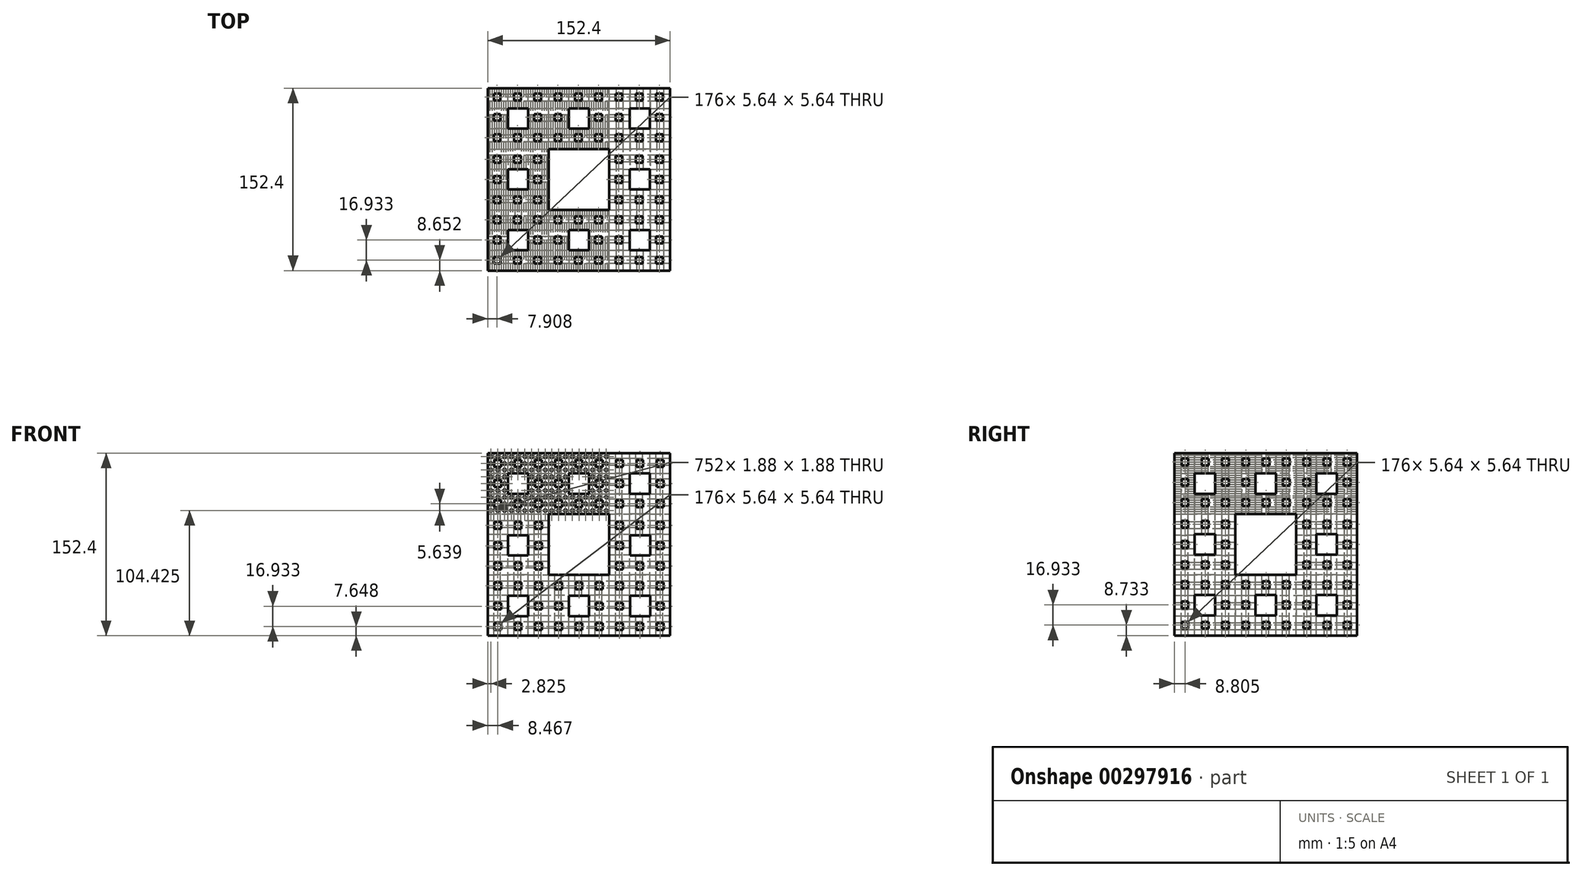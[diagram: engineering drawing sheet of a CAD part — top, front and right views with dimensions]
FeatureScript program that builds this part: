
annotation { "Feature Type Name" : "Feature", "Feature Type Description" : "" }
export const myFeature = defineFeature(function(context is Context, id is Id, definition is map)
    precondition{}
    {
        {
            var Q0;
            Q0=qCreatedBy(makeId("Top.planeOp"),FACE);
            var sketch = newSketch(context, id + "F0", { "sketchPlane" : qUnion([Q0])});
            skLineSegment(sketch, "E0.bottom", {"start": v(76.2, 76.2) * mm, "end": v(-76.2, 76.2) * mm});
            skLineSegment(sketch, "E0.top", {"start": v(76.2, -76.2) * mm, "end": v(-76.2, -76.2) * mm});
            skLineSegment(sketch, "E0.left", {"start": v(76.2, 76.2) * mm, "end": v(76.2, -76.2) * mm});
            skLineSegment(sketch, "E0.right", {"start": v(-76.2, 76.2) * mm, "end": v(-76.2, -76.2) * mm});
            skPoint(sketch, "E0.middle", {"position": v(0, 0) * mm});
            skSolve(sketch);
        }
        {
            var Q0;
            Q0=makeQuery(id+"F0.imprint","IMPRINT",FACE,{"disambiguationData":[TD([[makeQuery(id+"F0.imprint","IMPRINT",EDGE,{"derivedFrom":sQuery(id+"F0.wireOp",EDGE,"E0.bottom")}),1.0]])]});
            extrude(context, id + "F1", {"entities" : qUnion([Q0]), "depth" : 152.4 * mm});
        }
        {
            var Q0;
            Q0=makeQuery(id+"F1.opExtrude","CAP_FACE",FACE,{"disambiguationData":[OSD([sQuery(id+"F0.wireOp",EDGE,"E0.bottom"),sQuery(id+"F0.wireOp",EDGE,"E0.top"),sQuery(id+"F0.wireOp",EDGE,"E0.left"),sQuery(id+"F0.wireOp",EDGE,"E0.right")])],"isStart":false});
            var sketch = newSketch(context, id + "F2", { "sketchPlane" : qUnion([Q0])});
            skLineSegment(sketch, "E1.bottom", {"start": v(-25.4, 25.4) * mm, "end": v(25.4, 25.4) * mm});
            skLineSegment(sketch, "E1.top", {"start": v(-25.4, -25.4) * mm, "end": v(25.4, -25.4) * mm});
            skLineSegment(sketch, "E1.left", {"start": v(-25.4, 25.4) * mm, "end": v(-25.4, -25.4) * mm});
            skLineSegment(sketch, "E1.right", {"start": v(25.4, 25.4) * mm, "end": v(25.4, -25.4) * mm});
            skPoint(sketch, "E1.middle", {"position": v(0, 0) * mm});
            skSolve(sketch);
        }
        {
            var Q0;
            Q0=makeQuery(id+"F2.imprint","IMPRINT",FACE,{"disambiguationData":[TD([[makeQuery(id+"F2.imprint","IMPRINT",EDGE,{"derivedFrom":sQuery(id+"F2.wireOp",EDGE,"E1.bottom")}),-1.0]])]});
            extrude(context, id + "F3", {"entities" : qUnion([Q0]), "operationType" : NewBodyOperationType.REMOVE, "oppositeDirection" : true, "depth" : 216.15 * mm});
        }
        {
            var Q0;
            Q0=makeQuery(id+"F1.opExtrude","SWEPT_FACE",FACE,{"disambiguationData":[OSD([sQuery(id+"F0.wireOp",EDGE,"E0.left")])]});
            var sketch = newSketch(context, id + "F4", { "sketchPlane" : qUnion([Q0])});
            skLineSegment(sketch, "E2.bottom", {"start": v(25.4, 101.6) * mm, "end": v(-25.4, 101.6) * mm});
            skLineSegment(sketch, "E2.top", {"start": v(25.4, 50.8) * mm, "end": v(-25.4, 50.8) * mm});
            skLineSegment(sketch, "E2.left", {"start": v(25.4, 101.6) * mm, "end": v(25.4, 50.8) * mm});
            skLineSegment(sketch, "E2.right", {"start": v(-25.4, 101.6) * mm, "end": v(-25.4, 50.8) * mm});
            skPoint(sketch, "E2.middle", {"position": v(0, 76.2) * mm});
            skPoint(sketch, "E2.middle.positionSnap0", {"position": v(-76.2, 76.2) * mm});
            skPoint(sketch, "E2.centerSnap0", {"position": v(-76.2, 76.2) * mm});
            skSolve(sketch);
        }
        {
            var Q0;
            Q0=makeQuery(id+"F4.imprint","IMPRINT",FACE,{"disambiguationData":[TD([[makeQuery(id+"F4.imprint","IMPRINT",EDGE,{"derivedFrom":sQuery(id+"F4.wireOp",EDGE,"E2.bottom")}),1.0]])]});
            extrude(context, id + "F5", {"entities" : qUnion([Q0]), "operationType" : NewBodyOperationType.REMOVE, "oppositeDirection" : true, "depth" : 233.17 * mm});
        }
        {
            var Q0;
            Q0=makeQuery(id+"F1.opExtrude","SWEPT_FACE",FACE,{"disambiguationData":[OSD([sQuery(id+"F0.wireOp",EDGE,"E0.bottom")])]});
            var sketch = newSketch(context, id + "F6", { "sketchPlane" : qUnion([Q0])});
            skLineSegment(sketch, "E3.bottom", {"start": v(25.4, 101.6) * mm, "end": v(-25.4, 101.6) * mm});
            skLineSegment(sketch, "E3.top", {"start": v(25.4, 50.8) * mm, "end": v(-25.4, 50.8) * mm});
            skLineSegment(sketch, "E3.left", {"start": v(25.4, 101.6) * mm, "end": v(25.4, 50.8) * mm});
            skLineSegment(sketch, "E3.right", {"start": v(-25.4, 101.6) * mm, "end": v(-25.4, 50.8) * mm});
            skPoint(sketch, "E3.middle", {"position": v(0, 76.2) * mm});
            skPoint(sketch, "E3.middle.positionSnap0", {"position": v(-76.2, 76.2) * mm});
            skPoint(sketch, "E3.centerSnap0", {"position": v(-76.2, 76.2) * mm});
            skSolve(sketch);
        }
        {
            var Q0;
            Q0=makeQuery(id+"F6.imprint","IMPRINT",FACE,{"disambiguationData":[TD([[makeQuery(id+"F6.imprint","IMPRINT",EDGE,{"derivedFrom":sQuery(id+"F6.wireOp",EDGE,"E3.bottom")}),1.0]])]});
            extrude(context, id + "F7", {"entities" : qUnion([Q0]), "operationType" : NewBodyOperationType.REMOVE, "oppositeDirection" : true, "depth" : 261.62 * mm});
        }
        {
            var Q0;
            Q0=makeQuery(id+"F1.opExtrude","SWEPT_FACE",FACE,{"disambiguationData":[OSD([sQuery(id+"F0.wireOp",EDGE,"E0.top")])]});
            var sketch = newSketch(context, id + "F8", { "sketchPlane" : qUnion([Q0])});
            skLineSegment(sketch, "E4.bottom", {"start": v(-42.33, 135.47) * mm, "end": v(-59.27, 135.47) * mm});
            skLineSegment(sketch, "E4.top", {"start": v(-42.33, 118.53) * mm, "end": v(-59.27, 118.53) * mm});
            skLineSegment(sketch, "E4.left", {"start": v(-42.33, 135.47) * mm, "end": v(-42.33, 118.53) * mm});
            skLineSegment(sketch, "E4.right", {"start": v(-59.27, 135.47) * mm, "end": v(-59.27, 118.53) * mm});
            skPoint(sketch, "E4.middle", {"position": v(-50.8, 127) * mm});
            skLineSegment(sketch, "E5.1.0.0", {"start": v(8.47, 135.47) * mm, "end": v(-8.47, 135.47) * mm});
            skLineSegment(sketch, "E5.1.0.1", {"start": v(8.47, 135.47) * mm, "end": v(8.47, 118.53) * mm});
            skLineSegment(sketch, "E5.1.0.2", {"start": v(8.47, 118.53) * mm, "end": v(-8.47, 118.53) * mm});
            skLineSegment(sketch, "E5.1.0.3", {"start": v(-8.47, 135.47) * mm, "end": v(-8.47, 118.53) * mm});
            skLineSegment(sketch, "E5.2.0.0", {"start": v(59.27, 135.47) * mm, "end": v(42.33, 135.47) * mm});
            skLineSegment(sketch, "E5.2.0.1", {"start": v(59.27, 135.47) * mm, "end": v(59.27, 118.53) * mm});
            skLineSegment(sketch, "E5.2.0.2", {"start": v(59.27, 118.53) * mm, "end": v(42.33, 118.53) * mm});
            skLineSegment(sketch, "E5.2.0.3", {"start": v(42.33, 135.47) * mm, "end": v(42.33, 118.53) * mm});
            skLineSegment(sketch, "E5.direction1", {"start": v(-59.27, 135.47) * mm, "end": v(-8.47, 135.47) * mm, "construction": true});
            skLineSegment(sketch, "E6.bottom", {"start": v(-59.27, 83.76) * mm, "end": v(-42.33, 83.76) * mm});
            skLineSegment(sketch, "E6.top", {"start": v(-59.27, 66.83) * mm, "end": v(-42.33, 66.83) * mm});
            skLineSegment(sketch, "E6.left", {"start": v(-59.27, 83.76) * mm, "end": v(-59.27, 66.83) * mm});
            skLineSegment(sketch, "E6.right", {"start": v(-42.33, 83.76) * mm, "end": v(-42.33, 66.83) * mm});
            skPoint(sketch, "E6.middle", {"position": v(-50.8, 75.3) * mm});
            skLineSegment(sketch, "E7.bottom", {"start": v(-59.27, 33.21) * mm, "end": v(-42.33, 33.21) * mm});
            skLineSegment(sketch, "E7.top", {"start": v(-59.27, 16.28) * mm, "end": v(-42.33, 16.28) * mm});
            skLineSegment(sketch, "E7.left", {"start": v(-59.27, 33.21) * mm, "end": v(-59.27, 16.28) * mm});
            skLineSegment(sketch, "E7.right", {"start": v(-42.33, 33.21) * mm, "end": v(-42.33, 16.28) * mm});
            skPoint(sketch, "E7.middle", {"position": v(-50.8, 24.74) * mm});
            skLineSegment(sketch, "E8.bottom", {"start": v(-8.47, 33.21) * mm, "end": v(8.47, 33.21) * mm});
            skLineSegment(sketch, "E8.top", {"start": v(-8.47, 16.28) * mm, "end": v(8.47, 16.28) * mm});
            skLineSegment(sketch, "E8.left", {"start": v(-8.47, 33.21) * mm, "end": v(-8.47, 16.28) * mm});
            skLineSegment(sketch, "E8.right", {"start": v(8.47, 33.21) * mm, "end": v(8.47, 16.28) * mm});
            skPoint(sketch, "E8.middle", {"position": v(0, 24.74) * mm});
            skPoint(sketch, "E8.middle.positionSnap0", {"position": v(-42.33, 24.74) * mm});
            skPoint(sketch, "E8.centerSnap0", {"position": v(-42.33, 24.74) * mm});
            skLineSegment(sketch, "E9.bottom", {"start": v(42.62, 33.21) * mm, "end": v(59.55, 33.21) * mm});
            skLineSegment(sketch, "E9.top", {"start": v(42.62, 16.28) * mm, "end": v(59.55, 16.28) * mm});
            skLineSegment(sketch, "E9.left", {"start": v(42.62, 33.21) * mm, "end": v(42.62, 16.28) * mm});
            skLineSegment(sketch, "E9.right", {"start": v(59.55, 33.21) * mm, "end": v(59.55, 16.28) * mm});
            skPoint(sketch, "E9.middle", {"position": v(51.09, 24.74) * mm});
            skPoint(sketch, "E9.middle.positionSnap0", {"position": v(8.47, 24.74) * mm});
            skPoint(sketch, "E9.centerSnap0", {"position": v(8.47, 24.74) * mm});
            skLineSegment(sketch, "E10.bottom", {"start": v(59.55, 83.76) * mm, "end": v(42.62, 83.76) * mm});
            skLineSegment(sketch, "E10.top", {"start": v(59.55, 66.83) * mm, "end": v(42.62, 66.83) * mm});
            skLineSegment(sketch, "E10.left", {"start": v(59.55, 83.76) * mm, "end": v(59.55, 66.83) * mm});
            skLineSegment(sketch, "E10.right", {"start": v(42.62, 83.76) * mm, "end": v(42.62, 66.83) * mm});
            skPoint(sketch, "E10.middle", {"position": v(51.09, 75.3) * mm});
            skPoint(sketch, "E10.middle.positionSnap0", {"position": v(-42.33, 75.3) * mm});
            skPoint(sketch, "E10.middle.positionSnap1", {"position": v(51.09, 33.21) * mm});
            skPoint(sketch, "E10.centerSnap0", {"position": v(-42.33, 75.3) * mm});
            skPoint(sketch, "E10.centerSnap1", {"position": v(51.09, 33.21) * mm});
            skSolve(sketch);
        }
        {
            var Q0;
            Q0=makeQuery(id+"F8.imprint","IMPRINT",FACE,{"disambiguationData":[TD([[makeQuery(id+"F8.imprint","IMPRINT",EDGE,{"derivedFrom":sQuery(id+"F8.wireOp",EDGE,"E5.1.0.0")}),1.0]])]});
            var Q1;
            Q1=makeQuery(id+"F8.imprint","IMPRINT",FACE,{"disambiguationData":[TD([[makeQuery(id+"F8.imprint","IMPRINT",EDGE,{"derivedFrom":sQuery(id+"F8.wireOp",EDGE,"E5.2.0.0")}),1.0]])]});
            var Q2;
            Q2=makeQuery(id+"F8.imprint","IMPRINT",FACE,{"disambiguationData":[TD([[makeQuery(id+"F8.imprint","IMPRINT",EDGE,{"derivedFrom":sQuery(id+"F8.wireOp",EDGE,"E10.bottom")}),1.0]])]});
            var Q3;
            Q3=makeQuery(id+"F8.imprint","IMPRINT",FACE,{"disambiguationData":[TD([[makeQuery(id+"F8.imprint","IMPRINT",EDGE,{"derivedFrom":sQuery(id+"F8.wireOp",EDGE,"E9.bottom")}),-1.0]])]});
            var Q4;
            Q4=makeQuery(id+"F8.imprint","IMPRINT",FACE,{"disambiguationData":[TD([[makeQuery(id+"F8.imprint","IMPRINT",EDGE,{"derivedFrom":sQuery(id+"F8.wireOp",EDGE,"E8.bottom")}),-1.0]])]});
            var Q5;
            Q5=makeQuery(id+"F8.imprint","IMPRINT",FACE,{"disambiguationData":[TD([[makeQuery(id+"F8.imprint","IMPRINT",EDGE,{"derivedFrom":sQuery(id+"F8.wireOp",EDGE,"E7.bottom")}),-1.0]])]});
            var Q6;
            Q6=makeQuery(id+"F8.imprint","IMPRINT",FACE,{"disambiguationData":[TD([[makeQuery(id+"F8.imprint","IMPRINT",EDGE,{"derivedFrom":sQuery(id+"F8.wireOp",EDGE,"E6.bottom")}),-1.0]])]});
            var Q7;
            Q7=makeQuery(id+"F8.imprint","IMPRINT",FACE,{"disambiguationData":[TD([[makeQuery(id+"F8.imprint","IMPRINT",EDGE,{"derivedFrom":sQuery(id+"F8.wireOp",EDGE,"E4.bottom")}),1.0]])]});
            extrude(context, id + "F9", {"entities" : qUnion([Q0, Q1, Q2, Q3, Q4, Q5, Q6, Q7]), "operationType" : NewBodyOperationType.REMOVE, "endBound" : BoundingType.THROUGH_ALL, "oppositeDirection" : true, "depth" : 25.4 * mm});
        }
        {
            var Q0;
            Q0=makeQuery(id+"F1.opExtrude","SWEPT_FACE",FACE,{"disambiguationData":[OSD([sQuery(id+"F0.wireOp",EDGE,"E0.left")])]});
            var sketch = newSketch(context, id + "F10", { "sketchPlane" : qUnion([Q0])});
            skLineSegment(sketch, "E11.bottom", {"start": v(-42.33, 135.47) * mm, "end": v(-59.27, 135.47) * mm});
            skLineSegment(sketch, "E11.top", {"start": v(-42.33, 118.53) * mm, "end": v(-59.27, 118.53) * mm});
            skLineSegment(sketch, "E11.left", {"start": v(-42.33, 135.47) * mm, "end": v(-42.33, 118.53) * mm});
            skLineSegment(sketch, "E11.right", {"start": v(-59.27, 135.47) * mm, "end": v(-59.27, 118.53) * mm});
            skPoint(sketch, "E11.middle", {"position": v(-50.8, 127) * mm});
            skLineSegment(sketch, "E12.bottom", {"start": v(8.47, 135.47) * mm, "end": v(-8.47, 135.47) * mm});
            skLineSegment(sketch, "E12.top", {"start": v(8.47, 118.53) * mm, "end": v(-8.47, 118.53) * mm});
            skLineSegment(sketch, "E12.left", {"start": v(8.47, 135.47) * mm, "end": v(8.47, 118.53) * mm});
            skLineSegment(sketch, "E12.right", {"start": v(-8.47, 135.47) * mm, "end": v(-8.47, 118.53) * mm});
            skPoint(sketch, "E12.middle", {"position": v(0, 127) * mm});
            skLineSegment(sketch, "E13.bottom", {"start": v(59.27, 135.47) * mm, "end": v(42.33, 135.47) * mm});
            skLineSegment(sketch, "E13.top", {"start": v(59.27, 118.53) * mm, "end": v(42.33, 118.53) * mm});
            skLineSegment(sketch, "E13.left", {"start": v(59.27, 135.47) * mm, "end": v(59.27, 118.53) * mm});
            skLineSegment(sketch, "E13.right", {"start": v(42.33, 135.47) * mm, "end": v(42.33, 118.53) * mm});
            skPoint(sketch, "E13.middle", {"position": v(50.8, 127) * mm});
            skLineSegment(sketch, "E14.bottom", {"start": v(42.33, 84.67) * mm, "end": v(59.27, 84.67) * mm});
            skLineSegment(sketch, "E14.top", {"start": v(42.33, 67.73) * mm, "end": v(59.27, 67.73) * mm});
            skLineSegment(sketch, "E14.left", {"start": v(42.33, 84.67) * mm, "end": v(42.33, 67.73) * mm});
            skLineSegment(sketch, "E14.right", {"start": v(59.27, 84.67) * mm, "end": v(59.27, 67.73) * mm});
            skPoint(sketch, "E14.middle", {"position": v(50.8, 76.2) * mm});
            skLineSegment(sketch, "E15.bottom", {"start": v(42.33, 33.87) * mm, "end": v(59.27, 33.87) * mm});
            skLineSegment(sketch, "E15.top", {"start": v(42.33, 16.93) * mm, "end": v(59.27, 16.93) * mm});
            skLineSegment(sketch, "E15.left", {"start": v(42.33, 33.87) * mm, "end": v(42.33, 16.93) * mm});
            skLineSegment(sketch, "E15.right", {"start": v(59.27, 33.87) * mm, "end": v(59.27, 16.93) * mm});
            skPoint(sketch, "E15.middle", {"position": v(50.8, 25.4) * mm});
            skLineSegment(sketch, "E16.bottom", {"start": v(-59.27, 84.67) * mm, "end": v(-42.33, 84.67) * mm});
            skLineSegment(sketch, "E16.top", {"start": v(-59.27, 67.73) * mm, "end": v(-42.33, 67.73) * mm});
            skLineSegment(sketch, "E16.left", {"start": v(-59.27, 84.67) * mm, "end": v(-59.27, 67.73) * mm});
            skLineSegment(sketch, "E16.right", {"start": v(-42.33, 84.67) * mm, "end": v(-42.33, 67.73) * mm});
            skPoint(sketch, "E16.middle", {"position": v(-50.8, 76.2) * mm});
            skLineSegment(sketch, "E17.bottom", {"start": v(-59.27, 33.87) * mm, "end": v(-42.33, 33.87) * mm});
            skLineSegment(sketch, "E17.top", {"start": v(-59.27, 16.93) * mm, "end": v(-42.33, 16.93) * mm});
            skLineSegment(sketch, "E17.left", {"start": v(-59.27, 33.87) * mm, "end": v(-59.27, 16.93) * mm});
            skLineSegment(sketch, "E17.right", {"start": v(-42.33, 33.87) * mm, "end": v(-42.33, 16.93) * mm});
            skPoint(sketch, "E17.middle", {"position": v(-50.8, 25.4) * mm});
            skLineSegment(sketch, "E18.bottom", {"start": v(-8.47, 33.87) * mm, "end": v(8.47, 33.87) * mm});
            skLineSegment(sketch, "E18.top", {"start": v(-8.47, 16.93) * mm, "end": v(8.47, 16.93) * mm});
            skLineSegment(sketch, "E18.left", {"start": v(-8.47, 33.87) * mm, "end": v(-8.47, 16.93) * mm});
            skLineSegment(sketch, "E18.right", {"start": v(8.47, 33.87) * mm, "end": v(8.47, 16.93) * mm});
            skPoint(sketch, "E18.middle", {"position": v(0, 25.4) * mm});
            skSolve(sketch);
        }
        {
            var Q0;
            Q0=makeQuery(id+"F10.imprint","IMPRINT",FACE,{"disambiguationData":[TD([[makeQuery(id+"F10.imprint","IMPRINT",EDGE,{"derivedFrom":sQuery(id+"F10.wireOp",EDGE,"E11.bottom")}),1.0]])]});
            var Q1;
            Q1=makeQuery(id+"F10.imprint","IMPRINT",FACE,{"disambiguationData":[TD([[makeQuery(id+"F10.imprint","IMPRINT",EDGE,{"derivedFrom":sQuery(id+"F10.wireOp",EDGE,"E12.bottom")}),1.0]])]});
            var Q2;
            Q2=makeQuery(id+"F10.imprint","IMPRINT",FACE,{"disambiguationData":[TD([[makeQuery(id+"F10.imprint","IMPRINT",EDGE,{"derivedFrom":sQuery(id+"F10.wireOp",EDGE,"E13.bottom")}),1.0]])]});
            var Q3;
            Q3=makeQuery(id+"F10.imprint","IMPRINT",FACE,{"disambiguationData":[TD([[makeQuery(id+"F10.imprint","IMPRINT",EDGE,{"derivedFrom":sQuery(id+"F10.wireOp",EDGE,"E14.bottom")}),-1.0]])]});
            var Q4;
            Q4=makeQuery(id+"F10.imprint","IMPRINT",FACE,{"disambiguationData":[TD([[makeQuery(id+"F10.imprint","IMPRINT",EDGE,{"derivedFrom":sQuery(id+"F10.wireOp",EDGE,"E15.bottom")}),-1.0]])]});
            var Q5;
            Q5=makeQuery(id+"F10.imprint","IMPRINT",FACE,{"disambiguationData":[TD([[makeQuery(id+"F10.imprint","IMPRINT",EDGE,{"derivedFrom":sQuery(id+"F10.wireOp",EDGE,"E18.bottom")}),-1.0]])]});
            var Q6;
            Q6=makeQuery(id+"F10.imprint","IMPRINT",FACE,{"disambiguationData":[TD([[makeQuery(id+"F10.imprint","IMPRINT",EDGE,{"derivedFrom":sQuery(id+"F10.wireOp",EDGE,"E17.bottom")}),-1.0]])]});
            var Q7;
            Q7=makeQuery(id+"F10.imprint","IMPRINT",FACE,{"disambiguationData":[TD([[makeQuery(id+"F10.imprint","IMPRINT",EDGE,{"derivedFrom":sQuery(id+"F10.wireOp",EDGE,"E16.bottom")}),-1.0]])]});
            extrude(context, id + "F11", {"entities" : qUnion([Q0, Q1, Q2, Q3, Q4, Q5, Q6, Q7]), "operationType" : NewBodyOperationType.REMOVE, "endBound" : BoundingType.THROUGH_ALL, "oppositeDirection" : true, "depth" : 25.4 * mm});
        }
        {
            var Q0;
            Q0=makeQuery(id+"F1.opExtrude","CAP_FACE",FACE,{"disambiguationData":[OSD([sQuery(id+"F0.wireOp",EDGE,"E0.bottom"),sQuery(id+"F0.wireOp",EDGE,"E0.top"),sQuery(id+"F0.wireOp",EDGE,"E0.left"),sQuery(id+"F0.wireOp",EDGE,"E0.right")])],"isStart":false});
            var sketch = newSketch(context, id + "F12", { "sketchPlane" : qUnion([Q0])});
            skLineSegment(sketch, "E19.bottom", {"start": v(-8.47, 59.27) * mm, "end": v(8.47, 59.27) * mm});
            skLineSegment(sketch, "E19.top", {"start": v(-8.47, 42.33) * mm, "end": v(8.47, 42.33) * mm});
            skLineSegment(sketch, "E19.left", {"start": v(-8.47, 59.27) * mm, "end": v(-8.47, 42.33) * mm});
            skLineSegment(sketch, "E19.right", {"start": v(8.47, 59.27) * mm, "end": v(8.47, 42.33) * mm});
            skPoint(sketch, "E19.middle", {"position": v(0, 50.8) * mm});
            skLineSegment(sketch, "E20.bottom", {"start": v(-59.27, 59.27) * mm, "end": v(-42.33, 59.27) * mm});
            skLineSegment(sketch, "E20.top", {"start": v(-59.27, 42.33) * mm, "end": v(-42.33, 42.33) * mm});
            skLineSegment(sketch, "E20.left", {"start": v(-59.27, 59.27) * mm, "end": v(-59.27, 42.33) * mm});
            skLineSegment(sketch, "E20.right", {"start": v(-42.33, 59.27) * mm, "end": v(-42.33, 42.33) * mm});
            skPoint(sketch, "E20.middle", {"position": v(-50.8, 50.8) * mm});
            skLineSegment(sketch, "E21.bottom", {"start": v(42.33, 59.27) * mm, "end": v(59.27, 59.27) * mm});
            skLineSegment(sketch, "E21.top", {"start": v(42.33, 42.33) * mm, "end": v(59.27, 42.33) * mm});
            skLineSegment(sketch, "E21.left", {"start": v(42.33, 59.27) * mm, "end": v(42.33, 42.33) * mm});
            skLineSegment(sketch, "E21.right", {"start": v(59.27, 59.27) * mm, "end": v(59.27, 42.33) * mm});
            skPoint(sketch, "E21.middle", {"position": v(50.8, 50.8) * mm});
            skLineSegment(sketch, "E22.bottom", {"start": v(59.27, -8.47) * mm, "end": v(42.33, -8.47) * mm});
            skLineSegment(sketch, "E22.top", {"start": v(59.27, 8.47) * mm, "end": v(42.33, 8.47) * mm});
            skLineSegment(sketch, "E22.left", {"start": v(59.27, -8.47) * mm, "end": v(59.27, 8.47) * mm});
            skLineSegment(sketch, "E22.right", {"start": v(42.33, -8.47) * mm, "end": v(42.33, 8.47) * mm});
            skPoint(sketch, "E22.middle", {"position": v(50.8, 0) * mm});
            skLineSegment(sketch, "E23.bottom", {"start": v(59.27, -59.27) * mm, "end": v(42.33, -59.27) * mm});
            skLineSegment(sketch, "E23.top", {"start": v(59.27, -42.33) * mm, "end": v(42.33, -42.33) * mm});
            skLineSegment(sketch, "E23.left", {"start": v(59.27, -59.27) * mm, "end": v(59.27, -42.33) * mm});
            skLineSegment(sketch, "E23.right", {"start": v(42.33, -59.27) * mm, "end": v(42.33, -42.33) * mm});
            skPoint(sketch, "E23.middle", {"position": v(50.8, -50.8) * mm});
            skPoint(sketch, "E24.middle", {"position": v(-8.47, -30.86) * mm});
            skLineSegment(sketch, "E25.bottom", {"start": v(-42.33, -59.27) * mm, "end": v(-59.27, -59.27) * mm});
            skLineSegment(sketch, "E25.top", {"start": v(-42.33, -42.33) * mm, "end": v(-59.27, -42.33) * mm});
            skLineSegment(sketch, "E25.left", {"start": v(-42.33, -59.27) * mm, "end": v(-42.33, -42.33) * mm});
            skLineSegment(sketch, "E25.right", {"start": v(-59.27, -59.27) * mm, "end": v(-59.27, -42.33) * mm});
            skPoint(sketch, "E25.middle", {"position": v(-50.8, -50.8) * mm});
            skLineSegment(sketch, "E26.bottom", {"start": v(-42.33, -8.47) * mm, "end": v(-59.27, -8.47) * mm});
            skLineSegment(sketch, "E26.top", {"start": v(-42.33, 8.47) * mm, "end": v(-59.27, 8.47) * mm});
            skLineSegment(sketch, "E26.left", {"start": v(-42.33, -8.47) * mm, "end": v(-42.33, 8.47) * mm});
            skLineSegment(sketch, "E26.right", {"start": v(-59.27, -8.47) * mm, "end": v(-59.27, 8.47) * mm});
            skPoint(sketch, "E26.middle", {"position": v(-50.8, 0) * mm});
            skLineSegment(sketch, "E27.bottom", {"start": v(-8.47, -42.33) * mm, "end": v(8.47, -42.33) * mm});
            skLineSegment(sketch, "E27.top", {"start": v(-8.47, -59.27) * mm, "end": v(8.47, -59.27) * mm});
            skLineSegment(sketch, "E27.left", {"start": v(-8.47, -42.33) * mm, "end": v(-8.47, -59.27) * mm});
            skLineSegment(sketch, "E27.right", {"start": v(8.47, -42.33) * mm, "end": v(8.47, -59.27) * mm});
            skPoint(sketch, "E27.middle", {"position": v(0, -50.8) * mm});
            skSolve(sketch);
        }
        {
            var Q0;
            Q0=makeQuery(id+"F12.imprint","IMPRINT",FACE,{"disambiguationData":[TD([[makeQuery(id+"F12.imprint","IMPRINT",EDGE,{"derivedFrom":sQuery(id+"F12.wireOp",EDGE,"E20.bottom")}),-1.0]])]});
            var Q1;
            Q1=makeQuery(id+"F12.imprint","IMPRINT",FACE,{"disambiguationData":[TD([[makeQuery(id+"F12.imprint","IMPRINT",EDGE,{"derivedFrom":sQuery(id+"F12.wireOp",EDGE,"E19.bottom")}),-1.0]])]});
            var Q2;
            Q2=makeQuery(id+"F12.imprint","IMPRINT",FACE,{"disambiguationData":[TD([[makeQuery(id+"F12.imprint","IMPRINT",EDGE,{"derivedFrom":sQuery(id+"F12.wireOp",EDGE,"E21.bottom")}),-1.0]])]});
            var Q3;
            Q3=makeQuery(id+"F12.imprint","IMPRINT",FACE,{"disambiguationData":[TD([[makeQuery(id+"F12.imprint","IMPRINT",EDGE,{"derivedFrom":sQuery(id+"F12.wireOp",EDGE,"E22.bottom")}),-1.0]])]});
            var Q4;
            Q4=makeQuery(id+"F12.imprint","IMPRINT",FACE,{"disambiguationData":[TD([[makeQuery(id+"F12.imprint","IMPRINT",EDGE,{"derivedFrom":sQuery(id+"F12.wireOp",EDGE,"E23.bottom")}),-1.0]])]});
            var Q5;
            Q5=makeQuery(id+"F12.imprint","IMPRINT",FACE,{"disambiguationData":[TD([[makeQuery(id+"F12.imprint","IMPRINT",EDGE,{"derivedFrom":sQuery(id+"F12.wireOp",EDGE,"E27.bottom")}),-1.0]])]});
            var Q6;
            Q6=makeQuery(id+"F12.imprint","IMPRINT",FACE,{"disambiguationData":[TD([[makeQuery(id+"F12.imprint","IMPRINT",EDGE,{"derivedFrom":sQuery(id+"F12.wireOp",EDGE,"E25.bottom")}),-1.0]])]});
            var Q7;
            Q7=makeQuery(id+"F12.imprint","IMPRINT",FACE,{"disambiguationData":[TD([[makeQuery(id+"F12.imprint","IMPRINT",EDGE,{"derivedFrom":sQuery(id+"F12.wireOp",EDGE,"E26.bottom")}),-1.0]])]});
            extrude(context, id + "F13", {"entities" : qUnion([Q0, Q1, Q2, Q3, Q4, Q5, Q6, Q7]), "operationType" : NewBodyOperationType.REMOVE, "endBound" : BoundingType.THROUGH_ALL, "oppositeDirection" : true, "depth" : 25.4 * mm});
        }
        {
            var Q0;
            Q0=makeQuery(id+"F1.opExtrude","SWEPT_FACE",FACE,{"disambiguationData":[OSD([sQuery(id+"F0.wireOp",EDGE,"E0.top")])]});
            var sketch = newSketch(context, id + "F14", { "sketchPlane" : qUnion([Q0])});
            skLineSegment(sketch, "E28.bottom", {"start": v(-47.98, 146.76) * mm, "end": v(-53.62, 146.76) * mm});
            skLineSegment(sketch, "E28.top", {"start": v(-47.98, 141.11) * mm, "end": v(-53.62, 141.11) * mm});
            skLineSegment(sketch, "E28.left", {"start": v(-47.98, 146.76) * mm, "end": v(-47.98, 141.11) * mm});
            skLineSegment(sketch, "E28.right", {"start": v(-53.62, 146.76) * mm, "end": v(-53.62, 141.11) * mm});
            skPoint(sketch, "E28.middle", {"position": v(-50.8, 143.93) * mm});
            skPoint(sketch, "E28.middle.positionSnap0", {"position": v(-50.8, 135.47) * mm});
            skPoint(sketch, "E28.centerSnap0", {"position": v(-50.8, 135.47) * mm});
            skLineSegment(sketch, "E29.bottom", {"start": v(-36.69, 146.76) * mm, "end": v(-31.04, 146.76) * mm});
            skLineSegment(sketch, "E29.top", {"start": v(-36.69, 141.11) * mm, "end": v(-31.04, 141.11) * mm});
            skLineSegment(sketch, "E29.left", {"start": v(-36.69, 146.76) * mm, "end": v(-36.69, 141.11) * mm});
            skLineSegment(sketch, "E29.right", {"start": v(-31.04, 146.76) * mm, "end": v(-31.04, 141.11) * mm});
            skPoint(sketch, "E29.middle", {"position": v(-33.87, 143.93) * mm});
            skPoint(sketch, "E29.middle.positionSnap0", {"position": v(-47.98, 143.93) * mm});
            skPoint(sketch, "E29.centerSnap0", {"position": v(-47.98, 143.93) * mm});
            skLineSegment(sketch, "E30.bottom", {"start": v(-70.56, 146.76) * mm, "end": v(-64.91, 146.76) * mm});
            skLineSegment(sketch, "E30.top", {"start": v(-70.56, 141.11) * mm, "end": v(-64.91, 141.11) * mm});
            skLineSegment(sketch, "E30.left", {"start": v(-70.56, 146.76) * mm, "end": v(-70.56, 141.11) * mm});
            skLineSegment(sketch, "E30.right", {"start": v(-64.91, 146.76) * mm, "end": v(-64.91, 141.11) * mm});
            skPoint(sketch, "E30.middle", {"position": v(-67.73, 143.93) * mm});
            skPoint(sketch, "E30.middle.positionSnap0", {"position": v(-53.62, 143.93) * mm});
            skPoint(sketch, "E30.centerSnap0", {"position": v(-53.62, 143.93) * mm});
            skLineSegment(sketch, "E31.bottom", {"start": v(-64.91, 129.82) * mm, "end": v(-70.56, 129.82) * mm});
            skLineSegment(sketch, "E31.top", {"start": v(-64.91, 124.18) * mm, "end": v(-70.56, 124.18) * mm});
            skLineSegment(sketch, "E31.left", {"start": v(-64.91, 129.82) * mm, "end": v(-64.91, 124.18) * mm});
            skLineSegment(sketch, "E31.right", {"start": v(-70.56, 129.82) * mm, "end": v(-70.56, 124.18) * mm});
            skPoint(sketch, "E31.middle", {"position": v(-67.73, 127) * mm});
            skPoint(sketch, "E31.middle.positionSnap0", {"position": v(-59.27, 127) * mm});
            skPoint(sketch, "E31.middle.positionSnap1", {"position": v(-67.73, 141.11) * mm});
            skPoint(sketch, "E31.centerSnap0", {"position": v(-59.27, 127) * mm});
            skPoint(sketch, "E31.centerSnap1", {"position": v(-67.73, 141.11) * mm});
            skLineSegment(sketch, "E32.bottom", {"start": v(-64.91, 112.89) * mm, "end": v(-70.56, 112.89) * mm});
            skLineSegment(sketch, "E32.top", {"start": v(-64.91, 107.24) * mm, "end": v(-70.56, 107.24) * mm});
            skLineSegment(sketch, "E32.left", {"start": v(-64.91, 112.89) * mm, "end": v(-64.91, 107.24) * mm});
            skLineSegment(sketch, "E32.right", {"start": v(-70.56, 112.89) * mm, "end": v(-70.56, 107.24) * mm});
            skPoint(sketch, "E32.middle", {"position": v(-67.73, 110.07) * mm});
            skPoint(sketch, "E32.middle.positionSnap0", {"position": v(-67.73, 124.18) * mm});
            skPoint(sketch, "E32.centerSnap0", {"position": v(-67.73, 124.18) * mm});
            skLineSegment(sketch, "E33.bottom", {"start": v(-36.69, 129.82) * mm, "end": v(-31.04, 129.82) * mm});
            skLineSegment(sketch, "E33.top", {"start": v(-36.69, 124.18) * mm, "end": v(-31.04, 124.18) * mm});
            skLineSegment(sketch, "E33.left", {"start": v(-36.69, 129.82) * mm, "end": v(-36.69, 124.18) * mm});
            skLineSegment(sketch, "E33.right", {"start": v(-31.04, 129.82) * mm, "end": v(-31.04, 124.18) * mm});
            skPoint(sketch, "E33.middle", {"position": v(-33.87, 127) * mm});
            skPoint(sketch, "E33.middle.positionSnap0", {"position": v(-42.33, 127) * mm});
            skPoint(sketch, "E33.middle.positionSnap1", {"position": v(-33.87, 141.11) * mm});
            skPoint(sketch, "E33.centerSnap0", {"position": v(-42.33, 127) * mm});
            skPoint(sketch, "E33.centerSnap1", {"position": v(-33.87, 141.11) * mm});
            skLineSegment(sketch, "E34.bottom", {"start": v(-36.69, 112.89) * mm, "end": v(-31.04, 112.89) * mm});
            skLineSegment(sketch, "E34.top", {"start": v(-36.69, 107.24) * mm, "end": v(-31.04, 107.24) * mm});
            skLineSegment(sketch, "E34.left", {"start": v(-36.69, 112.89) * mm, "end": v(-36.69, 107.24) * mm});
            skLineSegment(sketch, "E34.right", {"start": v(-31.04, 112.89) * mm, "end": v(-31.04, 107.24) * mm});
            skPoint(sketch, "E34.middle", {"position": v(-33.87, 110.07) * mm});
            skLineSegment(sketch, "E35.bottom", {"start": v(-53.62, 112.89) * mm, "end": v(-47.98, 112.89) * mm});
            skLineSegment(sketch, "E35.top", {"start": v(-53.62, 107.24) * mm, "end": v(-47.98, 107.24) * mm});
            skLineSegment(sketch, "E35.left", {"start": v(-53.62, 112.89) * mm, "end": v(-53.62, 107.24) * mm});
            skLineSegment(sketch, "E35.right", {"start": v(-47.98, 112.89) * mm, "end": v(-47.98, 107.24) * mm});
            skPoint(sketch, "E35.middle", {"position": v(-50.8, 110.07) * mm});
            skPoint(sketch, "E35.middle.positionSnap0", {"position": v(-50.8, 118.53) * mm});
            skPoint(sketch, "E35.centerSnap0", {"position": v(-50.8, 118.53) * mm});
            skLineSegment(sketch, "E36.1.0.0", {"start": v(-2.82, 107.24) * mm, "end": v(2.82, 107.24) * mm});
            skPoint(sketch, "E36.1.0.1", {"position": v(-16.93, 141.11) * mm});
            skLineSegment(sketch, "E36.1.0.2", {"start": v(-2.82, 112.89) * mm, "end": v(-2.82, 107.24) * mm});
            skPoint(sketch, "E36.1.0.3", {"position": v(-16.93, 110.07) * mm});
            skLineSegment(sketch, "E36.1.0.4", {"start": v(2.82, 112.89) * mm, "end": v(2.82, 107.24) * mm});
            skPoint(sketch, "E36.1.0.5", {"position": v(-16.93, 124.18) * mm});
            skLineSegment(sketch, "E36.1.0.6", {"start": v(-14.11, 129.82) * mm, "end": v(-14.11, 124.18) * mm});
            skLineSegment(sketch, "E36.1.0.7", {"start": v(-19.76, 129.82) * mm, "end": v(-19.76, 124.18) * mm});
            skPoint(sketch, "E36.1.0.8", {"position": v(0, 143.93) * mm});
            skLineSegment(sketch, "E36.1.0.9", {"start": v(2.82, 146.76) * mm, "end": v(-2.82, 146.76) * mm});
            skLineSegment(sketch, "E36.1.0.10", {"start": v(2.82, 141.11) * mm, "end": v(-2.82, 141.11) * mm});
            skLineSegment(sketch, "E36.1.0.11", {"start": v(14.11, 146.76) * mm, "end": v(19.76, 146.76) * mm});
            skLineSegment(sketch, "E36.1.0.12", {"start": v(14.11, 146.76) * mm, "end": v(14.11, 141.11) * mm});
            skLineSegment(sketch, "E36.1.0.13", {"start": v(-14.11, 112.89) * mm, "end": v(-19.76, 112.89) * mm});
            skLineSegment(sketch, "E36.1.0.14", {"start": v(19.76, 146.76) * mm, "end": v(19.76, 141.11) * mm});
            skLineSegment(sketch, "E36.1.0.15", {"start": v(-19.76, 146.76) * mm, "end": v(-14.11, 146.76) * mm});
            skLineSegment(sketch, "E36.1.0.16", {"start": v(-19.76, 146.76) * mm, "end": v(-19.76, 141.11) * mm});
            skLineSegment(sketch, "E36.1.0.17", {"start": v(-14.11, 146.76) * mm, "end": v(-14.11, 141.11) * mm});
            skLineSegment(sketch, "E36.1.0.18", {"start": v(-14.11, 129.82) * mm, "end": v(-19.76, 129.82) * mm});
            skLineSegment(sketch, "E36.1.0.19", {"start": v(-14.11, 107.24) * mm, "end": v(-19.76, 107.24) * mm});
            skPoint(sketch, "E36.1.0.20", {"position": v(16.93, 127) * mm});
            skLineSegment(sketch, "E36.1.0.21", {"start": v(-14.11, 112.89) * mm, "end": v(-14.11, 107.24) * mm});
            skPoint(sketch, "E36.1.0.22", {"position": v(8.47, 127) * mm});
            skPoint(sketch, "E36.1.0.23", {"position": v(0, 135.47) * mm});
            skLineSegment(sketch, "E36.1.0.24", {"start": v(-19.76, 112.89) * mm, "end": v(-19.76, 107.24) * mm});
            skPoint(sketch, "E36.1.0.25", {"position": v(16.93, 143.93) * mm});
            skLineSegment(sketch, "E36.1.0.26", {"start": v(14.11, 129.82) * mm, "end": v(19.76, 129.82) * mm});
            skLineSegment(sketch, "E36.1.0.27", {"start": v(14.11, 124.18) * mm, "end": v(19.76, 124.18) * mm});
            skPoint(sketch, "E36.1.0.28", {"position": v(16.93, 141.11) * mm});
            skPoint(sketch, "E36.1.0.29", {"position": v(2.82, 143.93) * mm});
            skLineSegment(sketch, "E36.1.0.30", {"start": v(14.11, 129.82) * mm, "end": v(14.11, 124.18) * mm});
            skPoint(sketch, "E36.1.0.31", {"position": v(16.93, 110.07) * mm});
            skPoint(sketch, "E36.1.0.32", {"position": v(-16.93, 143.93) * mm});
            skPoint(sketch, "E36.1.0.33", {"position": v(0, 110.07) * mm});
            skLineSegment(sketch, "E36.1.0.34", {"start": v(19.76, 129.82) * mm, "end": v(19.76, 124.18) * mm});
            skPoint(sketch, "E36.1.0.35", {"position": v(-2.82, 143.93) * mm});
            skLineSegment(sketch, "E36.1.0.36", {"start": v(14.11, 112.89) * mm, "end": v(19.76, 112.89) * mm});
            skPoint(sketch, "E36.1.0.37", {"position": v(0, 118.53) * mm});
            skPoint(sketch, "E36.1.0.38", {"position": v(-16.93, 127) * mm});
            skLineSegment(sketch, "E36.1.0.39", {"start": v(14.11, 107.24) * mm, "end": v(19.76, 107.24) * mm});
            skLineSegment(sketch, "E36.1.0.40", {"start": v(14.11, 112.89) * mm, "end": v(14.11, 107.24) * mm});
            skLineSegment(sketch, "E36.1.0.41", {"start": v(19.76, 112.89) * mm, "end": v(19.76, 107.24) * mm});
            skPoint(sketch, "E36.1.0.42", {"position": v(-8.47, 127) * mm});
            skLineSegment(sketch, "E36.1.0.43", {"start": v(-2.82, 112.89) * mm, "end": v(2.82, 112.89) * mm});
            skPoint(sketch, "E36.1.0.44", {"position": v(-16.93, 124.18) * mm});
            skPoint(sketch, "E36.1.0.45", {"position": v(0, 135.47) * mm});
            skPoint(sketch, "E36.1.0.46", {"position": v(16.93, 141.11) * mm});
            skPoint(sketch, "E36.1.0.47", {"position": v(8.47, 127) * mm});
            skPoint(sketch, "E36.1.0.48", {"position": v(2.82, 143.93) * mm});
            skPoint(sketch, "E36.1.0.49", {"position": v(-2.82, 143.93) * mm});
            skPoint(sketch, "E36.1.0.50", {"position": v(0, 118.53) * mm});
            skPoint(sketch, "E36.1.0.51", {"position": v(-8.47, 127) * mm});
            skPoint(sketch, "E36.1.0.52", {"position": v(-16.93, 141.11) * mm});
            skLineSegment(sketch, "E36.1.0.53", {"start": v(-14.11, 124.18) * mm, "end": v(-19.76, 124.18) * mm});
            skLineSegment(sketch, "E36.1.0.54", {"start": v(2.82, 146.76) * mm, "end": v(2.82, 141.11) * mm});
            skLineSegment(sketch, "E36.1.0.55", {"start": v(-2.82, 146.76) * mm, "end": v(-2.82, 141.11) * mm});
            skLineSegment(sketch, "E36.1.0.56", {"start": v(14.11, 141.11) * mm, "end": v(19.76, 141.11) * mm});
            skLineSegment(sketch, "E36.1.0.57", {"start": v(-19.76, 141.11) * mm, "end": v(-14.11, 141.11) * mm});
            skLineSegment(sketch, "E36.2.0.0", {"start": v(47.98, 107.24) * mm, "end": v(53.62, 107.24) * mm});
            skPoint(sketch, "E36.2.0.1", {"position": v(33.87, 141.11) * mm});
            skLineSegment(sketch, "E36.2.0.2", {"start": v(47.98, 112.89) * mm, "end": v(47.98, 107.24) * mm});
            skPoint(sketch, "E36.2.0.3", {"position": v(33.87, 110.07) * mm});
            skLineSegment(sketch, "E36.2.0.4", {"start": v(53.62, 112.89) * mm, "end": v(53.62, 107.24) * mm});
            skPoint(sketch, "E36.2.0.5", {"position": v(33.87, 124.18) * mm});
            skLineSegment(sketch, "E36.2.0.6", {"start": v(36.69, 129.82) * mm, "end": v(36.69, 124.18) * mm});
            skLineSegment(sketch, "E36.2.0.7", {"start": v(31.04, 129.82) * mm, "end": v(31.04, 124.18) * mm});
            skPoint(sketch, "E36.2.0.8", {"position": v(50.8, 143.93) * mm});
            skLineSegment(sketch, "E36.2.0.9", {"start": v(53.62, 146.76) * mm, "end": v(47.98, 146.76) * mm});
            skLineSegment(sketch, "E36.2.0.10", {"start": v(53.62, 141.11) * mm, "end": v(47.98, 141.11) * mm});
            skLineSegment(sketch, "E36.2.0.11", {"start": v(64.91, 146.76) * mm, "end": v(70.56, 146.76) * mm});
            skLineSegment(sketch, "E36.2.0.12", {"start": v(64.91, 146.76) * mm, "end": v(64.91, 141.11) * mm});
            skLineSegment(sketch, "E36.2.0.13", {"start": v(36.69, 112.89) * mm, "end": v(31.04, 112.89) * mm});
            skLineSegment(sketch, "E36.2.0.14", {"start": v(70.56, 146.76) * mm, "end": v(70.56, 141.11) * mm});
            skLineSegment(sketch, "E36.2.0.15", {"start": v(31.04, 146.76) * mm, "end": v(36.69, 146.76) * mm});
            skLineSegment(sketch, "E36.2.0.16", {"start": v(31.04, 146.76) * mm, "end": v(31.04, 141.11) * mm});
            skLineSegment(sketch, "E36.2.0.17", {"start": v(36.69, 146.76) * mm, "end": v(36.69, 141.11) * mm});
            skLineSegment(sketch, "E36.2.0.18", {"start": v(36.69, 129.82) * mm, "end": v(31.04, 129.82) * mm});
            skLineSegment(sketch, "E36.2.0.19", {"start": v(36.69, 107.24) * mm, "end": v(31.04, 107.24) * mm});
            skPoint(sketch, "E36.2.0.20", {"position": v(67.73, 127) * mm});
            skLineSegment(sketch, "E36.2.0.21", {"start": v(36.69, 112.89) * mm, "end": v(36.69, 107.24) * mm});
            skPoint(sketch, "E36.2.0.22", {"position": v(59.27, 127) * mm});
            skPoint(sketch, "E36.2.0.23", {"position": v(50.8, 135.47) * mm});
            skLineSegment(sketch, "E36.2.0.24", {"start": v(31.04, 112.89) * mm, "end": v(31.04, 107.24) * mm});
            skPoint(sketch, "E36.2.0.25", {"position": v(67.73, 143.93) * mm});
            skLineSegment(sketch, "E36.2.0.26", {"start": v(64.91, 129.82) * mm, "end": v(70.56, 129.82) * mm});
            skLineSegment(sketch, "E36.2.0.27", {"start": v(64.91, 124.18) * mm, "end": v(70.56, 124.18) * mm});
            skPoint(sketch, "E36.2.0.28", {"position": v(67.73, 141.11) * mm});
            skPoint(sketch, "E36.2.0.29", {"position": v(53.62, 143.93) * mm});
            skLineSegment(sketch, "E36.2.0.30", {"start": v(64.91, 129.82) * mm, "end": v(64.91, 124.18) * mm});
            skPoint(sketch, "E36.2.0.31", {"position": v(67.73, 110.07) * mm});
            skPoint(sketch, "E36.2.0.32", {"position": v(33.87, 143.93) * mm});
            skPoint(sketch, "E36.2.0.33", {"position": v(50.8, 110.07) * mm});
            skLineSegment(sketch, "E36.2.0.34", {"start": v(70.56, 129.82) * mm, "end": v(70.56, 124.18) * mm});
            skPoint(sketch, "E36.2.0.35", {"position": v(47.98, 143.93) * mm});
            skLineSegment(sketch, "E36.2.0.36", {"start": v(64.91, 112.89) * mm, "end": v(70.56, 112.89) * mm});
            skPoint(sketch, "E36.2.0.37", {"position": v(50.8, 118.53) * mm});
            skPoint(sketch, "E36.2.0.38", {"position": v(33.87, 127) * mm});
            skLineSegment(sketch, "E36.2.0.39", {"start": v(64.91, 107.24) * mm, "end": v(70.56, 107.24) * mm});
            skLineSegment(sketch, "E36.2.0.40", {"start": v(64.91, 112.89) * mm, "end": v(64.91, 107.24) * mm});
            skLineSegment(sketch, "E36.2.0.41", {"start": v(70.56, 112.89) * mm, "end": v(70.56, 107.24) * mm});
            skPoint(sketch, "E36.2.0.42", {"position": v(42.33, 127) * mm});
            skLineSegment(sketch, "E36.2.0.43", {"start": v(47.98, 112.89) * mm, "end": v(53.62, 112.89) * mm});
            skPoint(sketch, "E36.2.0.44", {"position": v(33.87, 124.18) * mm});
            skPoint(sketch, "E36.2.0.45", {"position": v(50.8, 135.47) * mm});
            skPoint(sketch, "E36.2.0.46", {"position": v(67.73, 141.11) * mm});
            skPoint(sketch, "E36.2.0.47", {"position": v(59.27, 127) * mm});
            skPoint(sketch, "E36.2.0.48", {"position": v(53.62, 143.93) * mm});
            skPoint(sketch, "E36.2.0.49", {"position": v(47.98, 143.93) * mm});
            skPoint(sketch, "E36.2.0.50", {"position": v(50.8, 118.53) * mm});
            skPoint(sketch, "E36.2.0.51", {"position": v(42.33, 127) * mm});
            skPoint(sketch, "E36.2.0.52", {"position": v(33.87, 141.11) * mm});
            skLineSegment(sketch, "E36.2.0.53", {"start": v(36.69, 124.18) * mm, "end": v(31.04, 124.18) * mm});
            skLineSegment(sketch, "E36.2.0.54", {"start": v(53.62, 146.76) * mm, "end": v(53.62, 141.11) * mm});
            skLineSegment(sketch, "E36.2.0.55", {"start": v(47.98, 146.76) * mm, "end": v(47.98, 141.11) * mm});
            skLineSegment(sketch, "E36.2.0.56", {"start": v(64.91, 141.11) * mm, "end": v(70.56, 141.11) * mm});
            skLineSegment(sketch, "E36.2.0.57", {"start": v(31.04, 141.11) * mm, "end": v(36.69, 141.11) * mm});
            skLineSegment(sketch, "E36.direction1", {"start": v(-70.56, 107.24) * mm, "end": v(-19.76, 107.24) * mm, "construction": true});
            skLineSegment(sketch, "E37", {"start": v(25.4, 100.44) * mm, "end": v(76.2, 100.44) * mm});
            skLineSegment(sketch, "E38.MirrorCS", {"start": v(36.69, 89.15) * mm, "end": v(31.04, 89.15) * mm});
            skLineSegment(sketch, "E39.MirrorCS", {"start": v(70.56, 89.15) * mm, "end": v(70.56, 94.8) * mm});
            skLineSegment(sketch, "E40.MirrorCS", {"start": v(47.98, 89.15) * mm, "end": v(53.62, 89.15) * mm});
            skLineSegment(sketch, "E41.MirrorCS", {"start": v(70.56, 55.29) * mm, "end": v(70.56, 60.93) * mm});
            skLineSegment(sketch, "E42.MirrorCS", {"start": v(47.98, 55.29) * mm, "end": v(47.98, 60.93) * mm});
            skLineSegment(sketch, "E43.MirrorCS", {"start": v(36.69, 55.29) * mm, "end": v(36.69, 60.93) * mm});
            skLineSegment(sketch, "E44.MirrorCS", {"start": v(36.69, 77.87) * mm, "end": v(31.04, 77.87) * mm});
            skLineSegment(sketch, "E45.MirrorCS", {"start": v(31.04, 55.29) * mm, "end": v(36.69, 55.29) * mm});
            skLineSegment(sketch, "E46.MirrorCS", {"start": v(64.91, 60.93) * mm, "end": v(70.56, 60.93) * mm});
            skLineSegment(sketch, "E47.MirrorCS", {"start": v(36.69, 72.22) * mm, "end": v(31.04, 72.22) * mm});
            skLineSegment(sketch, "E48.MirrorCS", {"start": v(53.62, 55.29) * mm, "end": v(53.62, 60.93) * mm});
            skLineSegment(sketch, "E49.MirrorCS", {"start": v(31.04, 55.29) * mm, "end": v(31.04, 60.93) * mm});
            skLineSegment(sketch, "E50.MirrorCS", {"start": v(31.04, 60.93) * mm, "end": v(36.69, 60.93) * mm});
            skLineSegment(sketch, "E51.MirrorCS", {"start": v(36.69, 94.8) * mm, "end": v(31.04, 94.8) * mm});
            skLineSegment(sketch, "E52.MirrorCS", {"start": v(47.98, 94.8) * mm, "end": v(53.62, 94.8) * mm});
            skLineSegment(sketch, "E53.MirrorCS", {"start": v(36.69, 89.15) * mm, "end": v(36.69, 94.8) * mm});
            skLineSegment(sketch, "E54.MirrorCS", {"start": v(47.98, 89.15) * mm, "end": v(47.98, 94.8) * mm});
            skLineSegment(sketch, "E55.MirrorCS", {"start": v(31.04, 89.15) * mm, "end": v(31.04, 94.8) * mm});
            skLineSegment(sketch, "E56.MirrorCS", {"start": v(53.62, 89.15) * mm, "end": v(53.62, 94.8) * mm});
            skLineSegment(sketch, "E57.MirrorCS", {"start": v(64.91, 72.22) * mm, "end": v(70.56, 72.22) * mm});
            skLineSegment(sketch, "E58.MirrorCS", {"start": v(36.69, 72.22) * mm, "end": v(36.69, 77.87) * mm});
            skLineSegment(sketch, "E59.MirrorCS", {"start": v(64.91, 77.87) * mm, "end": v(70.56, 77.87) * mm});
            skLineSegment(sketch, "E60.MirrorCS", {"start": v(31.04, 72.22) * mm, "end": v(31.04, 77.87) * mm});
            skLineSegment(sketch, "E61.MirrorCS", {"start": v(64.91, 55.29) * mm, "end": v(64.91, 60.93) * mm});
            skLineSegment(sketch, "E62.MirrorCS", {"start": v(64.91, 89.15) * mm, "end": v(64.91, 94.8) * mm});
            skLineSegment(sketch, "E63.MirrorCS", {"start": v(64.91, 55.29) * mm, "end": v(70.56, 55.29) * mm});
            skLineSegment(sketch, "E64.MirrorCS", {"start": v(64.91, 94.8) * mm, "end": v(70.56, 94.8) * mm});
            skLineSegment(sketch, "E65.MirrorCS", {"start": v(64.91, 89.15) * mm, "end": v(70.56, 89.15) * mm});
            skLineSegment(sketch, "E66.MirrorCS", {"start": v(53.62, 60.93) * mm, "end": v(47.98, 60.93) * mm});
            skLineSegment(sketch, "E67.MirrorCS", {"start": v(70.56, 72.22) * mm, "end": v(70.56, 77.87) * mm});
            skLineSegment(sketch, "E68.MirrorCS", {"start": v(53.62, 55.29) * mm, "end": v(47.98, 55.29) * mm});
            skLineSegment(sketch, "E69.MirrorCS", {"start": v(64.91, 72.22) * mm, "end": v(64.91, 77.87) * mm});
            skPoint(sketch, "E70.MirrorP", {"position": v(50.8, 58.1) * mm});
            skPoint(sketch, "E71.MirrorP", {"position": v(67.73, 75.04) * mm});
            skPoint(sketch, "E72.MirrorP", {"position": v(67.73, 58.1) * mm});
            skPoint(sketch, "E73.MirrorP", {"position": v(67.73, 91.98) * mm});
            skPoint(sketch, "E74.MirrorP", {"position": v(33.87, 58.1) * mm});
            skPoint(sketch, "E75.MirrorP", {"position": v(33.87, 91.98) * mm});
            skPoint(sketch, "E76.MirrorP", {"position": v(33.87, 75.04) * mm});
            skPoint(sketch, "E77.MirrorP", {"position": v(50.8, 91.98) * mm});
            skPoint(sketch, "E78.MirrorP", {"position": v(50.8, 66.58) * mm});
            skPoint(sketch, "E79.MirrorP", {"position": v(33.87, 77.87) * mm});
            skPoint(sketch, "E80.MirrorP", {"position": v(67.73, 60.93) * mm});
            skPoint(sketch, "E81.MirrorP", {"position": v(53.62, 58.1) * mm});
            skPoint(sketch, "E82.MirrorP", {"position": v(59.27, 75.04) * mm});
            skPoint(sketch, "E83.MirrorP", {"position": v(47.98, 58.1) * mm});
            skPoint(sketch, "E84.MirrorP", {"position": v(50.8, 83.5) * mm});
            skPoint(sketch, "E85.MirrorP", {"position": v(42.33, 75.04) * mm});
            skPoint(sketch, "E86.MirrorP", {"position": v(33.87, 60.93) * mm});
            skLineSegment(sketch, "E87.MirrorCS", {"start": v(-36.69, 94.8) * mm, "end": v(-31.04, 94.8) * mm});
            skLineSegment(sketch, "E88.MirrorCS", {"start": v(-36.69, 89.15) * mm, "end": v(-31.04, 89.15) * mm});
            skLineSegment(sketch, "E89.MirrorCS", {"start": v(-31.04, 72.22) * mm, "end": v(-31.04, 77.87) * mm});
            skLineSegment(sketch, "E90.MirrorCS", {"start": v(-36.69, 72.22) * mm, "end": v(-36.69, 77.87) * mm});
            skLineSegment(sketch, "E91.MirrorCS", {"start": v(-36.69, 77.87) * mm, "end": v(-31.04, 77.87) * mm});
            skLineSegment(sketch, "E92.MirrorCS", {"start": v(-36.69, 72.22) * mm, "end": v(-31.04, 72.22) * mm});
            skLineSegment(sketch, "E93.MirrorCS", {"start": v(-70.56, 89.15) * mm, "end": v(-70.56, 94.8) * mm});
            skLineSegment(sketch, "E94.MirrorCS", {"start": v(-64.91, 89.15) * mm, "end": v(-64.91, 94.8) * mm});
            skLineSegment(sketch, "E95.MirrorCS", {"start": v(-64.91, 94.8) * mm, "end": v(-70.56, 94.8) * mm});
            skLineSegment(sketch, "E96.MirrorCS", {"start": v(-64.91, 72.22) * mm, "end": v(-70.56, 72.22) * mm});
            skLineSegment(sketch, "E97.MirrorCS", {"start": v(-64.91, 55.29) * mm, "end": v(-64.91, 60.93) * mm});
            skLineSegment(sketch, "E98.MirrorCS", {"start": v(-70.56, 55.29) * mm, "end": v(-70.56, 60.93) * mm});
            skLineSegment(sketch, "E99.MirrorCS", {"start": v(-70.56, 60.93) * mm, "end": v(-64.91, 60.93) * mm});
            skLineSegment(sketch, "E100.MirrorCS", {"start": v(-70.56, 55.29) * mm, "end": v(-64.91, 55.29) * mm});
            skLineSegment(sketch, "E101.MirrorCS", {"start": v(-31.04, 55.29) * mm, "end": v(-31.04, 60.93) * mm});
            skLineSegment(sketch, "E102.MirrorCS", {"start": v(-64.91, 89.15) * mm, "end": v(-70.56, 89.15) * mm});
            skLineSegment(sketch, "E103.MirrorCS", {"start": v(-36.69, 55.29) * mm, "end": v(-36.69, 60.93) * mm});
            skLineSegment(sketch, "E104.MirrorCS", {"start": v(-36.69, 60.93) * mm, "end": v(-31.04, 60.93) * mm});
            skLineSegment(sketch, "E105.MirrorCS", {"start": v(-36.69, 55.29) * mm, "end": v(-31.04, 55.29) * mm});
            skLineSegment(sketch, "E106.MirrorCS", {"start": v(-53.62, 55.29) * mm, "end": v(-53.62, 60.93) * mm});
            skLineSegment(sketch, "E107.MirrorCS", {"start": v(-47.98, 55.29) * mm, "end": v(-47.98, 60.93) * mm});
            skLineSegment(sketch, "E108.MirrorCS", {"start": v(-47.98, 60.93) * mm, "end": v(-53.62, 60.93) * mm});
            skLineSegment(sketch, "E109.MirrorCS", {"start": v(-47.98, 55.29) * mm, "end": v(-53.62, 55.29) * mm});
            skLineSegment(sketch, "E110.MirrorCS", {"start": v(-70.56, 72.22) * mm, "end": v(-70.56, 77.87) * mm});
            skLineSegment(sketch, "E111.MirrorCS", {"start": v(-64.91, 72.22) * mm, "end": v(-64.91, 77.87) * mm});
            skLineSegment(sketch, "E112.MirrorCS", {"start": v(-64.91, 77.87) * mm, "end": v(-70.56, 77.87) * mm});
            skLineSegment(sketch, "E113.MirrorCS", {"start": v(-47.98, 89.15) * mm, "end": v(-47.98, 94.8) * mm});
            skLineSegment(sketch, "E114.MirrorCS", {"start": v(-53.62, 89.15) * mm, "end": v(-47.98, 89.15) * mm});
            skLineSegment(sketch, "E115.MirrorCS", {"start": v(-36.69, 89.15) * mm, "end": v(-36.69, 94.8) * mm});
            skLineSegment(sketch, "E116.MirrorCS", {"start": v(-53.62, 94.8) * mm, "end": v(-47.98, 94.8) * mm});
            skLineSegment(sketch, "E117.MirrorCS", {"start": v(-31.04, 89.15) * mm, "end": v(-31.04, 94.8) * mm});
            skLineSegment(sketch, "E118.MirrorCS", {"start": v(-53.62, 89.15) * mm, "end": v(-53.62, 94.8) * mm});
            skPoint(sketch, "E119.MirrorP", {"position": v(-33.87, 58.1) * mm});
            skPoint(sketch, "E120.MirrorP", {"position": v(-33.87, 75.04) * mm});
            skPoint(sketch, "E121.MirrorP", {"position": v(-50.8, 58.1) * mm});
            skPoint(sketch, "E122.MirrorP", {"position": v(-67.73, 91.98) * mm});
            skPoint(sketch, "E123.MirrorP", {"position": v(-67.73, 60.93) * mm});
            skPoint(sketch, "E124.MirrorP", {"position": v(-33.87, 91.98) * mm});
            skPoint(sketch, "E125.MirrorP", {"position": v(-67.73, 58.1) * mm});
            skPoint(sketch, "E126.MirrorP", {"position": v(-50.8, 91.98) * mm});
            skPoint(sketch, "E127.MirrorP", {"position": v(-67.73, 75.04) * mm});
            skPoint(sketch, "E128.MirrorP", {"position": v(-47.98, 58.1) * mm});
            skPoint(sketch, "E129.MirrorP", {"position": v(-33.87, 60.93) * mm});
            skPoint(sketch, "E130.MirrorP", {"position": v(-42.33, 75.04) * mm});
            skPoint(sketch, "E131.MirrorP", {"position": v(-50.8, 66.58) * mm});
            skPoint(sketch, "E132.MirrorP", {"position": v(-67.73, 77.87) * mm});
            skPoint(sketch, "E133.MirrorP", {"position": v(-59.27, 75.04) * mm});
            skPoint(sketch, "E134.MirrorP", {"position": v(-53.62, 58.1) * mm});
            skPoint(sketch, "E135.MirrorP", {"position": v(-50.8, 83.5) * mm});
            skLineSegment(sketch, "E136.MirrorCS", {"start": v(-70.56, 94.8) * mm, "end": v(-19.76, 94.8) * mm, "construction": true});
            skLineSegment(sketch, "E137", {"start": v(-25.4, 76.2) * mm, "end": v(27.56, 76.2) * mm});
            skPoint(sketch, "E137.endSnap0", {"position": v(25.4, 76.2) * mm});
            skLineSegment(sketch, "E138.MirrorCS", {"start": v(19.76, 38.7) * mm, "end": v(19.76, 44.34) * mm});
            skLineSegment(sketch, "E139.MirrorCS", {"start": v(70.56, 38.7) * mm, "end": v(70.56, 44.34) * mm});
            skLineSegment(sketch, "E140.MirrorCS", {"start": v(19.76, 4.83) * mm, "end": v(19.76, 10.47) * mm});
            skLineSegment(sketch, "E141.MirrorCS", {"start": v(-36.69, 38.7) * mm, "end": v(-36.69, 44.34) * mm});
            skLineSegment(sketch, "E142.MirrorCS", {"start": v(47.98, 38.7) * mm, "end": v(53.62, 38.7) * mm});
            skLineSegment(sketch, "E143.MirrorCS", {"start": v(70.56, 4.83) * mm, "end": v(70.56, 10.47) * mm});
            skLineSegment(sketch, "E144.MirrorCS", {"start": v(-2.82, 38.7) * mm, "end": v(2.82, 38.7) * mm});
            skLineSegment(sketch, "E145.MirrorCS", {"start": v(-2.82, 4.83) * mm, "end": v(-2.82, 10.47) * mm});
            skLineSegment(sketch, "E146.MirrorCS", {"start": v(-14.11, 4.83) * mm, "end": v(-14.11, 10.47) * mm});
            skLineSegment(sketch, "E147.MirrorCS", {"start": v(-53.62, 44.34) * mm, "end": v(-47.98, 44.34) * mm});
            skLineSegment(sketch, "E148.MirrorCS", {"start": v(47.98, 4.83) * mm, "end": v(47.98, 10.47) * mm});
            skLineSegment(sketch, "E149.MirrorCS", {"start": v(36.69, 4.83) * mm, "end": v(36.69, 10.47) * mm});
            skLineSegment(sketch, "E150.MirrorCS", {"start": v(-19.76, 4.83) * mm, "end": v(-14.11, 4.83) * mm});
            skLineSegment(sketch, "E151.MirrorCS", {"start": v(-31.04, 38.7) * mm, "end": v(-31.04, 44.34) * mm});
            skLineSegment(sketch, "E152.MirrorCS", {"start": v(36.69, 27.4) * mm, "end": v(31.04, 27.4) * mm});
            skLineSegment(sketch, "E153.MirrorCS", {"start": v(31.04, 4.83) * mm, "end": v(36.69, 4.83) * mm});
            skLineSegment(sketch, "E154.MirrorCS", {"start": v(-14.11, 27.4) * mm, "end": v(-19.76, 27.4) * mm});
            skLineSegment(sketch, "E155.MirrorCS", {"start": v(14.11, 10.47) * mm, "end": v(19.76, 10.47) * mm});
            skLineSegment(sketch, "E156.MirrorCS", {"start": v(-14.11, 21.76) * mm, "end": v(-19.76, 21.76) * mm});
            skLineSegment(sketch, "E157.MirrorCS", {"start": v(-53.62, 38.7) * mm, "end": v(-53.62, 44.34) * mm});
            skLineSegment(sketch, "E158.MirrorCS", {"start": v(64.91, 10.47) * mm, "end": v(70.56, 10.47) * mm});
            skLineSegment(sketch, "E159.MirrorCS", {"start": v(-36.69, 44.34) * mm, "end": v(-31.04, 44.34) * mm});
            skLineSegment(sketch, "E160.MirrorCS", {"start": v(-14.11, 38.7) * mm, "end": v(-19.76, 38.7) * mm});
            skLineSegment(sketch, "E161.MirrorCS", {"start": v(36.69, 38.7) * mm, "end": v(31.04, 38.7) * mm});
            skLineSegment(sketch, "E162.MirrorCS", {"start": v(14.11, 38.7) * mm, "end": v(14.11, 44.34) * mm});
            skLineSegment(sketch, "E163.MirrorCS", {"start": v(64.91, 4.83) * mm, "end": v(64.91, 10.47) * mm});
            skLineSegment(sketch, "E164.MirrorCS", {"start": v(64.91, 38.7) * mm, "end": v(64.91, 44.34) * mm});
            skLineSegment(sketch, "E165.MirrorCS", {"start": v(-36.69, 38.7) * mm, "end": v(-31.04, 38.7) * mm});
            skLineSegment(sketch, "E166.MirrorCS", {"start": v(14.11, 4.83) * mm, "end": v(14.11, 10.47) * mm});
            skLineSegment(sketch, "E167.MirrorCS", {"start": v(14.11, 44.34) * mm, "end": v(19.76, 44.34) * mm});
            skLineSegment(sketch, "E168.MirrorCS", {"start": v(64.91, 4.83) * mm, "end": v(70.56, 4.83) * mm});
            skLineSegment(sketch, "E169.MirrorCS", {"start": v(64.91, 44.34) * mm, "end": v(70.56, 44.34) * mm});
            skLineSegment(sketch, "E170.MirrorCS", {"start": v(-31.04, 21.76) * mm, "end": v(-31.04, 27.4) * mm});
            skLineSegment(sketch, "E171.MirrorCS", {"start": v(14.11, 4.83) * mm, "end": v(19.76, 4.83) * mm});
            skLineSegment(sketch, "E172.MirrorCS", {"start": v(36.69, 21.76) * mm, "end": v(31.04, 21.76) * mm});
            skLineSegment(sketch, "E173.MirrorCS", {"start": v(64.91, 38.7) * mm, "end": v(70.56, 38.7) * mm});
            skLineSegment(sketch, "E174.MirrorCS", {"start": v(-36.69, 21.76) * mm, "end": v(-36.69, 27.4) * mm});
            skLineSegment(sketch, "E175.MirrorCS", {"start": v(2.82, 10.47) * mm, "end": v(-2.82, 10.47) * mm});
            skLineSegment(sketch, "E176.MirrorCS", {"start": v(14.11, 38.7) * mm, "end": v(19.76, 38.7) * mm});
            skLineSegment(sketch, "E177.MirrorCS", {"start": v(53.62, 10.47) * mm, "end": v(47.98, 10.47) * mm});
            skLineSegment(sketch, "E178.MirrorCS", {"start": v(70.56, 21.76) * mm, "end": v(70.56, 27.4) * mm});
            skLineSegment(sketch, "E179.MirrorCS", {"start": v(-36.69, 27.4) * mm, "end": v(-31.04, 27.4) * mm});
            skLineSegment(sketch, "E180.MirrorCS", {"start": v(2.82, 4.83) * mm, "end": v(-2.82, 4.83) * mm});
            skLineSegment(sketch, "E181.MirrorCS", {"start": v(19.76, 21.76) * mm, "end": v(19.76, 27.4) * mm});
            skLineSegment(sketch, "E182.MirrorCS", {"start": v(53.62, 4.83) * mm, "end": v(47.98, 4.83) * mm});
            skLineSegment(sketch, "E183.MirrorCS", {"start": v(64.91, 21.76) * mm, "end": v(64.91, 27.4) * mm});
            skLineSegment(sketch, "E184.MirrorCS", {"start": v(-36.69, 21.76) * mm, "end": v(-31.04, 21.76) * mm});
            skLineSegment(sketch, "E185.MirrorCS", {"start": v(-19.76, 21.76) * mm, "end": v(-19.76, 27.4) * mm});
            skLineSegment(sketch, "E186.MirrorCS", {"start": v(14.11, 21.76) * mm, "end": v(14.11, 27.4) * mm});
            skLineSegment(sketch, "E187.MirrorCS", {"start": v(31.04, 21.76) * mm, "end": v(31.04, 27.4) * mm});
            skLineSegment(sketch, "E188.MirrorCS", {"start": v(64.91, 27.4) * mm, "end": v(70.56, 27.4) * mm});
            skLineSegment(sketch, "E189.MirrorCS", {"start": v(-70.56, 38.7) * mm, "end": v(-70.56, 44.34) * mm});
            skLineSegment(sketch, "E190.MirrorCS", {"start": v(-14.11, 21.76) * mm, "end": v(-14.11, 27.4) * mm});
            skLineSegment(sketch, "E191.MirrorCS", {"start": v(14.11, 27.4) * mm, "end": v(19.76, 27.4) * mm});
            skLineSegment(sketch, "E192.MirrorCS", {"start": v(36.69, 21.76) * mm, "end": v(36.69, 27.4) * mm});
            skLineSegment(sketch, "E193.MirrorCS", {"start": v(64.91, 21.76) * mm, "end": v(70.56, 21.76) * mm});
            skLineSegment(sketch, "E194.MirrorCS", {"start": v(-64.91, 38.7) * mm, "end": v(-64.91, 44.34) * mm});
            skLineSegment(sketch, "E195.MirrorCS", {"start": v(2.82, 38.7) * mm, "end": v(2.82, 44.34) * mm});
            skLineSegment(sketch, "E196.MirrorCS", {"start": v(14.11, 21.76) * mm, "end": v(19.76, 21.76) * mm});
            skLineSegment(sketch, "E197.MirrorCS", {"start": v(53.62, 38.7) * mm, "end": v(53.62, 44.34) * mm});
            skLineSegment(sketch, "E198.MirrorCS", {"start": v(31.04, 38.7) * mm, "end": v(31.04, 44.34) * mm});
            skLineSegment(sketch, "E199.MirrorCS", {"start": v(-64.91, 44.34) * mm, "end": v(-70.56, 44.34) * mm});
            skLineSegment(sketch, "E200.MirrorCS", {"start": v(-2.82, 38.7) * mm, "end": v(-2.82, 44.34) * mm});
            skLineSegment(sketch, "E201.MirrorCS", {"start": v(-19.76, 38.7) * mm, "end": v(-19.76, 44.34) * mm});
            skLineSegment(sketch, "E202.MirrorCS", {"start": v(47.98, 38.7) * mm, "end": v(47.98, 44.34) * mm});
            skLineSegment(sketch, "E203.MirrorCS", {"start": v(36.69, 38.7) * mm, "end": v(36.69, 44.34) * mm});
            skLineSegment(sketch, "E204.MirrorCS", {"start": v(-64.91, 21.76) * mm, "end": v(-70.56, 21.76) * mm});
            skLineSegment(sketch, "E205.MirrorCS", {"start": v(-64.91, 4.83) * mm, "end": v(-64.91, 10.47) * mm});
            skLineSegment(sketch, "E206.MirrorCS", {"start": v(-70.56, 4.83) * mm, "end": v(-70.56, 10.47) * mm});
            skLineSegment(sketch, "E207.MirrorCS", {"start": v(-70.56, 10.47) * mm, "end": v(-64.91, 10.47) * mm});
            skLineSegment(sketch, "E208.MirrorCS", {"start": v(-70.56, 4.83) * mm, "end": v(-64.91, 4.83) * mm});
            skLineSegment(sketch, "E209.MirrorCS", {"start": v(-31.04, 4.83) * mm, "end": v(-31.04, 10.47) * mm});
            skLineSegment(sketch, "E210.MirrorCS", {"start": v(-64.91, 38.7) * mm, "end": v(-70.56, 38.7) * mm});
            skLineSegment(sketch, "E211.MirrorCS", {"start": v(-2.82, 44.34) * mm, "end": v(2.82, 44.34) * mm});
            skLineSegment(sketch, "E212.MirrorCS", {"start": v(-53.62, 4.83) * mm, "end": v(-53.62, 10.47) * mm});
            skLineSegment(sketch, "E213.MirrorCS", {"start": v(-36.69, 4.83) * mm, "end": v(-31.04, 4.83) * mm});
            skLineSegment(sketch, "E214.MirrorCS", {"start": v(47.98, 44.34) * mm, "end": v(53.62, 44.34) * mm});
            skLineSegment(sketch, "E215.MirrorCS", {"start": v(-36.69, 4.83) * mm, "end": v(-36.69, 10.47) * mm});
            skLineSegment(sketch, "E216.MirrorCS", {"start": v(-14.11, 38.7) * mm, "end": v(-14.11, 44.34) * mm});
            skLineSegment(sketch, "E217.MirrorCS", {"start": v(-19.76, 4.83) * mm, "end": v(-19.76, 10.47) * mm});
            skLineSegment(sketch, "E218.MirrorCS", {"start": v(-53.62, 38.7) * mm, "end": v(-47.98, 38.7) * mm});
            skLineSegment(sketch, "E219.MirrorCS", {"start": v(53.62, 4.83) * mm, "end": v(53.62, 10.47) * mm});
            skLineSegment(sketch, "E220.MirrorCS", {"start": v(31.04, 4.83) * mm, "end": v(31.04, 10.47) * mm});
            skLineSegment(sketch, "E221.MirrorCS", {"start": v(2.82, 4.83) * mm, "end": v(2.82, 10.47) * mm});
            skLineSegment(sketch, "E222.MirrorCS", {"start": v(-19.76, 10.47) * mm, "end": v(-14.11, 10.47) * mm});
            skLineSegment(sketch, "E223.MirrorCS", {"start": v(-14.11, 44.34) * mm, "end": v(-19.76, 44.34) * mm});
            skLineSegment(sketch, "E224.MirrorCS", {"start": v(-47.98, 38.7) * mm, "end": v(-47.98, 44.34) * mm});
            skLineSegment(sketch, "E225.MirrorCS", {"start": v(31.04, 10.47) * mm, "end": v(36.69, 10.47) * mm});
            skLineSegment(sketch, "E226.MirrorCS", {"start": v(36.69, 44.34) * mm, "end": v(31.04, 44.34) * mm});
            skLineSegment(sketch, "E227.MirrorCS", {"start": v(-64.91, 27.4) * mm, "end": v(-70.56, 27.4) * mm});
            skLineSegment(sketch, "E228.MirrorCS", {"start": v(-64.91, 21.76) * mm, "end": v(-64.91, 27.4) * mm});
            skLineSegment(sketch, "E229.MirrorCS", {"start": v(-70.56, 21.76) * mm, "end": v(-70.56, 27.4) * mm});
            skLineSegment(sketch, "E230.MirrorCS", {"start": v(-47.98, 4.83) * mm, "end": v(-53.62, 4.83) * mm});
            skLineSegment(sketch, "E231.MirrorCS", {"start": v(-47.98, 10.47) * mm, "end": v(-53.62, 10.47) * mm});
            skLineSegment(sketch, "E232.MirrorCS", {"start": v(-47.98, 4.83) * mm, "end": v(-47.98, 10.47) * mm});
            skLineSegment(sketch, "E233.MirrorCS", {"start": v(-36.69, 10.47) * mm, "end": v(-31.04, 10.47) * mm});
            skPoint(sketch, "E234.MirrorP", {"position": v(-16.93, 7.65) * mm});
            skPoint(sketch, "E235.MirrorP", {"position": v(33.87, 41.51) * mm});
            skPoint(sketch, "E236.MirrorP", {"position": v(-33.87, 7.65) * mm});
            skPoint(sketch, "E237.MirrorP", {"position": v(33.87, 24.58) * mm});
            skPoint(sketch, "E238.MirrorP", {"position": v(16.93, 7.65) * mm});
            skPoint(sketch, "E239.MirrorP", {"position": v(-33.87, 24.58) * mm});
            skPoint(sketch, "E240.MirrorP", {"position": v(50.8, 41.51) * mm});
            skPoint(sketch, "E241.MirrorP", {"position": v(-50.8, 7.65) * mm});
            skPoint(sketch, "E242.MirrorP", {"position": v(33.87, 7.65) * mm});
            skPoint(sketch, "E243.MirrorP", {"position": v(67.73, 41.51) * mm});
            skPoint(sketch, "E244.MirrorP", {"position": v(-67.73, 41.51) * mm});
            skPoint(sketch, "E245.MirrorP", {"position": v(16.93, 24.58) * mm});
            skPoint(sketch, "E246.MirrorP", {"position": v(0, 7.65) * mm});
            skPoint(sketch, "E247.MirrorP", {"position": v(67.73, 7.65) * mm});
            skPoint(sketch, "E248.MirrorP", {"position": v(-16.93, 41.51) * mm});
            skPoint(sketch, "E249.MirrorP", {"position": v(-67.73, 24.58) * mm});
            skPoint(sketch, "E250.MirrorP", {"position": v(-16.93, 24.58) * mm});
            skPoint(sketch, "E251.MirrorP", {"position": v(16.93, 41.51) * mm});
            skPoint(sketch, "E252.MirrorP", {"position": v(0, 41.51) * mm});
            skPoint(sketch, "E253.MirrorP", {"position": v(-33.87, 41.51) * mm});
            skPoint(sketch, "E254.MirrorP", {"position": v(-67.73, 7.65) * mm});
            skPoint(sketch, "E255.MirrorP", {"position": v(-50.8, 41.51) * mm});
            skPoint(sketch, "E256.MirrorP", {"position": v(50.8, 7.65) * mm});
            skPoint(sketch, "E257.MirrorP", {"position": v(67.73, 24.58) * mm});
            skPoint(sketch, "E258.MirrorP", {"position": v(-42.33, 24.58) * mm});
            skPoint(sketch, "E259.MirrorP", {"position": v(-50.8, 16.11) * mm});
            skPoint(sketch, "E260.MirrorP", {"position": v(50.8, 33.05) * mm});
            skPoint(sketch, "E261.MirrorP", {"position": v(-8.47, 24.58) * mm});
            skPoint(sketch, "E262.MirrorP", {"position": v(16.93, 10.47) * mm});
            skPoint(sketch, "E263.MirrorP", {"position": v(-33.87, 10.47) * mm});
            skPoint(sketch, "E264.MirrorP", {"position": v(-47.98, 7.65) * mm});
            skPoint(sketch, "E265.MirrorP", {"position": v(33.87, 27.4) * mm});
            skPoint(sketch, "E266.MirrorP", {"position": v(-16.93, 10.47) * mm});
            skPoint(sketch, "E267.MirrorP", {"position": v(2.82, 7.65) * mm});
            skPoint(sketch, "E268.MirrorP", {"position": v(50.8, 16.11) * mm});
            skPoint(sketch, "E269.MirrorP", {"position": v(-67.73, 27.4) * mm});
            skPoint(sketch, "E270.MirrorP", {"position": v(8.47, 24.58) * mm});
            skPoint(sketch, "E271.MirrorP", {"position": v(0, 16.11) * mm});
            skPoint(sketch, "E272.MirrorP", {"position": v(-67.73, 10.47) * mm});
            skPoint(sketch, "E273.MirrorP", {"position": v(-16.93, 27.4) * mm});
            skPoint(sketch, "E274.MirrorP", {"position": v(47.98, 7.65) * mm});
            skPoint(sketch, "E275.MirrorP", {"position": v(-59.27, 24.58) * mm});
            skPoint(sketch, "E276.MirrorP", {"position": v(53.62, 7.65) * mm});
            skPoint(sketch, "E277.MirrorP", {"position": v(-50.8, 33.05) * mm});
            skPoint(sketch, "E278.MirrorP", {"position": v(42.33, 24.58) * mm});
            skPoint(sketch, "E279.MirrorP", {"position": v(33.87, 10.47) * mm});
            skPoint(sketch, "E280.MirrorP", {"position": v(-2.82, 7.65) * mm});
            skPoint(sketch, "E281.MirrorP", {"position": v(-53.62, 7.65) * mm});
            skPoint(sketch, "E282.MirrorP", {"position": v(67.73, 10.47) * mm});
            skPoint(sketch, "E283.MirrorP", {"position": v(0, 33.05) * mm});
            skPoint(sketch, "E284.MirrorP", {"position": v(59.27, 24.58) * mm});
            skLineSegment(sketch, "E285.MirrorCS", {"start": v(-70.56, 44.34) * mm, "end": v(-19.76, 44.34) * mm, "construction": true});
            skSolve(sketch);
        }
        {
            var Q0;
            Q0 = qSketchRegion(id + "F14", true);
            extrude(context, id + "F15", {"entities" : qUnion([Q0]), "operationType" : NewBodyOperationType.REMOVE, "endBound" : BoundingType.THROUGH_ALL, "oppositeDirection" : true, "depth" : 25.4 * mm});
        }
        {
            var Q0;
            Q0=makeQuery(id+"F1.opExtrude","SWEPT_FACE",FACE,{"disambiguationData":[OSD([sQuery(id+"F0.wireOp",EDGE,"E0.right")])]});
            var sketch = newSketch(context, id + "F16", { "sketchPlane" : qUnion([Q0])});
            skLineSegment(sketch, "E286.bottom", {"start": v(-48.32, 147.84) * mm, "end": v(-53.96, 147.84) * mm});
            skLineSegment(sketch, "E286.top", {"start": v(-48.32, 142.2) * mm, "end": v(-53.96, 142.2) * mm});
            skLineSegment(sketch, "E286.left", {"start": v(-48.32, 147.84) * mm, "end": v(-48.32, 142.2) * mm});
            skLineSegment(sketch, "E286.right", {"start": v(-53.96, 147.84) * mm, "end": v(-53.96, 142.2) * mm});
            skPoint(sketch, "E286.middle", {"position": v(-51.14, 145.02) * mm});
            skPoint(sketch, "E286.middle.positionSnap0", {"position": v(-51.14, 136.55) * mm});
            skPoint(sketch, "E286.centerSnap0", {"position": v(-51.14, 136.55) * mm});
            skLineSegment(sketch, "E287.bottom", {"start": v(-37.03, 147.84) * mm, "end": v(-31.38, 147.84) * mm});
            skLineSegment(sketch, "E287.top", {"start": v(-37.03, 142.2) * mm, "end": v(-31.38, 142.2) * mm});
            skLineSegment(sketch, "E287.left", {"start": v(-37.03, 147.84) * mm, "end": v(-37.03, 142.2) * mm});
            skLineSegment(sketch, "E287.right", {"start": v(-31.38, 147.84) * mm, "end": v(-31.38, 142.2) * mm});
            skPoint(sketch, "E287.middle", {"position": v(-34.2, 145.02) * mm});
            skPoint(sketch, "E287.middle.positionSnap0", {"position": v(-48.32, 145.02) * mm});
            skPoint(sketch, "E287.centerSnap0", {"position": v(-48.32, 145.02) * mm});
            skLineSegment(sketch, "E288.bottom", {"start": v(-70.9, 147.84) * mm, "end": v(-65.25, 147.84) * mm});
            skLineSegment(sketch, "E288.top", {"start": v(-70.9, 142.2) * mm, "end": v(-65.25, 142.2) * mm});
            skLineSegment(sketch, "E288.left", {"start": v(-70.9, 147.84) * mm, "end": v(-70.9, 142.2) * mm});
            skLineSegment(sketch, "E288.right", {"start": v(-65.25, 147.84) * mm, "end": v(-65.25, 142.2) * mm});
            skPoint(sketch, "E288.middle", {"position": v(-68.07, 145.02) * mm});
            skPoint(sketch, "E288.middle.positionSnap0", {"position": v(-53.96, 145.02) * mm});
            skPoint(sketch, "E288.centerSnap0", {"position": v(-53.96, 145.02) * mm});
            skLineSegment(sketch, "E289.bottom", {"start": v(-65.25, 130.9) * mm, "end": v(-70.9, 130.9) * mm});
            skLineSegment(sketch, "E289.top", {"start": v(-65.25, 125.26) * mm, "end": v(-70.9, 125.26) * mm});
            skLineSegment(sketch, "E289.left", {"start": v(-65.25, 130.9) * mm, "end": v(-65.25, 125.26) * mm});
            skLineSegment(sketch, "E289.right", {"start": v(-70.9, 130.9) * mm, "end": v(-70.9, 125.26) * mm});
            skPoint(sketch, "E289.middle", {"position": v(-68.07, 128.08) * mm});
            skPoint(sketch, "E289.middle.positionSnap0", {"position": v(-59.6, 128.08) * mm});
            skPoint(sketch, "E289.middle.positionSnap1", {"position": v(-68.07, 142.2) * mm});
            skPoint(sketch, "E289.centerSnap0", {"position": v(-59.6, 128.08) * mm});
            skPoint(sketch, "E289.centerSnap1", {"position": v(-68.07, 142.2) * mm});
            skLineSegment(sketch, "E290.bottom", {"start": v(-65.25, 113.97) * mm, "end": v(-70.9, 113.97) * mm});
            skLineSegment(sketch, "E290.top", {"start": v(-65.25, 108.33) * mm, "end": v(-70.9, 108.33) * mm});
            skLineSegment(sketch, "E290.left", {"start": v(-65.25, 113.97) * mm, "end": v(-65.25, 108.33) * mm});
            skLineSegment(sketch, "E290.right", {"start": v(-70.9, 113.97) * mm, "end": v(-70.9, 108.33) * mm});
            skPoint(sketch, "E290.middle", {"position": v(-68.07, 111.15) * mm});
            skPoint(sketch, "E290.middle.positionSnap0", {"position": v(-68.07, 125.26) * mm});
            skPoint(sketch, "E290.centerSnap0", {"position": v(-68.07, 125.26) * mm});
            skLineSegment(sketch, "E291.bottom", {"start": v(-37.03, 130.9) * mm, "end": v(-31.38, 130.9) * mm});
            skLineSegment(sketch, "E291.top", {"start": v(-37.03, 125.26) * mm, "end": v(-31.38, 125.26) * mm});
            skLineSegment(sketch, "E291.left", {"start": v(-37.03, 130.9) * mm, "end": v(-37.03, 125.26) * mm});
            skLineSegment(sketch, "E291.right", {"start": v(-31.38, 130.9) * mm, "end": v(-31.38, 125.26) * mm});
            skPoint(sketch, "E291.middle", {"position": v(-34.2, 128.08) * mm});
            skPoint(sketch, "E291.middle.positionSnap0", {"position": v(-42.67, 128.08) * mm});
            skPoint(sketch, "E291.middle.positionSnap1", {"position": v(-34.2, 142.2) * mm});
            skPoint(sketch, "E291.centerSnap0", {"position": v(-42.67, 128.08) * mm});
            skPoint(sketch, "E291.centerSnap1", {"position": v(-34.2, 142.2) * mm});
            skLineSegment(sketch, "E292.bottom", {"start": v(-37.03, 113.97) * mm, "end": v(-31.38, 113.97) * mm});
            skLineSegment(sketch, "E292.top", {"start": v(-37.03, 108.33) * mm, "end": v(-31.38, 108.33) * mm});
            skLineSegment(sketch, "E292.left", {"start": v(-37.03, 113.97) * mm, "end": v(-37.03, 108.33) * mm});
            skLineSegment(sketch, "E292.right", {"start": v(-31.38, 113.97) * mm, "end": v(-31.38, 108.33) * mm});
            skPoint(sketch, "E292.middle", {"position": v(-34.2, 111.15) * mm});
            skLineSegment(sketch, "E293.bottom", {"start": v(-53.96, 113.97) * mm, "end": v(-48.32, 113.97) * mm});
            skLineSegment(sketch, "E293.top", {"start": v(-53.96, 108.33) * mm, "end": v(-48.32, 108.33) * mm});
            skLineSegment(sketch, "E293.left", {"start": v(-53.96, 113.97) * mm, "end": v(-53.96, 108.33) * mm});
            skLineSegment(sketch, "E293.right", {"start": v(-48.32, 113.97) * mm, "end": v(-48.32, 108.33) * mm});
            skPoint(sketch, "E293.middle", {"position": v(-51.14, 111.15) * mm});
            skPoint(sketch, "E293.middle.positionSnap0", {"position": v(-51.14, 119.62) * mm});
            skPoint(sketch, "E293.centerSnap0", {"position": v(-51.14, 119.62) * mm});
            skLineSegment(sketch, "E294.1.0.0", {"start": v(-3.16, 108.33) * mm, "end": v(2.48, 108.33) * mm});
            skPoint(sketch, "E294.1.0.1", {"position": v(-17.27, 142.2) * mm});
            skLineSegment(sketch, "E294.1.0.2", {"start": v(-3.16, 113.97) * mm, "end": v(-3.16, 108.33) * mm});
            skPoint(sketch, "E294.1.0.3", {"position": v(-17.27, 111.15) * mm});
            skLineSegment(sketch, "E294.1.0.4", {"start": v(2.48, 113.97) * mm, "end": v(2.48, 108.33) * mm});
            skPoint(sketch, "E294.1.0.5", {"position": v(-17.27, 125.26) * mm});
            skLineSegment(sketch, "E294.1.0.6", {"start": v(-14.45, 130.9) * mm, "end": v(-14.45, 125.26) * mm});
            skLineSegment(sketch, "E294.1.0.7", {"start": v(-20.1, 130.9) * mm, "end": v(-20.1, 125.26) * mm});
            skPoint(sketch, "E294.1.0.8", {"position": v(-0.34, 145.02) * mm});
            skLineSegment(sketch, "E294.1.0.9", {"start": v(2.48, 147.84) * mm, "end": v(-3.16, 147.84) * mm});
            skLineSegment(sketch, "E294.1.0.10", {"start": v(2.48, 142.2) * mm, "end": v(-3.16, 142.2) * mm});
            skLineSegment(sketch, "E294.1.0.11", {"start": v(13.77, 147.84) * mm, "end": v(19.42, 147.84) * mm});
            skLineSegment(sketch, "E294.1.0.12", {"start": v(13.77, 147.84) * mm, "end": v(13.77, 142.2) * mm});
            skLineSegment(sketch, "E294.1.0.13", {"start": v(-14.45, 113.97) * mm, "end": v(-20.1, 113.97) * mm});
            skLineSegment(sketch, "E294.1.0.14", {"start": v(19.42, 147.84) * mm, "end": v(19.42, 142.2) * mm});
            skLineSegment(sketch, "E294.1.0.15", {"start": v(-20.1, 147.84) * mm, "end": v(-14.45, 147.84) * mm});
            skLineSegment(sketch, "E294.1.0.16", {"start": v(-20.1, 147.84) * mm, "end": v(-20.1, 142.2) * mm});
            skLineSegment(sketch, "E294.1.0.17", {"start": v(-14.45, 147.84) * mm, "end": v(-14.45, 142.2) * mm});
            skLineSegment(sketch, "E294.1.0.18", {"start": v(-14.45, 130.9) * mm, "end": v(-20.1, 130.9) * mm});
            skLineSegment(sketch, "E294.1.0.19", {"start": v(-14.45, 108.33) * mm, "end": v(-20.1, 108.33) * mm});
            skPoint(sketch, "E294.1.0.20", {"position": v(16.6, 128.08) * mm});
            skLineSegment(sketch, "E294.1.0.21", {"start": v(-14.45, 113.97) * mm, "end": v(-14.45, 108.33) * mm});
            skPoint(sketch, "E294.1.0.22", {"position": v(8.13, 128.08) * mm});
            skPoint(sketch, "E294.1.0.23", {"position": v(-0.34, 136.55) * mm});
            skLineSegment(sketch, "E294.1.0.24", {"start": v(-20.1, 113.97) * mm, "end": v(-20.1, 108.33) * mm});
            skPoint(sketch, "E294.1.0.25", {"position": v(16.6, 145.02) * mm});
            skLineSegment(sketch, "E294.1.0.26", {"start": v(13.77, 130.9) * mm, "end": v(19.42, 130.9) * mm});
            skLineSegment(sketch, "E294.1.0.27", {"start": v(13.77, 125.26) * mm, "end": v(19.42, 125.26) * mm});
            skPoint(sketch, "E294.1.0.28", {"position": v(16.6, 142.2) * mm});
            skPoint(sketch, "E294.1.0.29", {"position": v(2.48, 145.02) * mm});
            skLineSegment(sketch, "E294.1.0.30", {"start": v(13.77, 130.9) * mm, "end": v(13.77, 125.26) * mm});
            skPoint(sketch, "E294.1.0.31", {"position": v(16.6, 111.15) * mm});
            skPoint(sketch, "E294.1.0.32", {"position": v(-17.27, 145.02) * mm});
            skPoint(sketch, "E294.1.0.33", {"position": v(-0.34, 111.15) * mm});
            skLineSegment(sketch, "E294.1.0.34", {"start": v(19.42, 130.9) * mm, "end": v(19.42, 125.26) * mm});
            skPoint(sketch, "E294.1.0.35", {"position": v(-3.16, 145.02) * mm});
            skLineSegment(sketch, "E294.1.0.36", {"start": v(13.77, 113.97) * mm, "end": v(19.42, 113.97) * mm});
            skPoint(sketch, "E294.1.0.37", {"position": v(-0.34, 119.62) * mm});
            skPoint(sketch, "E294.1.0.38", {"position": v(-17.27, 128.08) * mm});
            skLineSegment(sketch, "E294.1.0.39", {"start": v(13.77, 108.33) * mm, "end": v(19.42, 108.33) * mm});
            skLineSegment(sketch, "E294.1.0.40", {"start": v(13.77, 113.97) * mm, "end": v(13.77, 108.33) * mm});
            skLineSegment(sketch, "E294.1.0.41", {"start": v(19.42, 113.97) * mm, "end": v(19.42, 108.33) * mm});
            skPoint(sketch, "E294.1.0.42", {"position": v(-8.8, 128.08) * mm});
            skLineSegment(sketch, "E294.1.0.43", {"start": v(-3.16, 113.97) * mm, "end": v(2.48, 113.97) * mm});
            skPoint(sketch, "E294.1.0.44", {"position": v(-17.27, 125.26) * mm});
            skPoint(sketch, "E294.1.0.45", {"position": v(-0.34, 136.55) * mm});
            skPoint(sketch, "E294.1.0.46", {"position": v(16.6, 142.2) * mm});
            skPoint(sketch, "E294.1.0.47", {"position": v(8.13, 128.08) * mm});
            skPoint(sketch, "E294.1.0.48", {"position": v(2.48, 145.02) * mm});
            skPoint(sketch, "E294.1.0.49", {"position": v(-3.16, 145.02) * mm});
            skPoint(sketch, "E294.1.0.50", {"position": v(-0.34, 119.62) * mm});
            skPoint(sketch, "E294.1.0.51", {"position": v(-8.8, 128.08) * mm});
            skPoint(sketch, "E294.1.0.52", {"position": v(-17.27, 142.2) * mm});
            skLineSegment(sketch, "E294.1.0.53", {"start": v(-14.45, 125.26) * mm, "end": v(-20.1, 125.26) * mm});
            skLineSegment(sketch, "E294.1.0.54", {"start": v(2.48, 147.84) * mm, "end": v(2.48, 142.2) * mm});
            skLineSegment(sketch, "E294.1.0.55", {"start": v(-3.16, 147.84) * mm, "end": v(-3.16, 142.2) * mm});
            skLineSegment(sketch, "E294.1.0.56", {"start": v(13.77, 142.2) * mm, "end": v(19.42, 142.2) * mm});
            skLineSegment(sketch, "E294.1.0.57", {"start": v(-20.1, 142.2) * mm, "end": v(-14.45, 142.2) * mm});
            skLineSegment(sketch, "E294.2.0.0", {"start": v(47.64, 108.33) * mm, "end": v(53.28, 108.33) * mm});
            skPoint(sketch, "E294.2.0.1", {"position": v(33.53, 142.2) * mm});
            skLineSegment(sketch, "E294.2.0.2", {"start": v(47.64, 113.97) * mm, "end": v(47.64, 108.33) * mm});
            skPoint(sketch, "E294.2.0.3", {"position": v(33.53, 111.15) * mm});
            skLineSegment(sketch, "E294.2.0.4", {"start": v(53.28, 113.97) * mm, "end": v(53.28, 108.33) * mm});
            skPoint(sketch, "E294.2.0.5", {"position": v(33.53, 125.26) * mm});
            skLineSegment(sketch, "E294.2.0.6", {"start": v(36.35, 130.9) * mm, "end": v(36.35, 125.26) * mm});
            skLineSegment(sketch, "E294.2.0.7", {"start": v(30.7, 130.9) * mm, "end": v(30.7, 125.26) * mm});
            skPoint(sketch, "E294.2.0.8", {"position": v(50.46, 145.02) * mm});
            skLineSegment(sketch, "E294.2.0.9", {"start": v(53.28, 147.84) * mm, "end": v(47.64, 147.84) * mm});
            skLineSegment(sketch, "E294.2.0.10", {"start": v(53.28, 142.2) * mm, "end": v(47.64, 142.2) * mm});
            skLineSegment(sketch, "E294.2.0.11", {"start": v(64.57, 147.84) * mm, "end": v(70.22, 147.84) * mm});
            skLineSegment(sketch, "E294.2.0.12", {"start": v(64.57, 147.84) * mm, "end": v(64.57, 142.2) * mm});
            skLineSegment(sketch, "E294.2.0.13", {"start": v(36.35, 113.97) * mm, "end": v(30.7, 113.97) * mm});
            skLineSegment(sketch, "E294.2.0.14", {"start": v(70.22, 147.84) * mm, "end": v(70.22, 142.2) * mm});
            skLineSegment(sketch, "E294.2.0.15", {"start": v(30.7, 147.84) * mm, "end": v(36.35, 147.84) * mm});
            skLineSegment(sketch, "E294.2.0.16", {"start": v(30.7, 147.84) * mm, "end": v(30.7, 142.2) * mm});
            skLineSegment(sketch, "E294.2.0.17", {"start": v(36.35, 147.84) * mm, "end": v(36.35, 142.2) * mm});
            skLineSegment(sketch, "E294.2.0.18", {"start": v(36.35, 130.9) * mm, "end": v(30.7, 130.9) * mm});
            skLineSegment(sketch, "E294.2.0.19", {"start": v(36.35, 108.33) * mm, "end": v(30.7, 108.33) * mm});
            skPoint(sketch, "E294.2.0.20", {"position": v(67.4, 128.08) * mm});
            skLineSegment(sketch, "E294.2.0.21", {"start": v(36.35, 113.97) * mm, "end": v(36.35, 108.33) * mm});
            skPoint(sketch, "E294.2.0.22", {"position": v(58.93, 128.08) * mm});
            skPoint(sketch, "E294.2.0.23", {"position": v(50.46, 136.55) * mm});
            skLineSegment(sketch, "E294.2.0.24", {"start": v(30.7, 113.97) * mm, "end": v(30.7, 108.33) * mm});
            skPoint(sketch, "E294.2.0.25", {"position": v(67.4, 145.02) * mm});
            skLineSegment(sketch, "E294.2.0.26", {"start": v(64.57, 130.9) * mm, "end": v(70.22, 130.9) * mm});
            skLineSegment(sketch, "E294.2.0.27", {"start": v(64.57, 125.26) * mm, "end": v(70.22, 125.26) * mm});
            skPoint(sketch, "E294.2.0.28", {"position": v(67.4, 142.2) * mm});
            skPoint(sketch, "E294.2.0.29", {"position": v(53.28, 145.02) * mm});
            skLineSegment(sketch, "E294.2.0.30", {"start": v(64.57, 130.9) * mm, "end": v(64.57, 125.26) * mm});
            skPoint(sketch, "E294.2.0.31", {"position": v(67.4, 111.15) * mm});
            skPoint(sketch, "E294.2.0.32", {"position": v(33.53, 145.02) * mm});
            skPoint(sketch, "E294.2.0.33", {"position": v(50.46, 111.15) * mm});
            skLineSegment(sketch, "E294.2.0.34", {"start": v(70.22, 130.9) * mm, "end": v(70.22, 125.26) * mm});
            skPoint(sketch, "E294.2.0.35", {"position": v(47.64, 145.02) * mm});
            skLineSegment(sketch, "E294.2.0.36", {"start": v(64.57, 113.97) * mm, "end": v(70.22, 113.97) * mm});
            skPoint(sketch, "E294.2.0.37", {"position": v(50.46, 119.62) * mm});
            skPoint(sketch, "E294.2.0.38", {"position": v(33.53, 128.08) * mm});
            skLineSegment(sketch, "E294.2.0.39", {"start": v(64.57, 108.33) * mm, "end": v(70.22, 108.33) * mm});
            skLineSegment(sketch, "E294.2.0.40", {"start": v(64.57, 113.97) * mm, "end": v(64.57, 108.33) * mm});
            skLineSegment(sketch, "E294.2.0.41", {"start": v(70.22, 113.97) * mm, "end": v(70.22, 108.33) * mm});
            skPoint(sketch, "E294.2.0.42", {"position": v(42, 128.08) * mm});
            skLineSegment(sketch, "E294.2.0.43", {"start": v(47.64, 113.97) * mm, "end": v(53.28, 113.97) * mm});
            skPoint(sketch, "E294.2.0.44", {"position": v(33.53, 125.26) * mm});
            skPoint(sketch, "E294.2.0.45", {"position": v(50.46, 136.55) * mm});
            skPoint(sketch, "E294.2.0.46", {"position": v(67.4, 142.2) * mm});
            skPoint(sketch, "E294.2.0.47", {"position": v(58.93, 128.08) * mm});
            skPoint(sketch, "E294.2.0.48", {"position": v(53.28, 145.02) * mm});
            skPoint(sketch, "E294.2.0.49", {"position": v(47.64, 145.02) * mm});
            skPoint(sketch, "E294.2.0.50", {"position": v(50.46, 119.62) * mm});
            skPoint(sketch, "E294.2.0.51", {"position": v(42, 128.08) * mm});
            skPoint(sketch, "E294.2.0.52", {"position": v(33.53, 142.2) * mm});
            skLineSegment(sketch, "E294.2.0.53", {"start": v(36.35, 125.26) * mm, "end": v(30.7, 125.26) * mm});
            skLineSegment(sketch, "E294.2.0.54", {"start": v(53.28, 147.84) * mm, "end": v(53.28, 142.2) * mm});
            skLineSegment(sketch, "E294.2.0.55", {"start": v(47.64, 147.84) * mm, "end": v(47.64, 142.2) * mm});
            skLineSegment(sketch, "E294.2.0.56", {"start": v(64.57, 142.2) * mm, "end": v(70.22, 142.2) * mm});
            skLineSegment(sketch, "E294.2.0.57", {"start": v(30.7, 142.2) * mm, "end": v(36.35, 142.2) * mm});
            skLineSegment(sketch, "E294.direction1", {"start": v(-70.9, 108.33) * mm, "end": v(-20.1, 108.33) * mm, "construction": true});
            skLineSegment(sketch, "E295", {"start": v(25.06, 101.53) * mm, "end": v(75.86, 101.53) * mm});
            skLineSegment(sketch, "E296.MirrorCS", {"start": v(36.35, 90.24) * mm, "end": v(30.7, 90.24) * mm});
            skLineSegment(sketch, "E297.MirrorCS", {"start": v(70.22, 90.24) * mm, "end": v(70.22, 95.88) * mm});
            skLineSegment(sketch, "E298.MirrorCS", {"start": v(47.64, 90.24) * mm, "end": v(53.28, 90.24) * mm});
            skLineSegment(sketch, "E299.MirrorCS", {"start": v(70.22, 56.37) * mm, "end": v(70.22, 62.02) * mm});
            skLineSegment(sketch, "E300.MirrorCS", {"start": v(47.64, 56.37) * mm, "end": v(47.64, 62.02) * mm});
            skLineSegment(sketch, "E301.MirrorCS", {"start": v(36.35, 56.37) * mm, "end": v(36.35, 62.02) * mm});
            skLineSegment(sketch, "E302.MirrorCS", {"start": v(36.35, 78.95) * mm, "end": v(30.7, 78.95) * mm});
            skLineSegment(sketch, "E303.MirrorCS", {"start": v(30.7, 56.37) * mm, "end": v(36.35, 56.37) * mm});
            skLineSegment(sketch, "E304.MirrorCS", {"start": v(64.57, 62.02) * mm, "end": v(70.22, 62.02) * mm});
            skLineSegment(sketch, "E305.MirrorCS", {"start": v(36.35, 73.3) * mm, "end": v(30.7, 73.3) * mm});
            skLineSegment(sketch, "E306.MirrorCS", {"start": v(53.28, 56.37) * mm, "end": v(53.28, 62.02) * mm});
            skLineSegment(sketch, "E307.MirrorCS", {"start": v(30.7, 56.37) * mm, "end": v(30.7, 62.02) * mm});
            skLineSegment(sketch, "E308.MirrorCS", {"start": v(30.7, 62.02) * mm, "end": v(36.35, 62.02) * mm});
            skLineSegment(sketch, "E309.MirrorCS", {"start": v(36.35, 95.88) * mm, "end": v(30.7, 95.88) * mm});
            skLineSegment(sketch, "E310.MirrorCS", {"start": v(47.64, 95.88) * mm, "end": v(53.28, 95.88) * mm});
            skLineSegment(sketch, "E311.MirrorCS", {"start": v(36.35, 90.24) * mm, "end": v(36.35, 95.88) * mm});
            skLineSegment(sketch, "E312.MirrorCS", {"start": v(47.64, 90.24) * mm, "end": v(47.64, 95.88) * mm});
            skLineSegment(sketch, "E313.MirrorCS", {"start": v(30.7, 90.24) * mm, "end": v(30.7, 95.88) * mm});
            skLineSegment(sketch, "E314.MirrorCS", {"start": v(53.28, 90.24) * mm, "end": v(53.28, 95.88) * mm});
            skLineSegment(sketch, "E315.MirrorCS", {"start": v(64.57, 73.3) * mm, "end": v(70.22, 73.3) * mm});
            skLineSegment(sketch, "E316.MirrorCS", {"start": v(36.35, 73.3) * mm, "end": v(36.35, 78.95) * mm});
            skLineSegment(sketch, "E317.MirrorCS", {"start": v(64.57, 78.95) * mm, "end": v(70.22, 78.95) * mm});
            skLineSegment(sketch, "E318.MirrorCS", {"start": v(30.7, 73.3) * mm, "end": v(30.7, 78.95) * mm});
            skLineSegment(sketch, "E319.MirrorCS", {"start": v(64.57, 56.37) * mm, "end": v(64.57, 62.02) * mm});
            skLineSegment(sketch, "E320.MirrorCS", {"start": v(64.57, 90.24) * mm, "end": v(64.57, 95.88) * mm});
            skLineSegment(sketch, "E321.MirrorCS", {"start": v(64.57, 56.37) * mm, "end": v(70.22, 56.37) * mm});
            skLineSegment(sketch, "E322.MirrorCS", {"start": v(64.57, 95.88) * mm, "end": v(70.22, 95.88) * mm});
            skLineSegment(sketch, "E323.MirrorCS", {"start": v(64.57, 90.24) * mm, "end": v(70.22, 90.24) * mm});
            skLineSegment(sketch, "E324.MirrorCS", {"start": v(53.28, 62.02) * mm, "end": v(47.64, 62.02) * mm});
            skLineSegment(sketch, "E325.MirrorCS", {"start": v(70.22, 73.3) * mm, "end": v(70.22, 78.95) * mm});
            skLineSegment(sketch, "E326.MirrorCS", {"start": v(53.28, 56.37) * mm, "end": v(47.64, 56.37) * mm});
            skLineSegment(sketch, "E327.MirrorCS", {"start": v(64.57, 73.3) * mm, "end": v(64.57, 78.95) * mm});
            skPoint(sketch, "E328.MirrorP", {"position": v(50.46, 59.2) * mm});
            skPoint(sketch, "E329.MirrorP", {"position": v(67.4, 76.13) * mm});
            skPoint(sketch, "E330.MirrorP", {"position": v(67.4, 59.2) * mm});
            skPoint(sketch, "E331.MirrorP", {"position": v(67.4, 93.06) * mm});
            skPoint(sketch, "E332.MirrorP", {"position": v(33.53, 59.2) * mm});
            skPoint(sketch, "E333.MirrorP", {"position": v(33.53, 93.06) * mm});
            skPoint(sketch, "E334.MirrorP", {"position": v(33.53, 76.13) * mm});
            skPoint(sketch, "E335.MirrorP", {"position": v(50.46, 93.06) * mm});
            skPoint(sketch, "E336.MirrorP", {"position": v(50.46, 67.66) * mm});
            skPoint(sketch, "E337.MirrorP", {"position": v(33.53, 78.95) * mm});
            skPoint(sketch, "E338.MirrorP", {"position": v(67.4, 62.02) * mm});
            skPoint(sketch, "E339.MirrorP", {"position": v(53.28, 59.2) * mm});
            skPoint(sketch, "E340.MirrorP", {"position": v(58.93, 76.13) * mm});
            skPoint(sketch, "E341.MirrorP", {"position": v(47.64, 59.2) * mm});
            skPoint(sketch, "E342.MirrorP", {"position": v(50.46, 84.6) * mm});
            skPoint(sketch, "E343.MirrorP", {"position": v(42, 76.13) * mm});
            skPoint(sketch, "E344.MirrorP", {"position": v(33.53, 62.02) * mm});
            skLineSegment(sketch, "E345.MirrorCS", {"start": v(-37.03, 95.88) * mm, "end": v(-31.38, 95.88) * mm});
            skLineSegment(sketch, "E346.MirrorCS", {"start": v(-37.03, 90.24) * mm, "end": v(-31.38, 90.24) * mm});
            skLineSegment(sketch, "E347.MirrorCS", {"start": v(-31.38, 73.3) * mm, "end": v(-31.38, 78.95) * mm});
            skLineSegment(sketch, "E348.MirrorCS", {"start": v(-37.03, 73.3) * mm, "end": v(-37.03, 78.95) * mm});
            skLineSegment(sketch, "E349.MirrorCS", {"start": v(-37.03, 78.95) * mm, "end": v(-31.38, 78.95) * mm});
            skLineSegment(sketch, "E350.MirrorCS", {"start": v(-37.03, 73.3) * mm, "end": v(-31.38, 73.3) * mm});
            skLineSegment(sketch, "E351.MirrorCS", {"start": v(-70.9, 90.24) * mm, "end": v(-70.9, 95.88) * mm});
            skLineSegment(sketch, "E352.MirrorCS", {"start": v(-65.25, 90.24) * mm, "end": v(-65.25, 95.88) * mm});
            skLineSegment(sketch, "E353.MirrorCS", {"start": v(-65.25, 95.88) * mm, "end": v(-70.9, 95.88) * mm});
            skLineSegment(sketch, "E354.MirrorCS", {"start": v(-65.25, 73.3) * mm, "end": v(-70.9, 73.3) * mm});
            skLineSegment(sketch, "E355.MirrorCS", {"start": v(-65.25, 56.37) * mm, "end": v(-65.25, 62.02) * mm});
            skLineSegment(sketch, "E356.MirrorCS", {"start": v(-70.9, 56.37) * mm, "end": v(-70.9, 62.02) * mm});
            skLineSegment(sketch, "E357.MirrorCS", {"start": v(-70.9, 62.02) * mm, "end": v(-65.25, 62.02) * mm});
            skLineSegment(sketch, "E358.MirrorCS", {"start": v(-70.9, 56.37) * mm, "end": v(-65.25, 56.37) * mm});
            skLineSegment(sketch, "E359.MirrorCS", {"start": v(-31.38, 56.37) * mm, "end": v(-31.38, 62.02) * mm});
            skLineSegment(sketch, "E360.MirrorCS", {"start": v(-65.25, 90.24) * mm, "end": v(-70.9, 90.24) * mm});
            skLineSegment(sketch, "E361.MirrorCS", {"start": v(-37.03, 56.37) * mm, "end": v(-37.03, 62.02) * mm});
            skLineSegment(sketch, "E362.MirrorCS", {"start": v(-37.03, 62.02) * mm, "end": v(-31.38, 62.02) * mm});
            skLineSegment(sketch, "E363.MirrorCS", {"start": v(-37.03, 56.37) * mm, "end": v(-31.38, 56.37) * mm});
            skLineSegment(sketch, "E364.MirrorCS", {"start": v(-53.96, 56.37) * mm, "end": v(-53.96, 62.02) * mm});
            skLineSegment(sketch, "E365.MirrorCS", {"start": v(-48.32, 56.37) * mm, "end": v(-48.32, 62.02) * mm});
            skLineSegment(sketch, "E366.MirrorCS", {"start": v(-48.32, 62.02) * mm, "end": v(-53.96, 62.02) * mm});
            skLineSegment(sketch, "E367.MirrorCS", {"start": v(-48.32, 56.37) * mm, "end": v(-53.96, 56.37) * mm});
            skLineSegment(sketch, "E368.MirrorCS", {"start": v(-70.9, 73.3) * mm, "end": v(-70.9, 78.95) * mm});
            skLineSegment(sketch, "E369.MirrorCS", {"start": v(-65.25, 73.3) * mm, "end": v(-65.25, 78.95) * mm});
            skLineSegment(sketch, "E370.MirrorCS", {"start": v(-65.25, 78.95) * mm, "end": v(-70.9, 78.95) * mm});
            skLineSegment(sketch, "E371.MirrorCS", {"start": v(-48.32, 90.24) * mm, "end": v(-48.32, 95.88) * mm});
            skLineSegment(sketch, "E372.MirrorCS", {"start": v(-53.96, 90.24) * mm, "end": v(-48.32, 90.24) * mm});
            skLineSegment(sketch, "E373.MirrorCS", {"start": v(-37.03, 90.24) * mm, "end": v(-37.03, 95.88) * mm});
            skLineSegment(sketch, "E374.MirrorCS", {"start": v(-53.96, 95.88) * mm, "end": v(-48.32, 95.88) * mm});
            skLineSegment(sketch, "E375.MirrorCS", {"start": v(-31.38, 90.24) * mm, "end": v(-31.38, 95.88) * mm});
            skLineSegment(sketch, "E376.MirrorCS", {"start": v(-53.96, 90.24) * mm, "end": v(-53.96, 95.88) * mm});
            skPoint(sketch, "E377.MirrorP", {"position": v(-34.2, 59.2) * mm});
            skPoint(sketch, "E378.MirrorP", {"position": v(-34.2, 76.13) * mm});
            skPoint(sketch, "E379.MirrorP", {"position": v(-51.14, 59.2) * mm});
            skPoint(sketch, "E380.MirrorP", {"position": v(-68.07, 93.06) * mm});
            skPoint(sketch, "E381.MirrorP", {"position": v(-68.07, 62.02) * mm});
            skPoint(sketch, "E382.MirrorP", {"position": v(-34.2, 93.06) * mm});
            skPoint(sketch, "E383.MirrorP", {"position": v(-68.07, 59.2) * mm});
            skPoint(sketch, "E384.MirrorP", {"position": v(-51.14, 93.06) * mm});
            skPoint(sketch, "E385.MirrorP", {"position": v(-68.07, 76.13) * mm});
            skPoint(sketch, "E386.MirrorP", {"position": v(-48.32, 59.2) * mm});
            skPoint(sketch, "E387.MirrorP", {"position": v(-34.2, 62.02) * mm});
            skPoint(sketch, "E388.MirrorP", {"position": v(-42.67, 76.13) * mm});
            skPoint(sketch, "E389.MirrorP", {"position": v(-51.14, 67.66) * mm});
            skPoint(sketch, "E390.MirrorP", {"position": v(-68.07, 78.95) * mm});
            skPoint(sketch, "E391.MirrorP", {"position": v(-59.6, 76.13) * mm});
            skPoint(sketch, "E392.MirrorP", {"position": v(-53.96, 59.2) * mm});
            skPoint(sketch, "E393.MirrorP", {"position": v(-51.14, 84.6) * mm});
            skLineSegment(sketch, "E394.MirrorCS", {"start": v(-70.9, 95.88) * mm, "end": v(-20.1, 95.88) * mm, "construction": true});
            skLineSegment(sketch, "E395", {"start": v(-25.74, 77.28) * mm, "end": v(27.22, 77.28) * mm});
            skPoint(sketch, "E395.endSnap0", {"position": v(25.06, 77.28) * mm});
            skLineSegment(sketch, "E396.MirrorCS", {"start": v(19.42, 39.78) * mm, "end": v(19.42, 45.42) * mm});
            skLineSegment(sketch, "E397.MirrorCS", {"start": v(70.22, 39.78) * mm, "end": v(70.22, 45.42) * mm});
            skLineSegment(sketch, "E398.MirrorCS", {"start": v(19.42, 5.91) * mm, "end": v(19.42, 11.55) * mm});
            skLineSegment(sketch, "E399.MirrorCS", {"start": v(-37.03, 39.78) * mm, "end": v(-37.03, 45.42) * mm});
            skLineSegment(sketch, "E400.MirrorCS", {"start": v(47.64, 39.78) * mm, "end": v(53.28, 39.78) * mm});
            skLineSegment(sketch, "E401.MirrorCS", {"start": v(70.22, 5.91) * mm, "end": v(70.22, 11.55) * mm});
            skLineSegment(sketch, "E402.MirrorCS", {"start": v(-3.16, 39.78) * mm, "end": v(2.48, 39.78) * mm});
            skLineSegment(sketch, "E403.MirrorCS", {"start": v(-3.16, 5.91) * mm, "end": v(-3.16, 11.55) * mm});
            skLineSegment(sketch, "E404.MirrorCS", {"start": v(-14.45, 5.91) * mm, "end": v(-14.45, 11.55) * mm});
            skLineSegment(sketch, "E405.MirrorCS", {"start": v(-53.96, 45.42) * mm, "end": v(-48.32, 45.42) * mm});
            skLineSegment(sketch, "E406.MirrorCS", {"start": v(47.64, 5.91) * mm, "end": v(47.64, 11.55) * mm});
            skLineSegment(sketch, "E407.MirrorCS", {"start": v(36.35, 5.91) * mm, "end": v(36.35, 11.55) * mm});
            skLineSegment(sketch, "E408.MirrorCS", {"start": v(-20.1, 5.91) * mm, "end": v(-14.45, 5.91) * mm});
            skLineSegment(sketch, "E409.MirrorCS", {"start": v(-31.38, 39.78) * mm, "end": v(-31.38, 45.42) * mm});
            skLineSegment(sketch, "E410.MirrorCS", {"start": v(36.35, 28.49) * mm, "end": v(30.7, 28.49) * mm});
            skLineSegment(sketch, "E411.MirrorCS", {"start": v(30.7, 5.91) * mm, "end": v(36.35, 5.91) * mm});
            skLineSegment(sketch, "E412.MirrorCS", {"start": v(-14.45, 28.49) * mm, "end": v(-20.1, 28.49) * mm});
            skLineSegment(sketch, "E413.MirrorCS", {"start": v(13.77, 11.55) * mm, "end": v(19.42, 11.55) * mm});
            skLineSegment(sketch, "E414.MirrorCS", {"start": v(-14.45, 22.84) * mm, "end": v(-20.1, 22.84) * mm});
            skLineSegment(sketch, "E415.MirrorCS", {"start": v(-53.96, 39.78) * mm, "end": v(-53.96, 45.42) * mm});
            skLineSegment(sketch, "E416.MirrorCS", {"start": v(64.57, 11.55) * mm, "end": v(70.22, 11.55) * mm});
            skLineSegment(sketch, "E417.MirrorCS", {"start": v(-37.03, 45.42) * mm, "end": v(-31.38, 45.42) * mm});
            skLineSegment(sketch, "E418.MirrorCS", {"start": v(-14.45, 39.78) * mm, "end": v(-20.1, 39.78) * mm});
            skLineSegment(sketch, "E419.MirrorCS", {"start": v(36.35, 39.78) * mm, "end": v(30.7, 39.78) * mm});
            skLineSegment(sketch, "E420.MirrorCS", {"start": v(13.77, 39.78) * mm, "end": v(13.77, 45.42) * mm});
            skLineSegment(sketch, "E421.MirrorCS", {"start": v(64.57, 5.91) * mm, "end": v(64.57, 11.55) * mm});
            skLineSegment(sketch, "E422.MirrorCS", {"start": v(64.57, 39.78) * mm, "end": v(64.57, 45.42) * mm});
            skLineSegment(sketch, "E423.MirrorCS", {"start": v(-37.03, 39.78) * mm, "end": v(-31.38, 39.78) * mm});
            skLineSegment(sketch, "E424.MirrorCS", {"start": v(13.77, 5.91) * mm, "end": v(13.77, 11.55) * mm});
            skLineSegment(sketch, "E425.MirrorCS", {"start": v(13.77, 45.42) * mm, "end": v(19.42, 45.42) * mm});
            skLineSegment(sketch, "E426.MirrorCS", {"start": v(64.57, 5.91) * mm, "end": v(70.22, 5.91) * mm});
            skLineSegment(sketch, "E427.MirrorCS", {"start": v(64.57, 45.42) * mm, "end": v(70.22, 45.42) * mm});
            skLineSegment(sketch, "E428.MirrorCS", {"start": v(-31.38, 22.84) * mm, "end": v(-31.38, 28.49) * mm});
            skLineSegment(sketch, "E429.MirrorCS", {"start": v(13.77, 5.91) * mm, "end": v(19.42, 5.91) * mm});
            skLineSegment(sketch, "E430.MirrorCS", {"start": v(36.35, 22.84) * mm, "end": v(30.7, 22.84) * mm});
            skLineSegment(sketch, "E431.MirrorCS", {"start": v(64.57, 39.78) * mm, "end": v(70.22, 39.78) * mm});
            skLineSegment(sketch, "E432.MirrorCS", {"start": v(-37.03, 22.84) * mm, "end": v(-37.03, 28.49) * mm});
            skLineSegment(sketch, "E433.MirrorCS", {"start": v(2.48, 11.55) * mm, "end": v(-3.16, 11.55) * mm});
            skLineSegment(sketch, "E434.MirrorCS", {"start": v(13.77, 39.78) * mm, "end": v(19.42, 39.78) * mm});
            skLineSegment(sketch, "E435.MirrorCS", {"start": v(53.28, 11.55) * mm, "end": v(47.64, 11.55) * mm});
            skLineSegment(sketch, "E436.MirrorCS", {"start": v(70.22, 22.84) * mm, "end": v(70.22, 28.49) * mm});
            skLineSegment(sketch, "E437.MirrorCS", {"start": v(-37.03, 28.49) * mm, "end": v(-31.38, 28.49) * mm});
            skLineSegment(sketch, "E438.MirrorCS", {"start": v(2.48, 5.91) * mm, "end": v(-3.16, 5.91) * mm});
            skLineSegment(sketch, "E439.MirrorCS", {"start": v(19.42, 22.84) * mm, "end": v(19.42, 28.49) * mm});
            skLineSegment(sketch, "E440.MirrorCS", {"start": v(53.28, 5.91) * mm, "end": v(47.64, 5.91) * mm});
            skLineSegment(sketch, "E441.MirrorCS", {"start": v(64.57, 22.84) * mm, "end": v(64.57, 28.49) * mm});
            skLineSegment(sketch, "E442.MirrorCS", {"start": v(-37.03, 22.84) * mm, "end": v(-31.38, 22.84) * mm});
            skLineSegment(sketch, "E443.MirrorCS", {"start": v(-20.1, 22.84) * mm, "end": v(-20.1, 28.49) * mm});
            skLineSegment(sketch, "E444.MirrorCS", {"start": v(13.77, 22.84) * mm, "end": v(13.77, 28.49) * mm});
            skLineSegment(sketch, "E445.MirrorCS", {"start": v(30.7, 22.84) * mm, "end": v(30.7, 28.49) * mm});
            skLineSegment(sketch, "E446.MirrorCS", {"start": v(64.57, 28.49) * mm, "end": v(70.22, 28.49) * mm});
            skLineSegment(sketch, "E447.MirrorCS", {"start": v(-70.9, 39.78) * mm, "end": v(-70.9, 45.42) * mm});
            skLineSegment(sketch, "E448.MirrorCS", {"start": v(-14.45, 22.84) * mm, "end": v(-14.45, 28.49) * mm});
            skLineSegment(sketch, "E449.MirrorCS", {"start": v(13.77, 28.49) * mm, "end": v(19.42, 28.49) * mm});
            skLineSegment(sketch, "E450.MirrorCS", {"start": v(36.35, 22.84) * mm, "end": v(36.35, 28.49) * mm});
            skLineSegment(sketch, "E451.MirrorCS", {"start": v(64.57, 22.84) * mm, "end": v(70.22, 22.84) * mm});
            skLineSegment(sketch, "E452.MirrorCS", {"start": v(-65.25, 39.78) * mm, "end": v(-65.25, 45.42) * mm});
            skLineSegment(sketch, "E453.MirrorCS", {"start": v(2.48, 39.78) * mm, "end": v(2.48, 45.42) * mm});
            skLineSegment(sketch, "E454.MirrorCS", {"start": v(13.77, 22.84) * mm, "end": v(19.42, 22.84) * mm});
            skLineSegment(sketch, "E455.MirrorCS", {"start": v(53.28, 39.78) * mm, "end": v(53.28, 45.42) * mm});
            skLineSegment(sketch, "E456.MirrorCS", {"start": v(30.7, 39.78) * mm, "end": v(30.7, 45.42) * mm});
            skLineSegment(sketch, "E457.MirrorCS", {"start": v(-65.25, 45.42) * mm, "end": v(-70.9, 45.42) * mm});
            skLineSegment(sketch, "E458.MirrorCS", {"start": v(-3.16, 39.78) * mm, "end": v(-3.16, 45.42) * mm});
            skLineSegment(sketch, "E459.MirrorCS", {"start": v(-20.1, 39.78) * mm, "end": v(-20.1, 45.42) * mm});
            skLineSegment(sketch, "E460.MirrorCS", {"start": v(47.64, 39.78) * mm, "end": v(47.64, 45.42) * mm});
            skLineSegment(sketch, "E461.MirrorCS", {"start": v(36.35, 39.78) * mm, "end": v(36.35, 45.42) * mm});
            skLineSegment(sketch, "E462.MirrorCS", {"start": v(-65.25, 22.84) * mm, "end": v(-70.9, 22.84) * mm});
            skLineSegment(sketch, "E463.MirrorCS", {"start": v(-65.25, 5.91) * mm, "end": v(-65.25, 11.55) * mm});
            skLineSegment(sketch, "E464.MirrorCS", {"start": v(-70.9, 5.91) * mm, "end": v(-70.9, 11.55) * mm});
            skLineSegment(sketch, "E465.MirrorCS", {"start": v(-70.9, 11.55) * mm, "end": v(-65.25, 11.55) * mm});
            skLineSegment(sketch, "E466.MirrorCS", {"start": v(-70.9, 5.91) * mm, "end": v(-65.25, 5.91) * mm});
            skLineSegment(sketch, "E467.MirrorCS", {"start": v(-31.38, 5.91) * mm, "end": v(-31.38, 11.55) * mm});
            skLineSegment(sketch, "E468.MirrorCS", {"start": v(-65.25, 39.78) * mm, "end": v(-70.9, 39.78) * mm});
            skLineSegment(sketch, "E469.MirrorCS", {"start": v(-3.16, 45.42) * mm, "end": v(2.48, 45.42) * mm});
            skLineSegment(sketch, "E470.MirrorCS", {"start": v(-53.96, 5.91) * mm, "end": v(-53.96, 11.55) * mm});
            skLineSegment(sketch, "E471.MirrorCS", {"start": v(-37.03, 5.91) * mm, "end": v(-31.38, 5.91) * mm});
            skLineSegment(sketch, "E472.MirrorCS", {"start": v(47.64, 45.42) * mm, "end": v(53.28, 45.42) * mm});
            skLineSegment(sketch, "E473.MirrorCS", {"start": v(-37.03, 5.91) * mm, "end": v(-37.03, 11.55) * mm});
            skLineSegment(sketch, "E474.MirrorCS", {"start": v(-14.45, 39.78) * mm, "end": v(-14.45, 45.42) * mm});
            skLineSegment(sketch, "E475.MirrorCS", {"start": v(-20.1, 5.91) * mm, "end": v(-20.1, 11.55) * mm});
            skLineSegment(sketch, "E476.MirrorCS", {"start": v(-53.96, 39.78) * mm, "end": v(-48.32, 39.78) * mm});
            skLineSegment(sketch, "E477.MirrorCS", {"start": v(53.28, 5.91) * mm, "end": v(53.28, 11.55) * mm});
            skLineSegment(sketch, "E478.MirrorCS", {"start": v(30.7, 5.91) * mm, "end": v(30.7, 11.55) * mm});
            skLineSegment(sketch, "E479.MirrorCS", {"start": v(2.48, 5.91) * mm, "end": v(2.48, 11.55) * mm});
            skLineSegment(sketch, "E480.MirrorCS", {"start": v(-20.1, 11.55) * mm, "end": v(-14.45, 11.55) * mm});
            skLineSegment(sketch, "E481.MirrorCS", {"start": v(-14.45, 45.42) * mm, "end": v(-20.1, 45.42) * mm});
            skLineSegment(sketch, "E482.MirrorCS", {"start": v(-48.32, 39.78) * mm, "end": v(-48.32, 45.42) * mm});
            skLineSegment(sketch, "E483.MirrorCS", {"start": v(30.7, 11.55) * mm, "end": v(36.35, 11.55) * mm});
            skLineSegment(sketch, "E484.MirrorCS", {"start": v(36.35, 45.42) * mm, "end": v(30.7, 45.42) * mm});
            skLineSegment(sketch, "E485.MirrorCS", {"start": v(-65.25, 28.49) * mm, "end": v(-70.9, 28.49) * mm});
            skLineSegment(sketch, "E486.MirrorCS", {"start": v(-65.25, 22.84) * mm, "end": v(-65.25, 28.49) * mm});
            skLineSegment(sketch, "E487.MirrorCS", {"start": v(-70.9, 22.84) * mm, "end": v(-70.9, 28.49) * mm});
            skLineSegment(sketch, "E488.MirrorCS", {"start": v(-48.32, 5.91) * mm, "end": v(-53.96, 5.91) * mm});
            skLineSegment(sketch, "E489.MirrorCS", {"start": v(-48.32, 11.55) * mm, "end": v(-53.96, 11.55) * mm});
            skLineSegment(sketch, "E490.MirrorCS", {"start": v(-48.32, 5.91) * mm, "end": v(-48.32, 11.55) * mm});
            skLineSegment(sketch, "E491.MirrorCS", {"start": v(-37.03, 11.55) * mm, "end": v(-31.38, 11.55) * mm});
            skPoint(sketch, "E492.MirrorP", {"position": v(-17.27, 8.73) * mm});
            skPoint(sketch, "E493.MirrorP", {"position": v(33.53, 42.6) * mm});
            skPoint(sketch, "E494.MirrorP", {"position": v(-34.2, 8.73) * mm});
            skPoint(sketch, "E495.MirrorP", {"position": v(33.53, 25.67) * mm});
            skPoint(sketch, "E496.MirrorP", {"position": v(16.6, 8.73) * mm});
            skPoint(sketch, "E497.MirrorP", {"position": v(-34.2, 25.67) * mm});
            skPoint(sketch, "E498.MirrorP", {"position": v(50.46, 42.6) * mm});
            skPoint(sketch, "E499.MirrorP", {"position": v(-51.14, 8.73) * mm});
            skPoint(sketch, "E500.MirrorP", {"position": v(33.53, 8.73) * mm});
            skPoint(sketch, "E501.MirrorP", {"position": v(67.4, 42.6) * mm});
            skPoint(sketch, "E502.MirrorP", {"position": v(-68.07, 42.6) * mm});
            skPoint(sketch, "E503.MirrorP", {"position": v(16.6, 25.67) * mm});
            skPoint(sketch, "E504.MirrorP", {"position": v(-0.34, 8.73) * mm});
            skPoint(sketch, "E505.MirrorP", {"position": v(67.4, 8.73) * mm});
            skPoint(sketch, "E506.MirrorP", {"position": v(-17.27, 42.6) * mm});
            skPoint(sketch, "E507.MirrorP", {"position": v(-68.07, 25.67) * mm});
            skPoint(sketch, "E508.MirrorP", {"position": v(-17.27, 25.67) * mm});
            skPoint(sketch, "E509.MirrorP", {"position": v(16.6, 42.6) * mm});
            skPoint(sketch, "E510.MirrorP", {"position": v(-0.34, 42.6) * mm});
            skPoint(sketch, "E511.MirrorP", {"position": v(-34.2, 42.6) * mm});
            skPoint(sketch, "E512.MirrorP", {"position": v(-68.07, 8.73) * mm});
            skPoint(sketch, "E513.MirrorP", {"position": v(-51.14, 42.6) * mm});
            skPoint(sketch, "E514.MirrorP", {"position": v(50.46, 8.73) * mm});
            skPoint(sketch, "E515.MirrorP", {"position": v(67.4, 25.67) * mm});
            skPoint(sketch, "E516.MirrorP", {"position": v(-42.67, 25.67) * mm});
            skPoint(sketch, "E517.MirrorP", {"position": v(-51.14, 17.2) * mm});
            skPoint(sketch, "E518.MirrorP", {"position": v(50.46, 34.13) * mm});
            skPoint(sketch, "E519.MirrorP", {"position": v(-8.8, 25.67) * mm});
            skPoint(sketch, "E520.MirrorP", {"position": v(16.6, 11.55) * mm});
            skPoint(sketch, "E521.MirrorP", {"position": v(-34.2, 11.55) * mm});
            skPoint(sketch, "E522.MirrorP", {"position": v(-48.32, 8.73) * mm});
            skPoint(sketch, "E523.MirrorP", {"position": v(33.53, 28.49) * mm});
            skPoint(sketch, "E524.MirrorP", {"position": v(-17.27, 11.55) * mm});
            skPoint(sketch, "E525.MirrorP", {"position": v(2.48, 8.73) * mm});
            skPoint(sketch, "E526.MirrorP", {"position": v(50.46, 17.2) * mm});
            skPoint(sketch, "E527.MirrorP", {"position": v(-68.07, 28.49) * mm});
            skPoint(sketch, "E528.MirrorP", {"position": v(8.13, 25.67) * mm});
            skPoint(sketch, "E529.MirrorP", {"position": v(-0.34, 17.2) * mm});
            skPoint(sketch, "E530.MirrorP", {"position": v(-68.07, 11.55) * mm});
            skPoint(sketch, "E531.MirrorP", {"position": v(-17.27, 28.49) * mm});
            skPoint(sketch, "E532.MirrorP", {"position": v(47.64, 8.73) * mm});
            skPoint(sketch, "E533.MirrorP", {"position": v(-59.6, 25.67) * mm});
            skPoint(sketch, "E534.MirrorP", {"position": v(53.28, 8.73) * mm});
            skPoint(sketch, "E535.MirrorP", {"position": v(-51.14, 34.13) * mm});
            skPoint(sketch, "E536.MirrorP", {"position": v(42, 25.67) * mm});
            skPoint(sketch, "E537.MirrorP", {"position": v(33.53, 11.55) * mm});
            skPoint(sketch, "E538.MirrorP", {"position": v(-3.16, 8.73) * mm});
            skPoint(sketch, "E539.MirrorP", {"position": v(-53.96, 8.73) * mm});
            skPoint(sketch, "E540.MirrorP", {"position": v(67.4, 11.55) * mm});
            skPoint(sketch, "E541.MirrorP", {"position": v(-0.34, 34.13) * mm});
            skPoint(sketch, "E542.MirrorP", {"position": v(58.93, 25.67) * mm});
            skLineSegment(sketch, "E543.MirrorCS", {"start": v(-70.9, 45.42) * mm, "end": v(-20.1, 45.42) * mm, "construction": true});
            skSolve(sketch);
        }
        {
            var Q0;
            Q0 = qSketchRegion(id + "F16", true);
            extrude(context, id + "F17", {"entities" : qUnion([Q0]), "operationType" : NewBodyOperationType.REMOVE, "endBound" : BoundingType.THROUGH_ALL, "oppositeDirection" : true, "depth" : 25.4 * mm});
        }
        {
            var Q0;
            Q0=makeQuery(id+"F1.opExtrude","CAP_FACE",FACE,{"disambiguationData":[OSD([sQuery(id+"F0.wireOp",EDGE,"E0.bottom"),sQuery(id+"F0.wireOp",EDGE,"E0.top"),sQuery(id+"F0.wireOp",EDGE,"E0.left"),sQuery(id+"F0.wireOp",EDGE,"E0.right")])],"isStart":false});
            var sketch = newSketch(context, id + "F18", { "sketchPlane" : qUnion([Q0])});
            skLineSegment(sketch, "E544.bottom", {"start": v(-48.54, 71.56) * mm, "end": v(-54.18, 71.56) * mm});
            skLineSegment(sketch, "E544.top", {"start": v(-48.54, 65.91) * mm, "end": v(-54.18, 65.91) * mm});
            skLineSegment(sketch, "E544.left", {"start": v(-48.54, 71.56) * mm, "end": v(-48.54, 65.91) * mm});
            skLineSegment(sketch, "E544.right", {"start": v(-54.18, 71.56) * mm, "end": v(-54.18, 65.91) * mm});
            skPoint(sketch, "E544.middle", {"position": v(-51.36, 68.74) * mm});
            skPoint(sketch, "E544.middle.positionSnap0", {"position": v(-51.36, 60.27) * mm});
            skPoint(sketch, "E544.centerSnap0", {"position": v(-51.36, 60.27) * mm});
            skLineSegment(sketch, "E545.bottom", {"start": v(-37.25, 71.56) * mm, "end": v(-31.6, 71.56) * mm});
            skLineSegment(sketch, "E545.top", {"start": v(-37.25, 65.91) * mm, "end": v(-31.6, 65.91) * mm});
            skLineSegment(sketch, "E545.left", {"start": v(-37.25, 71.56) * mm, "end": v(-37.25, 65.91) * mm});
            skLineSegment(sketch, "E545.right", {"start": v(-31.6, 71.56) * mm, "end": v(-31.6, 65.91) * mm});
            skPoint(sketch, "E545.middle", {"position": v(-34.43, 68.74) * mm});
            skPoint(sketch, "E545.middle.positionSnap0", {"position": v(-48.54, 68.74) * mm});
            skPoint(sketch, "E545.centerSnap0", {"position": v(-48.54, 68.74) * mm});
            skLineSegment(sketch, "E546.bottom", {"start": v(-71.11, 71.56) * mm, "end": v(-65.47, 71.56) * mm});
            skLineSegment(sketch, "E546.top", {"start": v(-71.11, 65.91) * mm, "end": v(-65.47, 65.91) * mm});
            skLineSegment(sketch, "E546.left", {"start": v(-71.11, 71.56) * mm, "end": v(-71.11, 65.91) * mm});
            skLineSegment(sketch, "E546.right", {"start": v(-65.47, 71.56) * mm, "end": v(-65.47, 65.91) * mm});
            skPoint(sketch, "E546.middle", {"position": v(-68.3, 68.74) * mm});
            skPoint(sketch, "E546.middle.positionSnap0", {"position": v(-54.18, 68.74) * mm});
            skPoint(sketch, "E546.centerSnap0", {"position": v(-54.18, 68.74) * mm});
            skLineSegment(sketch, "E547.bottom", {"start": v(-65.47, 54.63) * mm, "end": v(-71.11, 54.63) * mm});
            skLineSegment(sketch, "E547.top", {"start": v(-65.47, 48.98) * mm, "end": v(-71.11, 48.98) * mm});
            skLineSegment(sketch, "E547.left", {"start": v(-65.47, 54.63) * mm, "end": v(-65.47, 48.98) * mm});
            skLineSegment(sketch, "E547.right", {"start": v(-71.11, 54.63) * mm, "end": v(-71.11, 48.98) * mm});
            skPoint(sketch, "E547.middle", {"position": v(-68.3, 51.8) * mm});
            skPoint(sketch, "E547.middle.positionSnap0", {"position": v(-59.83, 51.8) * mm});
            skPoint(sketch, "E547.middle.positionSnap1", {"position": v(-68.3, 65.91) * mm});
            skPoint(sketch, "E547.centerSnap0", {"position": v(-59.83, 51.8) * mm});
            skPoint(sketch, "E547.centerSnap1", {"position": v(-68.3, 65.91) * mm});
            skLineSegment(sketch, "E548.bottom", {"start": v(-65.47, 37.7) * mm, "end": v(-71.11, 37.7) * mm});
            skLineSegment(sketch, "E548.top", {"start": v(-65.47, 32.05) * mm, "end": v(-71.11, 32.05) * mm});
            skLineSegment(sketch, "E548.left", {"start": v(-65.47, 37.7) * mm, "end": v(-65.47, 32.05) * mm});
            skLineSegment(sketch, "E548.right", {"start": v(-71.11, 37.7) * mm, "end": v(-71.11, 32.05) * mm});
            skPoint(sketch, "E548.middle", {"position": v(-68.3, 34.87) * mm});
            skPoint(sketch, "E548.middle.positionSnap0", {"position": v(-68.3, 48.98) * mm});
            skPoint(sketch, "E548.centerSnap0", {"position": v(-68.3, 48.98) * mm});
            skLineSegment(sketch, "E549.bottom", {"start": v(-37.25, 54.63) * mm, "end": v(-31.6, 54.63) * mm});
            skLineSegment(sketch, "E549.top", {"start": v(-37.25, 48.98) * mm, "end": v(-31.6, 48.98) * mm});
            skLineSegment(sketch, "E549.left", {"start": v(-37.25, 54.63) * mm, "end": v(-37.25, 48.98) * mm});
            skLineSegment(sketch, "E549.right", {"start": v(-31.6, 54.63) * mm, "end": v(-31.6, 48.98) * mm});
            skPoint(sketch, "E549.middle", {"position": v(-34.43, 51.8) * mm});
            skPoint(sketch, "E549.middle.positionSnap0", {"position": v(-42.9, 51.8) * mm});
            skPoint(sketch, "E549.middle.positionSnap1", {"position": v(-34.43, 65.91) * mm});
            skPoint(sketch, "E549.centerSnap0", {"position": v(-42.9, 51.8) * mm});
            skPoint(sketch, "E549.centerSnap1", {"position": v(-34.43, 65.91) * mm});
            skLineSegment(sketch, "E550.bottom", {"start": v(-37.25, 37.7) * mm, "end": v(-31.6, 37.7) * mm});
            skLineSegment(sketch, "E550.top", {"start": v(-37.25, 32.05) * mm, "end": v(-31.6, 32.05) * mm});
            skLineSegment(sketch, "E550.left", {"start": v(-37.25, 37.7) * mm, "end": v(-37.25, 32.05) * mm});
            skLineSegment(sketch, "E550.right", {"start": v(-31.6, 37.7) * mm, "end": v(-31.6, 32.05) * mm});
            skPoint(sketch, "E550.middle", {"position": v(-34.43, 34.87) * mm});
            skLineSegment(sketch, "E551.bottom", {"start": v(-54.18, 37.7) * mm, "end": v(-48.54, 37.7) * mm});
            skLineSegment(sketch, "E551.top", {"start": v(-54.18, 32.05) * mm, "end": v(-48.54, 32.05) * mm});
            skLineSegment(sketch, "E551.left", {"start": v(-54.18, 37.7) * mm, "end": v(-54.18, 32.05) * mm});
            skLineSegment(sketch, "E551.right", {"start": v(-48.54, 37.7) * mm, "end": v(-48.54, 32.05) * mm});
            skPoint(sketch, "E551.middle", {"position": v(-51.36, 34.87) * mm});
            skPoint(sketch, "E551.middle.positionSnap0", {"position": v(-51.36, 43.34) * mm});
            skPoint(sketch, "E551.centerSnap0", {"position": v(-51.36, 43.34) * mm});
            skLineSegment(sketch, "E552.1.0.0", {"start": v(-3.38, 32.05) * mm, "end": v(2.26, 32.05) * mm});
            skPoint(sketch, "E552.1.0.1", {"position": v(-17.5, 65.91) * mm});
            skLineSegment(sketch, "E552.1.0.2", {"start": v(-3.38, 37.7) * mm, "end": v(-3.38, 32.05) * mm});
            skPoint(sketch, "E552.1.0.3", {"position": v(-17.5, 34.87) * mm});
            skLineSegment(sketch, "E552.1.0.4", {"start": v(2.26, 37.7) * mm, "end": v(2.26, 32.05) * mm});
            skPoint(sketch, "E552.1.0.5", {"position": v(-17.5, 48.98) * mm});
            skLineSegment(sketch, "E552.1.0.6", {"start": v(-14.67, 54.63) * mm, "end": v(-14.67, 48.98) * mm});
            skLineSegment(sketch, "E552.1.0.7", {"start": v(-20.31, 54.63) * mm, "end": v(-20.31, 48.98) * mm});
            skPoint(sketch, "E552.1.0.8", {"position": v(-0.56, 68.74) * mm});
            skLineSegment(sketch, "E552.1.0.9", {"start": v(2.26, 71.56) * mm, "end": v(-3.38, 71.56) * mm});
            skLineSegment(sketch, "E552.1.0.10", {"start": v(2.26, 65.91) * mm, "end": v(-3.38, 65.91) * mm});
            skLineSegment(sketch, "E552.1.0.11", {"start": v(13.55, 71.56) * mm, "end": v(19.2, 71.56) * mm});
            skLineSegment(sketch, "E552.1.0.12", {"start": v(13.55, 71.56) * mm, "end": v(13.55, 65.91) * mm});
            skLineSegment(sketch, "E552.1.0.13", {"start": v(-14.67, 37.7) * mm, "end": v(-20.31, 37.7) * mm});
            skLineSegment(sketch, "E552.1.0.14", {"start": v(19.2, 71.56) * mm, "end": v(19.2, 65.91) * mm});
            skLineSegment(sketch, "E552.1.0.15", {"start": v(-20.31, 71.56) * mm, "end": v(-14.67, 71.56) * mm});
            skLineSegment(sketch, "E552.1.0.16", {"start": v(-20.31, 71.56) * mm, "end": v(-20.31, 65.91) * mm});
            skLineSegment(sketch, "E552.1.0.17", {"start": v(-14.67, 71.56) * mm, "end": v(-14.67, 65.91) * mm});
            skLineSegment(sketch, "E552.1.0.18", {"start": v(-14.67, 54.63) * mm, "end": v(-20.31, 54.63) * mm});
            skLineSegment(sketch, "E552.1.0.19", {"start": v(-14.67, 32.05) * mm, "end": v(-20.31, 32.05) * mm});
            skPoint(sketch, "E552.1.0.20", {"position": v(16.37, 51.8) * mm});
            skLineSegment(sketch, "E552.1.0.21", {"start": v(-14.67, 37.7) * mm, "end": v(-14.67, 32.05) * mm});
            skPoint(sketch, "E552.1.0.22", {"position": v(7.9, 51.8) * mm});
            skPoint(sketch, "E552.1.0.23", {"position": v(-0.56, 60.27) * mm});
            skLineSegment(sketch, "E552.1.0.24", {"start": v(-20.31, 37.7) * mm, "end": v(-20.31, 32.05) * mm});
            skPoint(sketch, "E552.1.0.25", {"position": v(16.37, 68.74) * mm});
            skLineSegment(sketch, "E552.1.0.26", {"start": v(13.55, 54.63) * mm, "end": v(19.2, 54.63) * mm});
            skLineSegment(sketch, "E552.1.0.27", {"start": v(13.55, 48.98) * mm, "end": v(19.2, 48.98) * mm});
            skPoint(sketch, "E552.1.0.28", {"position": v(16.37, 65.91) * mm});
            skPoint(sketch, "E552.1.0.29", {"position": v(2.26, 68.74) * mm});
            skLineSegment(sketch, "E552.1.0.30", {"start": v(13.55, 54.63) * mm, "end": v(13.55, 48.98) * mm});
            skPoint(sketch, "E552.1.0.31", {"position": v(16.37, 34.87) * mm});
            skPoint(sketch, "E552.1.0.32", {"position": v(-17.5, 68.74) * mm});
            skPoint(sketch, "E552.1.0.33", {"position": v(-0.56, 34.87) * mm});
            skLineSegment(sketch, "E552.1.0.34", {"start": v(19.2, 54.63) * mm, "end": v(19.2, 48.98) * mm});
            skPoint(sketch, "E552.1.0.35", {"position": v(-3.38, 68.74) * mm});
            skLineSegment(sketch, "E552.1.0.36", {"start": v(13.55, 37.7) * mm, "end": v(19.2, 37.7) * mm});
            skPoint(sketch, "E552.1.0.37", {"position": v(-0.56, 43.34) * mm});
            skPoint(sketch, "E552.1.0.38", {"position": v(-17.5, 51.8) * mm});
            skLineSegment(sketch, "E552.1.0.39", {"start": v(13.55, 32.05) * mm, "end": v(19.2, 32.05) * mm});
            skLineSegment(sketch, "E552.1.0.40", {"start": v(13.55, 37.7) * mm, "end": v(13.55, 32.05) * mm});
            skLineSegment(sketch, "E552.1.0.41", {"start": v(19.2, 37.7) * mm, "end": v(19.2, 32.05) * mm});
            skPoint(sketch, "E552.1.0.42", {"position": v(-9.03, 51.8) * mm});
            skLineSegment(sketch, "E552.1.0.43", {"start": v(-3.38, 37.7) * mm, "end": v(2.26, 37.7) * mm});
            skPoint(sketch, "E552.1.0.44", {"position": v(-17.5, 48.98) * mm});
            skPoint(sketch, "E552.1.0.45", {"position": v(-0.56, 60.27) * mm});
            skPoint(sketch, "E552.1.0.46", {"position": v(16.37, 65.91) * mm});
            skPoint(sketch, "E552.1.0.47", {"position": v(7.9, 51.8) * mm});
            skPoint(sketch, "E552.1.0.48", {"position": v(2.26, 68.74) * mm});
            skPoint(sketch, "E552.1.0.49", {"position": v(-3.38, 68.74) * mm});
            skPoint(sketch, "E552.1.0.50", {"position": v(-0.56, 43.34) * mm});
            skPoint(sketch, "E552.1.0.51", {"position": v(-9.03, 51.8) * mm});
            skPoint(sketch, "E552.1.0.52", {"position": v(-17.5, 65.91) * mm});
            skLineSegment(sketch, "E552.1.0.53", {"start": v(-14.67, 48.98) * mm, "end": v(-20.31, 48.98) * mm});
            skLineSegment(sketch, "E552.1.0.54", {"start": v(2.26, 71.56) * mm, "end": v(2.26, 65.91) * mm});
            skLineSegment(sketch, "E552.1.0.55", {"start": v(-3.38, 71.56) * mm, "end": v(-3.38, 65.91) * mm});
            skLineSegment(sketch, "E552.1.0.56", {"start": v(13.55, 65.91) * mm, "end": v(19.2, 65.91) * mm});
            skLineSegment(sketch, "E552.1.0.57", {"start": v(-20.31, 65.91) * mm, "end": v(-14.67, 65.91) * mm});
            skLineSegment(sketch, "E552.2.0.0", {"start": v(47.42, 32.05) * mm, "end": v(53.06, 32.05) * mm});
            skPoint(sketch, "E552.2.0.1", {"position": v(33.3, 65.91) * mm});
            skLineSegment(sketch, "E552.2.0.2", {"start": v(47.42, 37.7) * mm, "end": v(47.42, 32.05) * mm});
            skPoint(sketch, "E552.2.0.3", {"position": v(33.3, 34.87) * mm});
            skLineSegment(sketch, "E552.2.0.4", {"start": v(53.06, 37.7) * mm, "end": v(53.06, 32.05) * mm});
            skPoint(sketch, "E552.2.0.5", {"position": v(33.3, 48.98) * mm});
            skLineSegment(sketch, "E552.2.0.6", {"start": v(36.13, 54.63) * mm, "end": v(36.13, 48.98) * mm});
            skLineSegment(sketch, "E552.2.0.7", {"start": v(30.49, 54.63) * mm, "end": v(30.49, 48.98) * mm});
            skPoint(sketch, "E552.2.0.8", {"position": v(50.24, 68.74) * mm});
            skLineSegment(sketch, "E552.2.0.9", {"start": v(53.06, 71.56) * mm, "end": v(47.42, 71.56) * mm});
            skLineSegment(sketch, "E552.2.0.10", {"start": v(53.06, 65.91) * mm, "end": v(47.42, 65.91) * mm});
            skLineSegment(sketch, "E552.2.0.11", {"start": v(64.35, 71.56) * mm, "end": v(70, 71.56) * mm});
            skLineSegment(sketch, "E552.2.0.12", {"start": v(64.35, 71.56) * mm, "end": v(64.35, 65.91) * mm});
            skLineSegment(sketch, "E552.2.0.13", {"start": v(36.13, 37.7) * mm, "end": v(30.49, 37.7) * mm});
            skLineSegment(sketch, "E552.2.0.14", {"start": v(70, 71.56) * mm, "end": v(70, 65.91) * mm});
            skLineSegment(sketch, "E552.2.0.15", {"start": v(30.49, 71.56) * mm, "end": v(36.13, 71.56) * mm});
            skLineSegment(sketch, "E552.2.0.16", {"start": v(30.49, 71.56) * mm, "end": v(30.49, 65.91) * mm});
            skLineSegment(sketch, "E552.2.0.17", {"start": v(36.13, 71.56) * mm, "end": v(36.13, 65.91) * mm});
            skLineSegment(sketch, "E552.2.0.18", {"start": v(36.13, 54.63) * mm, "end": v(30.49, 54.63) * mm});
            skLineSegment(sketch, "E552.2.0.19", {"start": v(36.13, 32.05) * mm, "end": v(30.49, 32.05) * mm});
            skPoint(sketch, "E552.2.0.20", {"position": v(67.17, 51.8) * mm});
            skLineSegment(sketch, "E552.2.0.21", {"start": v(36.13, 37.7) * mm, "end": v(36.13, 32.05) * mm});
            skPoint(sketch, "E552.2.0.22", {"position": v(58.7, 51.8) * mm});
            skPoint(sketch, "E552.2.0.23", {"position": v(50.24, 60.27) * mm});
            skLineSegment(sketch, "E552.2.0.24", {"start": v(30.49, 37.7) * mm, "end": v(30.49, 32.05) * mm});
            skPoint(sketch, "E552.2.0.25", {"position": v(67.17, 68.74) * mm});
            skLineSegment(sketch, "E552.2.0.26", {"start": v(64.35, 54.63) * mm, "end": v(70, 54.63) * mm});
            skLineSegment(sketch, "E552.2.0.27", {"start": v(64.35, 48.98) * mm, "end": v(70, 48.98) * mm});
            skPoint(sketch, "E552.2.0.28", {"position": v(67.17, 65.91) * mm});
            skPoint(sketch, "E552.2.0.29", {"position": v(53.06, 68.74) * mm});
            skLineSegment(sketch, "E552.2.0.30", {"start": v(64.35, 54.63) * mm, "end": v(64.35, 48.98) * mm});
            skPoint(sketch, "E552.2.0.31", {"position": v(67.17, 34.87) * mm});
            skPoint(sketch, "E552.2.0.32", {"position": v(33.3, 68.74) * mm});
            skPoint(sketch, "E552.2.0.33", {"position": v(50.24, 34.87) * mm});
            skLineSegment(sketch, "E552.2.0.34", {"start": v(70, 54.63) * mm, "end": v(70, 48.98) * mm});
            skPoint(sketch, "E552.2.0.35", {"position": v(47.42, 68.74) * mm});
            skLineSegment(sketch, "E552.2.0.36", {"start": v(64.35, 37.7) * mm, "end": v(70, 37.7) * mm});
            skPoint(sketch, "E552.2.0.37", {"position": v(50.24, 43.34) * mm});
            skPoint(sketch, "E552.2.0.38", {"position": v(33.3, 51.8) * mm});
            skLineSegment(sketch, "E552.2.0.39", {"start": v(64.35, 32.05) * mm, "end": v(70, 32.05) * mm});
            skLineSegment(sketch, "E552.2.0.40", {"start": v(64.35, 37.7) * mm, "end": v(64.35, 32.05) * mm});
            skLineSegment(sketch, "E552.2.0.41", {"start": v(70, 37.7) * mm, "end": v(70, 32.05) * mm});
            skPoint(sketch, "E552.2.0.42", {"position": v(41.77, 51.8) * mm});
            skLineSegment(sketch, "E552.2.0.43", {"start": v(47.42, 37.7) * mm, "end": v(53.06, 37.7) * mm});
            skPoint(sketch, "E552.2.0.44", {"position": v(33.3, 48.98) * mm});
            skPoint(sketch, "E552.2.0.45", {"position": v(50.24, 60.27) * mm});
            skPoint(sketch, "E552.2.0.46", {"position": v(67.17, 65.91) * mm});
            skPoint(sketch, "E552.2.0.47", {"position": v(58.7, 51.8) * mm});
            skPoint(sketch, "E552.2.0.48", {"position": v(53.06, 68.74) * mm});
            skPoint(sketch, "E552.2.0.49", {"position": v(47.42, 68.74) * mm});
            skPoint(sketch, "E552.2.0.50", {"position": v(50.24, 43.34) * mm});
            skPoint(sketch, "E552.2.0.51", {"position": v(41.77, 51.8) * mm});
            skPoint(sketch, "E552.2.0.52", {"position": v(33.3, 65.91) * mm});
            skLineSegment(sketch, "E552.2.0.53", {"start": v(36.13, 48.98) * mm, "end": v(30.49, 48.98) * mm});
            skLineSegment(sketch, "E552.2.0.54", {"start": v(53.06, 71.56) * mm, "end": v(53.06, 65.91) * mm});
            skLineSegment(sketch, "E552.2.0.55", {"start": v(47.42, 71.56) * mm, "end": v(47.42, 65.91) * mm});
            skLineSegment(sketch, "E552.2.0.56", {"start": v(64.35, 65.91) * mm, "end": v(70, 65.91) * mm});
            skLineSegment(sketch, "E552.2.0.57", {"start": v(30.49, 65.91) * mm, "end": v(36.13, 65.91) * mm});
            skLineSegment(sketch, "E552.direction1", {"start": v(-71.11, 32.05) * mm, "end": v(-20.31, 32.05) * mm, "construction": true});
            skLineSegment(sketch, "E553", {"start": v(24.84, 25.25) * mm, "end": v(75.64, 25.25) * mm});
            skLineSegment(sketch, "E554.MirrorCS", {"start": v(36.13, 13.96) * mm, "end": v(30.49, 13.96) * mm});
            skLineSegment(sketch, "E555.MirrorCS", {"start": v(70, 13.96) * mm, "end": v(70, 19.6) * mm});
            skLineSegment(sketch, "E556.MirrorCS", {"start": v(47.42, 13.96) * mm, "end": v(53.06, 13.96) * mm});
            skLineSegment(sketch, "E557.MirrorCS", {"start": v(70, -19.9) * mm, "end": v(70, -14.26) * mm});
            skLineSegment(sketch, "E558.MirrorCS", {"start": v(47.42, -19.9) * mm, "end": v(47.42, -14.26) * mm});
            skLineSegment(sketch, "E559.MirrorCS", {"start": v(36.13, -19.9) * mm, "end": v(36.13, -14.26) * mm});
            skLineSegment(sketch, "E560.MirrorCS", {"start": v(36.13, 2.67) * mm, "end": v(30.49, 2.67) * mm});
            skLineSegment(sketch, "E561.MirrorCS", {"start": v(30.49, -19.9) * mm, "end": v(36.13, -19.9) * mm});
            skLineSegment(sketch, "E562.MirrorCS", {"start": v(64.35, -14.26) * mm, "end": v(70, -14.26) * mm});
            skLineSegment(sketch, "E563.MirrorCS", {"start": v(36.13, -2.98) * mm, "end": v(30.49, -2.98) * mm});
            skLineSegment(sketch, "E564.MirrorCS", {"start": v(53.06, -19.9) * mm, "end": v(53.06, -14.26) * mm});
            skLineSegment(sketch, "E565.MirrorCS", {"start": v(30.49, -19.9) * mm, "end": v(30.49, -14.26) * mm});
            skLineSegment(sketch, "E566.MirrorCS", {"start": v(30.49, -14.26) * mm, "end": v(36.13, -14.26) * mm});
            skLineSegment(sketch, "E567.MirrorCS", {"start": v(36.13, 19.6) * mm, "end": v(30.49, 19.6) * mm});
            skLineSegment(sketch, "E568.MirrorCS", {"start": v(47.42, 19.6) * mm, "end": v(53.06, 19.6) * mm});
            skLineSegment(sketch, "E569.MirrorCS", {"start": v(36.13, 13.96) * mm, "end": v(36.13, 19.6) * mm});
            skLineSegment(sketch, "E570.MirrorCS", {"start": v(47.42, 13.96) * mm, "end": v(47.42, 19.6) * mm});
            skLineSegment(sketch, "E571.MirrorCS", {"start": v(30.49, 13.96) * mm, "end": v(30.49, 19.6) * mm});
            skLineSegment(sketch, "E572.MirrorCS", {"start": v(53.06, 13.96) * mm, "end": v(53.06, 19.6) * mm});
            skLineSegment(sketch, "E573.MirrorCS", {"start": v(64.35, -2.98) * mm, "end": v(70, -2.98) * mm});
            skLineSegment(sketch, "E574.MirrorCS", {"start": v(36.13, -2.98) * mm, "end": v(36.13, 2.67) * mm});
            skLineSegment(sketch, "E575.MirrorCS", {"start": v(64.35, 2.67) * mm, "end": v(70, 2.67) * mm});
            skLineSegment(sketch, "E576.MirrorCS", {"start": v(30.49, -2.98) * mm, "end": v(30.49, 2.67) * mm});
            skLineSegment(sketch, "E577.MirrorCS", {"start": v(64.35, -19.9) * mm, "end": v(64.35, -14.26) * mm});
            skLineSegment(sketch, "E578.MirrorCS", {"start": v(64.35, 13.96) * mm, "end": v(64.35, 19.6) * mm});
            skLineSegment(sketch, "E579.MirrorCS", {"start": v(64.35, -19.9) * mm, "end": v(70, -19.9) * mm});
            skLineSegment(sketch, "E580.MirrorCS", {"start": v(64.35, 19.6) * mm, "end": v(70, 19.6) * mm});
            skLineSegment(sketch, "E581.MirrorCS", {"start": v(64.35, 13.96) * mm, "end": v(70, 13.96) * mm});
            skLineSegment(sketch, "E582.MirrorCS", {"start": v(53.06, -14.26) * mm, "end": v(47.42, -14.26) * mm});
            skLineSegment(sketch, "E583.MirrorCS", {"start": v(70, -2.98) * mm, "end": v(70, 2.67) * mm});
            skLineSegment(sketch, "E584.MirrorCS", {"start": v(53.06, -19.9) * mm, "end": v(47.42, -19.9) * mm});
            skLineSegment(sketch, "E585.MirrorCS", {"start": v(64.35, -2.98) * mm, "end": v(64.35, 2.67) * mm});
            skPoint(sketch, "E586.MirrorP", {"position": v(50.24, -17.09) * mm});
            skPoint(sketch, "E587.MirrorP", {"position": v(67.17, -0.15) * mm});
            skPoint(sketch, "E588.MirrorP", {"position": v(67.17, -17.09) * mm});
            skPoint(sketch, "E589.MirrorP", {"position": v(67.17, 16.78) * mm});
            skPoint(sketch, "E590.MirrorP", {"position": v(33.3, -17.09) * mm});
            skPoint(sketch, "E591.MirrorP", {"position": v(33.3, 16.78) * mm});
            skPoint(sketch, "E592.MirrorP", {"position": v(33.3, -0.15) * mm});
            skPoint(sketch, "E593.MirrorP", {"position": v(50.24, 16.78) * mm});
            skPoint(sketch, "E594.MirrorP", {"position": v(50.24, -8.62) * mm});
            skPoint(sketch, "E595.MirrorP", {"position": v(33.3, 2.67) * mm});
            skPoint(sketch, "E596.MirrorP", {"position": v(67.17, -14.26) * mm});
            skPoint(sketch, "E597.MirrorP", {"position": v(53.06, -17.09) * mm});
            skPoint(sketch, "E598.MirrorP", {"position": v(58.7, -0.15) * mm});
            skPoint(sketch, "E599.MirrorP", {"position": v(47.42, -17.09) * mm});
            skPoint(sketch, "E600.MirrorP", {"position": v(50.24, 8.31) * mm});
            skPoint(sketch, "E601.MirrorP", {"position": v(41.77, -0.15) * mm});
            skPoint(sketch, "E602.MirrorP", {"position": v(33.3, -14.26) * mm});
            skLineSegment(sketch, "E603.MirrorCS", {"start": v(-37.25, 19.6) * mm, "end": v(-31.6, 19.6) * mm});
            skLineSegment(sketch, "E604.MirrorCS", {"start": v(-37.25, 13.96) * mm, "end": v(-31.6, 13.96) * mm});
            skLineSegment(sketch, "E605.MirrorCS", {"start": v(-31.6, -2.98) * mm, "end": v(-31.6, 2.67) * mm});
            skLineSegment(sketch, "E606.MirrorCS", {"start": v(-37.25, -2.98) * mm, "end": v(-37.25, 2.67) * mm});
            skLineSegment(sketch, "E607.MirrorCS", {"start": v(-37.25, 2.67) * mm, "end": v(-31.6, 2.67) * mm});
            skLineSegment(sketch, "E608.MirrorCS", {"start": v(-37.25, -2.98) * mm, "end": v(-31.6, -2.98) * mm});
            skLineSegment(sketch, "E609.MirrorCS", {"start": v(-71.11, 13.96) * mm, "end": v(-71.11, 19.6) * mm});
            skLineSegment(sketch, "E610.MirrorCS", {"start": v(-65.47, 13.96) * mm, "end": v(-65.47, 19.6) * mm});
            skLineSegment(sketch, "E611.MirrorCS", {"start": v(-65.47, 19.6) * mm, "end": v(-71.11, 19.6) * mm});
            skLineSegment(sketch, "E612.MirrorCS", {"start": v(-65.47, -2.98) * mm, "end": v(-71.11, -2.98) * mm});
            skLineSegment(sketch, "E613.MirrorCS", {"start": v(-65.47, -19.9) * mm, "end": v(-65.47, -14.26) * mm});
            skLineSegment(sketch, "E614.MirrorCS", {"start": v(-71.11, -19.9) * mm, "end": v(-71.11, -14.26) * mm});
            skLineSegment(sketch, "E615.MirrorCS", {"start": v(-71.11, -14.26) * mm, "end": v(-65.47, -14.26) * mm});
            skLineSegment(sketch, "E616.MirrorCS", {"start": v(-71.11, -19.9) * mm, "end": v(-65.47, -19.9) * mm});
            skLineSegment(sketch, "E617.MirrorCS", {"start": v(-31.6, -19.9) * mm, "end": v(-31.6, -14.26) * mm});
            skLineSegment(sketch, "E618.MirrorCS", {"start": v(-65.47, 13.96) * mm, "end": v(-71.11, 13.96) * mm});
            skLineSegment(sketch, "E619.MirrorCS", {"start": v(-37.25, -19.9) * mm, "end": v(-37.25, -14.26) * mm});
            skLineSegment(sketch, "E620.MirrorCS", {"start": v(-37.25, -14.26) * mm, "end": v(-31.6, -14.26) * mm});
            skLineSegment(sketch, "E621.MirrorCS", {"start": v(-37.25, -19.9) * mm, "end": v(-31.6, -19.9) * mm});
            skLineSegment(sketch, "E622.MirrorCS", {"start": v(-54.18, -19.9) * mm, "end": v(-54.18, -14.26) * mm});
            skLineSegment(sketch, "E623.MirrorCS", {"start": v(-48.54, -19.9) * mm, "end": v(-48.54, -14.26) * mm});
            skLineSegment(sketch, "E624.MirrorCS", {"start": v(-48.54, -14.26) * mm, "end": v(-54.18, -14.26) * mm});
            skLineSegment(sketch, "E625.MirrorCS", {"start": v(-48.54, -19.9) * mm, "end": v(-54.18, -19.9) * mm});
            skLineSegment(sketch, "E626.MirrorCS", {"start": v(-71.11, -2.98) * mm, "end": v(-71.11, 2.67) * mm});
            skLineSegment(sketch, "E627.MirrorCS", {"start": v(-65.47, -2.98) * mm, "end": v(-65.47, 2.67) * mm});
            skLineSegment(sketch, "E628.MirrorCS", {"start": v(-65.47, 2.67) * mm, "end": v(-71.11, 2.67) * mm});
            skLineSegment(sketch, "E629.MirrorCS", {"start": v(-48.54, 13.96) * mm, "end": v(-48.54, 19.6) * mm});
            skLineSegment(sketch, "E630.MirrorCS", {"start": v(-54.18, 13.96) * mm, "end": v(-48.54, 13.96) * mm});
            skLineSegment(sketch, "E631.MirrorCS", {"start": v(-37.25, 13.96) * mm, "end": v(-37.25, 19.6) * mm});
            skLineSegment(sketch, "E632.MirrorCS", {"start": v(-54.18, 19.6) * mm, "end": v(-48.54, 19.6) * mm});
            skLineSegment(sketch, "E633.MirrorCS", {"start": v(-31.6, 13.96) * mm, "end": v(-31.6, 19.6) * mm});
            skLineSegment(sketch, "E634.MirrorCS", {"start": v(-54.18, 13.96) * mm, "end": v(-54.18, 19.6) * mm});
            skPoint(sketch, "E635.MirrorP", {"position": v(-34.43, -17.09) * mm});
            skPoint(sketch, "E636.MirrorP", {"position": v(-34.43, -0.15) * mm});
            skPoint(sketch, "E637.MirrorP", {"position": v(-51.36, -17.09) * mm});
            skPoint(sketch, "E638.MirrorP", {"position": v(-68.3, 16.78) * mm});
            skPoint(sketch, "E639.MirrorP", {"position": v(-68.3, -14.26) * mm});
            skPoint(sketch, "E640.MirrorP", {"position": v(-34.43, 16.78) * mm});
            skPoint(sketch, "E641.MirrorP", {"position": v(-68.3, -17.09) * mm});
            skPoint(sketch, "E642.MirrorP", {"position": v(-51.36, 16.78) * mm});
            skPoint(sketch, "E643.MirrorP", {"position": v(-68.3, -0.15) * mm});
            skPoint(sketch, "E644.MirrorP", {"position": v(-48.54, -17.09) * mm});
            skPoint(sketch, "E645.MirrorP", {"position": v(-34.43, -14.26) * mm});
            skPoint(sketch, "E646.MirrorP", {"position": v(-42.9, -0.15) * mm});
            skPoint(sketch, "E647.MirrorP", {"position": v(-51.36, -8.62) * mm});
            skPoint(sketch, "E648.MirrorP", {"position": v(-68.3, 2.67) * mm});
            skPoint(sketch, "E649.MirrorP", {"position": v(-59.83, -0.15) * mm});
            skPoint(sketch, "E650.MirrorP", {"position": v(-54.18, -17.09) * mm});
            skPoint(sketch, "E651.MirrorP", {"position": v(-51.36, 8.31) * mm});
            skLineSegment(sketch, "E652.MirrorCS", {"start": v(-71.11, 19.6) * mm, "end": v(-20.31, 19.6) * mm, "construction": true});
            skLineSegment(sketch, "E653", {"start": v(-25.96, 1) * mm, "end": v(27, 1) * mm});
            skPoint(sketch, "E653.endSnap0", {"position": v(24.84, 1) * mm});
            skLineSegment(sketch, "E654.MirrorCS", {"start": v(19.2, -36.5) * mm, "end": v(19.2, -30.86) * mm});
            skLineSegment(sketch, "E655.MirrorCS", {"start": v(70, -36.5) * mm, "end": v(70, -30.86) * mm});
            skLineSegment(sketch, "E656.MirrorCS", {"start": v(19.2, -70.37) * mm, "end": v(19.2, -64.73) * mm});
            skLineSegment(sketch, "E657.MirrorCS", {"start": v(-37.25, -36.5) * mm, "end": v(-37.25, -30.86) * mm});
            skLineSegment(sketch, "E658.MirrorCS", {"start": v(47.42, -36.5) * mm, "end": v(53.06, -36.5) * mm});
            skLineSegment(sketch, "E659.MirrorCS", {"start": v(70, -70.37) * mm, "end": v(70, -64.73) * mm});
            skLineSegment(sketch, "E660.MirrorCS", {"start": v(-3.38, -36.5) * mm, "end": v(2.26, -36.5) * mm});
            skLineSegment(sketch, "E661.MirrorCS", {"start": v(-3.38, -70.37) * mm, "end": v(-3.38, -64.73) * mm});
            skLineSegment(sketch, "E662.MirrorCS", {"start": v(-14.67, -70.37) * mm, "end": v(-14.67, -64.73) * mm});
            skLineSegment(sketch, "E663.MirrorCS", {"start": v(-54.18, -30.86) * mm, "end": v(-48.54, -30.86) * mm});
            skLineSegment(sketch, "E664.MirrorCS", {"start": v(47.42, -70.37) * mm, "end": v(47.42, -64.73) * mm});
            skLineSegment(sketch, "E665.MirrorCS", {"start": v(36.13, -70.37) * mm, "end": v(36.13, -64.73) * mm});
            skLineSegment(sketch, "E666.MirrorCS", {"start": v(-20.31, -70.37) * mm, "end": v(-14.67, -70.37) * mm});
            skLineSegment(sketch, "E667.MirrorCS", {"start": v(-31.6, -36.5) * mm, "end": v(-31.6, -30.86) * mm});
            skLineSegment(sketch, "E668.MirrorCS", {"start": v(36.13, -47.8) * mm, "end": v(30.49, -47.8) * mm});
            skLineSegment(sketch, "E669.MirrorCS", {"start": v(30.49, -70.37) * mm, "end": v(36.13, -70.37) * mm});
            skLineSegment(sketch, "E670.MirrorCS", {"start": v(-14.67, -47.8) * mm, "end": v(-20.31, -47.8) * mm});
            skLineSegment(sketch, "E671.MirrorCS", {"start": v(13.55, -64.73) * mm, "end": v(19.2, -64.73) * mm});
            skLineSegment(sketch, "E672.MirrorCS", {"start": v(-14.67, -53.44) * mm, "end": v(-20.31, -53.44) * mm});
            skLineSegment(sketch, "E673.MirrorCS", {"start": v(-54.18, -36.5) * mm, "end": v(-54.18, -30.86) * mm});
            skLineSegment(sketch, "E674.MirrorCS", {"start": v(64.35, -64.73) * mm, "end": v(70, -64.73) * mm});
            skLineSegment(sketch, "E675.MirrorCS", {"start": v(-37.25, -30.86) * mm, "end": v(-31.6, -30.86) * mm});
            skLineSegment(sketch, "E676.MirrorCS", {"start": v(-14.67, -36.5) * mm, "end": v(-20.31, -36.5) * mm});
            skLineSegment(sketch, "E677.MirrorCS", {"start": v(36.13, -36.5) * mm, "end": v(30.49, -36.5) * mm});
            skLineSegment(sketch, "E678.MirrorCS", {"start": v(13.55, -36.5) * mm, "end": v(13.55, -30.86) * mm});
            skLineSegment(sketch, "E679.MirrorCS", {"start": v(64.35, -70.37) * mm, "end": v(64.35, -64.73) * mm});
            skLineSegment(sketch, "E680.MirrorCS", {"start": v(64.35, -36.5) * mm, "end": v(64.35, -30.86) * mm});
            skLineSegment(sketch, "E681.MirrorCS", {"start": v(-37.25, -36.5) * mm, "end": v(-31.6, -36.5) * mm});
            skLineSegment(sketch, "E682.MirrorCS", {"start": v(13.55, -70.37) * mm, "end": v(13.55, -64.73) * mm});
            skLineSegment(sketch, "E683.MirrorCS", {"start": v(13.55, -30.86) * mm, "end": v(19.2, -30.86) * mm});
            skLineSegment(sketch, "E684.MirrorCS", {"start": v(64.35, -70.37) * mm, "end": v(70, -70.37) * mm});
            skLineSegment(sketch, "E685.MirrorCS", {"start": v(64.35, -30.86) * mm, "end": v(70, -30.86) * mm});
            skLineSegment(sketch, "E686.MirrorCS", {"start": v(-31.6, -53.44) * mm, "end": v(-31.6, -47.8) * mm});
            skLineSegment(sketch, "E687.MirrorCS", {"start": v(13.55, -70.37) * mm, "end": v(19.2, -70.37) * mm});
            skLineSegment(sketch, "E688.MirrorCS", {"start": v(36.13, -53.44) * mm, "end": v(30.49, -53.44) * mm});
            skLineSegment(sketch, "E689.MirrorCS", {"start": v(64.35, -36.5) * mm, "end": v(70, -36.5) * mm});
            skLineSegment(sketch, "E690.MirrorCS", {"start": v(-37.25, -53.44) * mm, "end": v(-37.25, -47.8) * mm});
            skLineSegment(sketch, "E691.MirrorCS", {"start": v(2.26, -64.73) * mm, "end": v(-3.38, -64.73) * mm});
            skLineSegment(sketch, "E692.MirrorCS", {"start": v(13.55, -36.5) * mm, "end": v(19.2, -36.5) * mm});
            skLineSegment(sketch, "E693.MirrorCS", {"start": v(53.06, -64.73) * mm, "end": v(47.42, -64.73) * mm});
            skLineSegment(sketch, "E694.MirrorCS", {"start": v(70, -53.44) * mm, "end": v(70, -47.8) * mm});
            skLineSegment(sketch, "E695.MirrorCS", {"start": v(-37.25, -47.8) * mm, "end": v(-31.6, -47.8) * mm});
            skLineSegment(sketch, "E696.MirrorCS", {"start": v(2.26, -70.37) * mm, "end": v(-3.38, -70.37) * mm});
            skLineSegment(sketch, "E697.MirrorCS", {"start": v(19.2, -53.44) * mm, "end": v(19.2, -47.8) * mm});
            skLineSegment(sketch, "E698.MirrorCS", {"start": v(53.06, -70.37) * mm, "end": v(47.42, -70.37) * mm});
            skLineSegment(sketch, "E699.MirrorCS", {"start": v(64.35, -53.44) * mm, "end": v(64.35, -47.8) * mm});
            skLineSegment(sketch, "E700.MirrorCS", {"start": v(-37.25, -53.44) * mm, "end": v(-31.6, -53.44) * mm});
            skLineSegment(sketch, "E701.MirrorCS", {"start": v(-20.31, -53.44) * mm, "end": v(-20.31, -47.8) * mm});
            skLineSegment(sketch, "E702.MirrorCS", {"start": v(13.55, -53.44) * mm, "end": v(13.55, -47.8) * mm});
            skLineSegment(sketch, "E703.MirrorCS", {"start": v(30.49, -53.44) * mm, "end": v(30.49, -47.8) * mm});
            skLineSegment(sketch, "E704.MirrorCS", {"start": v(64.35, -47.8) * mm, "end": v(70, -47.8) * mm});
            skLineSegment(sketch, "E705.MirrorCS", {"start": v(-71.11, -36.5) * mm, "end": v(-71.11, -30.86) * mm});
            skLineSegment(sketch, "E706.MirrorCS", {"start": v(-14.67, -53.44) * mm, "end": v(-14.67, -47.8) * mm});
            skLineSegment(sketch, "E707.MirrorCS", {"start": v(13.55, -47.8) * mm, "end": v(19.2, -47.8) * mm});
            skLineSegment(sketch, "E708.MirrorCS", {"start": v(36.13, -53.44) * mm, "end": v(36.13, -47.8) * mm});
            skLineSegment(sketch, "E709.MirrorCS", {"start": v(64.35, -53.44) * mm, "end": v(70, -53.44) * mm});
            skLineSegment(sketch, "E710.MirrorCS", {"start": v(-65.47, -36.5) * mm, "end": v(-65.47, -30.86) * mm});
            skLineSegment(sketch, "E711.MirrorCS", {"start": v(2.26, -36.5) * mm, "end": v(2.26, -30.86) * mm});
            skLineSegment(sketch, "E712.MirrorCS", {"start": v(13.55, -53.44) * mm, "end": v(19.2, -53.44) * mm});
            skLineSegment(sketch, "E713.MirrorCS", {"start": v(53.06, -36.5) * mm, "end": v(53.06, -30.86) * mm});
            skLineSegment(sketch, "E714.MirrorCS", {"start": v(30.49, -36.5) * mm, "end": v(30.49, -30.86) * mm});
            skLineSegment(sketch, "E715.MirrorCS", {"start": v(-65.47, -30.86) * mm, "end": v(-71.11, -30.86) * mm});
            skLineSegment(sketch, "E716.MirrorCS", {"start": v(-3.38, -36.5) * mm, "end": v(-3.38, -30.86) * mm});
            skLineSegment(sketch, "E717.MirrorCS", {"start": v(-20.31, -36.5) * mm, "end": v(-20.31, -30.86) * mm});
            skLineSegment(sketch, "E718.MirrorCS", {"start": v(47.42, -36.5) * mm, "end": v(47.42, -30.86) * mm});
            skLineSegment(sketch, "E719.MirrorCS", {"start": v(36.13, -36.5) * mm, "end": v(36.13, -30.86) * mm});
            skLineSegment(sketch, "E720.MirrorCS", {"start": v(-65.47, -53.44) * mm, "end": v(-71.11, -53.44) * mm});
            skLineSegment(sketch, "E721.MirrorCS", {"start": v(-65.47, -70.37) * mm, "end": v(-65.47, -64.73) * mm});
            skLineSegment(sketch, "E722.MirrorCS", {"start": v(-71.11, -70.37) * mm, "end": v(-71.11, -64.73) * mm});
            skLineSegment(sketch, "E723.MirrorCS", {"start": v(-71.11, -64.73) * mm, "end": v(-65.47, -64.73) * mm});
            skLineSegment(sketch, "E724.MirrorCS", {"start": v(-71.11, -70.37) * mm, "end": v(-65.47, -70.37) * mm});
            skLineSegment(sketch, "E725.MirrorCS", {"start": v(-31.6, -70.37) * mm, "end": v(-31.6, -64.73) * mm});
            skLineSegment(sketch, "E726.MirrorCS", {"start": v(-65.47, -36.5) * mm, "end": v(-71.11, -36.5) * mm});
            skLineSegment(sketch, "E727.MirrorCS", {"start": v(-3.38, -30.86) * mm, "end": v(2.26, -30.86) * mm});
            skLineSegment(sketch, "E728.MirrorCS", {"start": v(-54.18, -70.37) * mm, "end": v(-54.18, -64.73) * mm});
            skLineSegment(sketch, "E729.MirrorCS", {"start": v(-37.25, -70.37) * mm, "end": v(-31.6, -70.37) * mm});
            skLineSegment(sketch, "E730.MirrorCS", {"start": v(47.42, -30.86) * mm, "end": v(53.06, -30.86) * mm});
            skLineSegment(sketch, "E731.MirrorCS", {"start": v(-37.25, -70.37) * mm, "end": v(-37.25, -64.73) * mm});
            skLineSegment(sketch, "E732.MirrorCS", {"start": v(-14.67, -36.5) * mm, "end": v(-14.67, -30.86) * mm});
            skLineSegment(sketch, "E733.MirrorCS", {"start": v(-20.31, -70.37) * mm, "end": v(-20.31, -64.73) * mm});
            skLineSegment(sketch, "E734.MirrorCS", {"start": v(-54.18, -36.5) * mm, "end": v(-48.54, -36.5) * mm});
            skLineSegment(sketch, "E735.MirrorCS", {"start": v(53.06, -70.37) * mm, "end": v(53.06, -64.73) * mm});
            skLineSegment(sketch, "E736.MirrorCS", {"start": v(30.49, -70.37) * mm, "end": v(30.49, -64.73) * mm});
            skLineSegment(sketch, "E737.MirrorCS", {"start": v(2.26, -70.37) * mm, "end": v(2.26, -64.73) * mm});
            skLineSegment(sketch, "E738.MirrorCS", {"start": v(-20.31, -64.73) * mm, "end": v(-14.67, -64.73) * mm});
            skLineSegment(sketch, "E739.MirrorCS", {"start": v(-14.67, -30.86) * mm, "end": v(-20.31, -30.86) * mm});
            skLineSegment(sketch, "E740.MirrorCS", {"start": v(-48.54, -36.5) * mm, "end": v(-48.54, -30.86) * mm});
            skLineSegment(sketch, "E741.MirrorCS", {"start": v(30.49, -64.73) * mm, "end": v(36.13, -64.73) * mm});
            skLineSegment(sketch, "E742.MirrorCS", {"start": v(36.13, -30.86) * mm, "end": v(30.49, -30.86) * mm});
            skLineSegment(sketch, "E743.MirrorCS", {"start": v(-65.47, -47.8) * mm, "end": v(-71.11, -47.8) * mm});
            skLineSegment(sketch, "E744.MirrorCS", {"start": v(-65.47, -53.44) * mm, "end": v(-65.47, -47.8) * mm});
            skLineSegment(sketch, "E745.MirrorCS", {"start": v(-71.11, -53.44) * mm, "end": v(-71.11, -47.8) * mm});
            skLineSegment(sketch, "E746.MirrorCS", {"start": v(-48.54, -70.37) * mm, "end": v(-54.18, -70.37) * mm});
            skLineSegment(sketch, "E747.MirrorCS", {"start": v(-48.54, -64.73) * mm, "end": v(-54.18, -64.73) * mm});
            skLineSegment(sketch, "E748.MirrorCS", {"start": v(-48.54, -70.37) * mm, "end": v(-48.54, -64.73) * mm});
            skLineSegment(sketch, "E749.MirrorCS", {"start": v(-37.25, -64.73) * mm, "end": v(-31.6, -64.73) * mm});
            skPoint(sketch, "E750.MirrorP", {"position": v(-17.5, -67.55) * mm});
            skPoint(sketch, "E751.MirrorP", {"position": v(33.3, -33.68) * mm});
            skPoint(sketch, "E752.MirrorP", {"position": v(-34.43, -67.55) * mm});
            skPoint(sketch, "E753.MirrorP", {"position": v(33.3, -50.61) * mm});
            skPoint(sketch, "E754.MirrorP", {"position": v(16.37, -67.55) * mm});
            skPoint(sketch, "E755.MirrorP", {"position": v(-34.43, -50.61) * mm});
            skPoint(sketch, "E756.MirrorP", {"position": v(50.24, -33.68) * mm});
            skPoint(sketch, "E757.MirrorP", {"position": v(-51.36, -67.55) * mm});
            skPoint(sketch, "E758.MirrorP", {"position": v(33.3, -67.55) * mm});
            skPoint(sketch, "E759.MirrorP", {"position": v(67.17, -33.68) * mm});
            skPoint(sketch, "E760.MirrorP", {"position": v(-68.3, -33.68) * mm});
            skPoint(sketch, "E761.MirrorP", {"position": v(16.37, -50.61) * mm});
            skPoint(sketch, "E762.MirrorP", {"position": v(-0.56, -67.55) * mm});
            skPoint(sketch, "E763.MirrorP", {"position": v(67.17, -67.55) * mm});
            skPoint(sketch, "E764.MirrorP", {"position": v(-17.5, -33.68) * mm});
            skPoint(sketch, "E765.MirrorP", {"position": v(-68.3, -50.61) * mm});
            skPoint(sketch, "E766.MirrorP", {"position": v(-17.5, -50.61) * mm});
            skPoint(sketch, "E767.MirrorP", {"position": v(16.37, -33.68) * mm});
            skPoint(sketch, "E768.MirrorP", {"position": v(-0.56, -33.68) * mm});
            skPoint(sketch, "E769.MirrorP", {"position": v(-34.43, -33.68) * mm});
            skPoint(sketch, "E770.MirrorP", {"position": v(-68.3, -67.55) * mm});
            skPoint(sketch, "E771.MirrorP", {"position": v(-51.36, -33.68) * mm});
            skPoint(sketch, "E772.MirrorP", {"position": v(50.24, -67.55) * mm});
            skPoint(sketch, "E773.MirrorP", {"position": v(67.17, -50.61) * mm});
            skPoint(sketch, "E774.MirrorP", {"position": v(-42.9, -50.61) * mm});
            skPoint(sketch, "E775.MirrorP", {"position": v(-51.36, -59.08) * mm});
            skPoint(sketch, "E776.MirrorP", {"position": v(50.24, -42.15) * mm});
            skPoint(sketch, "E777.MirrorP", {"position": v(-9.03, -50.61) * mm});
            skPoint(sketch, "E778.MirrorP", {"position": v(16.37, -64.73) * mm});
            skPoint(sketch, "E779.MirrorP", {"position": v(-34.43, -64.73) * mm});
            skPoint(sketch, "E780.MirrorP", {"position": v(-48.54, -67.55) * mm});
            skPoint(sketch, "E781.MirrorP", {"position": v(33.3, -47.8) * mm});
            skPoint(sketch, "E782.MirrorP", {"position": v(-17.5, -64.73) * mm});
            skPoint(sketch, "E783.MirrorP", {"position": v(2.26, -67.55) * mm});
            skPoint(sketch, "E784.MirrorP", {"position": v(50.24, -59.08) * mm});
            skPoint(sketch, "E785.MirrorP", {"position": v(-68.3, -47.8) * mm});
            skPoint(sketch, "E786.MirrorP", {"position": v(7.9, -50.61) * mm});
            skPoint(sketch, "E787.MirrorP", {"position": v(-0.56, -59.08) * mm});
            skPoint(sketch, "E788.MirrorP", {"position": v(-68.3, -64.73) * mm});
            skPoint(sketch, "E789.MirrorP", {"position": v(-17.5, -47.8) * mm});
            skPoint(sketch, "E790.MirrorP", {"position": v(47.42, -67.55) * mm});
            skPoint(sketch, "E791.MirrorP", {"position": v(-59.83, -50.61) * mm});
            skPoint(sketch, "E792.MirrorP", {"position": v(53.06, -67.55) * mm});
            skPoint(sketch, "E793.MirrorP", {"position": v(-51.36, -42.15) * mm});
            skPoint(sketch, "E794.MirrorP", {"position": v(41.77, -50.61) * mm});
            skPoint(sketch, "E795.MirrorP", {"position": v(33.3, -64.73) * mm});
            skPoint(sketch, "E796.MirrorP", {"position": v(-3.38, -67.55) * mm});
            skPoint(sketch, "E797.MirrorP", {"position": v(-54.18, -67.55) * mm});
            skPoint(sketch, "E798.MirrorP", {"position": v(67.17, -64.73) * mm});
            skPoint(sketch, "E799.MirrorP", {"position": v(-0.56, -42.15) * mm});
            skPoint(sketch, "E800.MirrorP", {"position": v(58.7, -50.61) * mm});
            skLineSegment(sketch, "E801.MirrorCS", {"start": v(-71.11, -30.86) * mm, "end": v(-20.31, -30.86) * mm, "construction": true});
            skSolve(sketch);
        }
        {
            var Q0;
            Q0 = qSketchRegion(id + "F18", true);
            extrude(context, id + "F19", {"entities" : qUnion([Q0]), "operationType" : NewBodyOperationType.REMOVE, "endBound" : BoundingType.THROUGH_ALL, "oppositeDirection" : true, "depth" : 25.4 * mm});
        }
        {
            var Q0;
            Q0=makeQuery(id+"F1.opExtrude","SWEPT_FACE",FACE,{"disambiguationData":[OSD([sQuery(id+"F0.wireOp",EDGE,"E0.top")])]});
            var sketch = newSketch(context, id + "F20", { "sketchPlane" : qUnion([Q0])});
            skLineSegment(sketch, "E802", {"start": v(-59.27, 135.47) * mm, "end": v(-59.27, 152.4) * mm});
            skLineSegment(sketch, "E803", {"start": v(-42.33, 135.47) * mm, "end": v(-42.33, 152.4) * mm});
            skLineSegment(sketch, "E804", {"start": v(-25.4, 101.6) * mm, "end": v(-25.4, 152.4) * mm});
            skLineSegment(sketch, "E805", {"start": v(-25.4, 101.6) * mm, "end": v(-76.2, 101.6) * mm});
            skLineSegment(sketch, "E806", {"start": v(-59.27, 118.53) * mm, "end": v(-76.2, 118.53) * mm});
            skLineSegment(sketch, "E807", {"start": v(-59.27, 118.53) * mm, "end": v(-59.27, 101.6) * mm});
            skLineSegment(sketch, "E808", {"start": v(-42.33, 118.53) * mm, "end": v(-42.33, 101.6) * mm});
            skLineSegment(sketch, "E809", {"start": v(-42.33, 118.53) * mm, "end": v(-25.4, 118.53) * mm});
            skLineSegment(sketch, "E810", {"start": v(-42.33, 135.47) * mm, "end": v(-25.4, 135.47) * mm});
            skLineSegment(sketch, "E811", {"start": v(-59.27, 135.47) * mm, "end": v(-76.2, 135.47) * mm});
            skLineSegment(sketch, "E812", {"start": v(-47.98, 141.11) * mm, "end": v(-47.98, 135.47) * mm});
            skLineSegment(sketch, "E813", {"start": v(-53.62, 141.11) * mm, "end": v(-53.62, 135.47) * mm});
            skLineSegment(sketch, "E814", {"start": v(-53.62, 141.11) * mm, "end": v(-59.27, 141.11) * mm});
            skLineSegment(sketch, "E815", {"start": v(-53.62, 146.76) * mm, "end": v(-59.27, 146.76) * mm});
            skLineSegment(sketch, "E816", {"start": v(-53.62, 146.76) * mm, "end": v(-53.62, 152.4) * mm});
            skLineSegment(sketch, "E817", {"start": v(-47.98, 146.76) * mm, "end": v(-47.98, 152.4) * mm});
            skLineSegment(sketch, "E818", {"start": v(-47.98, 146.76) * mm, "end": v(-42.33, 146.76) * mm});
            skLineSegment(sketch, "E819", {"start": v(-47.98, 141.11) * mm, "end": v(-42.33, 141.11) * mm});
            skLineSegment(sketch, "E820", {"start": v(-57.39, 141.11) * mm, "end": v(-57.39, 135.47) * mm});
            skLineSegment(sketch, "E821", {"start": v(-55.5, 141.11) * mm, "end": v(-55.5, 135.47) * mm});
            skLineSegment(sketch, "E822", {"start": v(-59.27, 139.23) * mm, "end": v(-53.62, 139.23) * mm});
            skLineSegment(sketch, "E823", {"start": v(-59.27, 137.35) * mm, "end": v(-53.62, 137.35) * mm});
            skLineSegment(sketch, "E824", {"start": v(-57.39, 141.11) * mm, "end": v(-57.39, 152.4) * mm});
            skLineSegment(sketch, "E825", {"start": v(-55.5, 141.11) * mm, "end": v(-55.5, 152.4) * mm});
            skLineSegment(sketch, "E826", {"start": v(-53.62, 137.35) * mm, "end": v(-42.33, 137.35) * mm});
            skLineSegment(sketch, "E827.MirrorCS", {"start": v(-51.74, 141.11) * mm, "end": v(-51.74, 135.47) * mm});
            skLineSegment(sketch, "E828.MirrorCS", {"start": v(-49.86, 141.11) * mm, "end": v(-49.86, 135.47) * mm});
            skPoint(sketch, "E829.MirrorCS.start.orphan", {"position": v(-47.98, 139.23) * mm});
            skPoint(sketch, "E830.trimOffspring.end.orphan", {"position": v(-53.62, 139.23) * mm});
            skLineSegment(sketch, "E831", {"start": v(-53.62, 139.23) * mm, "end": v(-47.98, 139.23) * mm});
            skPoint(sketch, "E832.trimOffspring.end.orphan", {"position": v(-42.33, 139.23) * mm});
            skLineSegment(sketch, "E833", {"start": v(-47.98, 139.23) * mm, "end": v(-42.33, 139.23) * mm});
            skLineSegment(sketch, "E834.MirrorCS", {"start": v(-46.1, 141.11) * mm, "end": v(-46.1, 135.47) * mm});
            skLineSegment(sketch, "E835.MirrorCS", {"start": v(-44.22, 141.11) * mm, "end": v(-44.22, 135.47) * mm});
            skLineSegment(sketch, "E836", {"start": v(-46.1, 141.11) * mm, "end": v(-46.1, 152.4) * mm});
            skLineSegment(sketch, "E837", {"start": v(-44.22, 141.11) * mm, "end": v(-44.22, 152.4) * mm});
            skLineSegment(sketch, "E838.MirrorCS", {"start": v(-47.98, 143) * mm, "end": v(-42.33, 143) * mm});
            skPoint(sketch, "E839.orphan", {"position": v(-53.62, 144.87) * mm});
            skPoint(sketch, "E840.MirrorCS.end.orphan", {"position": v(-42.33, 144.87) * mm});
            skLineSegment(sketch, "E841", {"start": v(-42.33, 144.87) * mm, "end": v(-47.98, 144.87) * mm});
            skLineSegment(sketch, "E842.MirrorCS", {"start": v(-42.33, 148.64) * mm, "end": v(-47.98, 148.64) * mm});
            skLineSegment(sketch, "E843.MirrorCS", {"start": v(-47.98, 150.52) * mm, "end": v(-42.33, 150.52) * mm});
            skLineSegment(sketch, "E844.MirrorCS", {"start": v(-59.27, 143) * mm, "end": v(-53.62, 143) * mm});
            skLineSegment(sketch, "E845.MirrorCS", {"start": v(-59.27, 144.87) * mm, "end": v(-53.62, 144.87) * mm});
            skLineSegment(sketch, "E846.MirrorCS", {"start": v(-59.27, 150.52) * mm, "end": v(-53.62, 150.52) * mm});
            skPoint(sketch, "E847.trimOffspring.end.orphan", {"position": v(-53.62, 148.64) * mm});
            skPoint(sketch, "E848.MirrorCS.start.orphan", {"position": v(-59.27, 148.64) * mm});
            skLineSegment(sketch, "E849", {"start": v(-53.62, 148.64) * mm, "end": v(-59.27, 148.64) * mm});
            skLineSegment(sketch, "E850", {"start": v(-53.62, 150.52) * mm, "end": v(-47.98, 150.52) * mm});
            skLineSegment(sketch, "E851", {"start": v(-47.98, 148.64) * mm, "end": v(-53.62, 148.64) * mm});
            skLineSegment(sketch, "E852", {"start": v(-51.74, 152.4) * mm, "end": v(-51.74, 146.76) * mm});
            skLineSegment(sketch, "E853", {"start": v(-49.86, 146.76) * mm, "end": v(-49.86, 152.4) * mm});
            skLineSegment(sketch, "E854.MirrorCS", {"start": v(-42.33, 148.64) * mm, "end": v(-36.69, 148.64) * mm});
            skLineSegment(sketch, "E855.MirrorCS", {"start": v(-36.69, 150.52) * mm, "end": v(-42.33, 150.52) * mm});
            skLineSegment(sketch, "E856.MirrorCS", {"start": v(-40.45, 141.11) * mm, "end": v(-40.45, 152.4) * mm});
            skLineSegment(sketch, "E857.MirrorCS", {"start": v(-38.57, 141.11) * mm, "end": v(-38.57, 152.4) * mm});
            skLineSegment(sketch, "E858.MirrorCS", {"start": v(-36.69, 146.76) * mm, "end": v(-36.69, 152.4) * mm});
            skLineSegment(sketch, "E859.MirrorCS", {"start": v(-34.8, 146.76) * mm, "end": v(-34.8, 152.4) * mm});
            skLineSegment(sketch, "E860.MirrorCS", {"start": v(-32.92, 152.4) * mm, "end": v(-32.92, 146.76) * mm});
            skLineSegment(sketch, "E861.MirrorCS", {"start": v(-31.04, 150.52) * mm, "end": v(-36.69, 150.52) * mm});
            skLineSegment(sketch, "E862.MirrorCS", {"start": v(-36.69, 148.64) * mm, "end": v(-31.04, 148.64) * mm});
            skLineSegment(sketch, "E863.MirrorCS", {"start": v(-25.4, 150.52) * mm, "end": v(-31.04, 150.52) * mm});
            skLineSegment(sketch, "E864.MirrorCS", {"start": v(-31.04, 148.64) * mm, "end": v(-25.4, 148.64) * mm});
            skLineSegment(sketch, "E865.MirrorCS", {"start": v(-29.16, 141.11) * mm, "end": v(-29.16, 152.4) * mm});
            skLineSegment(sketch, "E866.MirrorCS", {"start": v(-27.28, 141.11) * mm, "end": v(-27.28, 152.4) * mm});
            skLineSegment(sketch, "E867.MirrorCS", {"start": v(-31.04, 146.76) * mm, "end": v(-31.04, 152.4) * mm});
            skLineSegment(sketch, "E868.MirrorCS", {"start": v(-31.04, 146.76) * mm, "end": v(-25.4, 146.76) * mm});
            skLineSegment(sketch, "E869.MirrorCS", {"start": v(-25.4, 144.87) * mm, "end": v(-31.04, 144.87) * mm});
            skLineSegment(sketch, "E870.MirrorCS", {"start": v(-25.4, 143) * mm, "end": v(-31.04, 143) * mm});
            skLineSegment(sketch, "E871.MirrorCS", {"start": v(-31.04, 141.11) * mm, "end": v(-25.4, 141.11) * mm});
            skLineSegment(sketch, "E872.MirrorCS", {"start": v(-25.4, 139.23) * mm, "end": v(-31.04, 139.23) * mm});
            skLineSegment(sketch, "E873.MirrorCS", {"start": v(-25.4, 137.35) * mm, "end": v(-31.04, 137.35) * mm});
            skLineSegment(sketch, "E874.MirrorCS", {"start": v(-36.69, 139.23) * mm, "end": v(-42.33, 139.23) * mm});
            skLineSegment(sketch, "E875.MirrorCS", {"start": v(-36.69, 141.11) * mm, "end": v(-42.33, 141.11) * mm});
            skLineSegment(sketch, "E876.MirrorCS", {"start": v(-31.04, 139.23) * mm, "end": v(-36.69, 139.23) * mm});
            skLineSegment(sketch, "E877.MirrorCS", {"start": v(-31.04, 137.35) * mm, "end": v(-42.33, 137.35) * mm});
            skLineSegment(sketch, "E878.MirrorCS", {"start": v(-40.45, 141.11) * mm, "end": v(-40.45, 135.47) * mm});
            skLineSegment(sketch, "E879.MirrorCS", {"start": v(-38.57, 141.11) * mm, "end": v(-38.57, 135.47) * mm});
            skLineSegment(sketch, "E880.MirrorCS", {"start": v(-36.69, 141.11) * mm, "end": v(-36.69, 135.47) * mm});
            skLineSegment(sketch, "E881.MirrorCS", {"start": v(-34.8, 141.11) * mm, "end": v(-34.8, 135.47) * mm});
            skLineSegment(sketch, "E882.MirrorCS", {"start": v(-32.93, 141.11) * mm, "end": v(-32.93, 135.47) * mm});
            skLineSegment(sketch, "E883.MirrorCS", {"start": v(-31.04, 141.11) * mm, "end": v(-31.04, 135.47) * mm});
            skLineSegment(sketch, "E884.MirrorCS", {"start": v(-29.16, 141.11) * mm, "end": v(-29.16, 135.47) * mm});
            skLineSegment(sketch, "E885.MirrorCS", {"start": v(-27.28, 141.11) * mm, "end": v(-27.28, 135.47) * mm});
            skLineSegment(sketch, "E886.MirrorCS", {"start": v(-42.33, 144.87) * mm, "end": v(-36.69, 144.87) * mm});
            skLineSegment(sketch, "E887.MirrorCS", {"start": v(-36.69, 143) * mm, "end": v(-42.33, 143) * mm});
            skLineSegment(sketch, "E888.MirrorCS", {"start": v(-36.69, 146.76) * mm, "end": v(-42.33, 146.76) * mm});
            skPoint(sketch, "E889.MirrorP", {"position": v(-42.33, 126.06) * mm});
            skPoint(sketch, "E890.MirrorP", {"position": v(-42.33, 131.7) * mm});
            skLineSegment(sketch, "E891.MirrorCS", {"start": v(-36.69, 124.18) * mm, "end": v(-36.69, 118.53) * mm});
            skLineSegment(sketch, "E892.MirrorCS", {"start": v(-31.04, 124.18) * mm, "end": v(-31.04, 118.53) * mm});
            skLineSegment(sketch, "E893.MirrorCS", {"start": v(-36.69, 129.82) * mm, "end": v(-42.33, 129.82) * mm});
            skLineSegment(sketch, "E894.MirrorCS", {"start": v(-31.04, 129.82) * mm, "end": v(-31.04, 135.47) * mm});
            skLineSegment(sketch, "E895.MirrorCS", {"start": v(-27.28, 129.82) * mm, "end": v(-27.28, 118.53) * mm});
            skLineSegment(sketch, "E896.MirrorCS", {"start": v(-38.57, 129.82) * mm, "end": v(-38.57, 135.47) * mm});
            skLineSegment(sketch, "E897.MirrorCS", {"start": v(-31.04, 129.82) * mm, "end": v(-25.4, 129.82) * mm});
            skLineSegment(sketch, "E898.MirrorCS", {"start": v(-31.04, 124.18) * mm, "end": v(-25.4, 124.18) * mm});
            skLineSegment(sketch, "E899.MirrorCS", {"start": v(-31.04, 133.58) * mm, "end": v(-42.33, 133.58) * mm});
            skLineSegment(sketch, "E900.MirrorCS", {"start": v(-31.04, 122.3) * mm, "end": v(-25.4, 122.3) * mm});
            skLineSegment(sketch, "E901.MirrorCS", {"start": v(-36.69, 127.94) * mm, "end": v(-42.33, 127.94) * mm});
            skLineSegment(sketch, "E902.MirrorCS", {"start": v(-40.45, 129.82) * mm, "end": v(-40.45, 135.47) * mm});
            skLineSegment(sketch, "E903.MirrorCS", {"start": v(-36.69, 131.7) * mm, "end": v(-42.33, 131.7) * mm});
            skLineSegment(sketch, "E904.MirrorCS", {"start": v(-34.8, 129.82) * mm, "end": v(-34.8, 135.47) * mm});
            skLineSegment(sketch, "E905.MirrorCS", {"start": v(-25.4, 126.06) * mm, "end": v(-31.04, 126.06) * mm});
            skLineSegment(sketch, "E906.MirrorCS", {"start": v(-36.69, 122.3) * mm, "end": v(-31.04, 122.3) * mm});
            skLineSegment(sketch, "E907.MirrorCS", {"start": v(-32.92, 118.53) * mm, "end": v(-32.92, 124.18) * mm});
            skLineSegment(sketch, "E908.MirrorCS", {"start": v(-25.4, 120.41) * mm, "end": v(-31.04, 120.41) * mm});
            skLineSegment(sketch, "E909.MirrorCS", {"start": v(-34.8, 124.18) * mm, "end": v(-34.8, 118.53) * mm});
            skLineSegment(sketch, "E910.MirrorCS", {"start": v(-25.4, 127.94) * mm, "end": v(-31.04, 127.94) * mm});
            skLineSegment(sketch, "E911.MirrorCS", {"start": v(-29.16, 129.82) * mm, "end": v(-29.16, 135.47) * mm});
            skLineSegment(sketch, "E912.MirrorCS", {"start": v(-27.28, 129.82) * mm, "end": v(-27.28, 135.47) * mm});
            skLineSegment(sketch, "E913.MirrorCS", {"start": v(-25.4, 131.7) * mm, "end": v(-31.04, 131.7) * mm});
            skLineSegment(sketch, "E914.MirrorCS", {"start": v(-40.45, 129.82) * mm, "end": v(-40.45, 118.53) * mm});
            skLineSegment(sketch, "E915.MirrorCS", {"start": v(-42.33, 126.06) * mm, "end": v(-36.69, 126.06) * mm});
            skLineSegment(sketch, "E916.MirrorCS", {"start": v(-31.04, 131.7) * mm, "end": v(-36.69, 131.7) * mm});
            skLineSegment(sketch, "E917.MirrorCS", {"start": v(-31.04, 120.41) * mm, "end": v(-36.69, 120.41) * mm});
            skLineSegment(sketch, "E918.MirrorCS", {"start": v(-36.69, 120.41) * mm, "end": v(-42.33, 120.41) * mm});
            skLineSegment(sketch, "E919.MirrorCS", {"start": v(-36.69, 129.82) * mm, "end": v(-36.69, 135.47) * mm});
            skLineSegment(sketch, "E920.MirrorCS", {"start": v(-32.93, 129.82) * mm, "end": v(-32.93, 135.47) * mm});
            skLineSegment(sketch, "E921.MirrorCS", {"start": v(-25.4, 133.58) * mm, "end": v(-31.04, 133.58) * mm});
            skLineSegment(sketch, "E922.MirrorCS", {"start": v(-42.33, 122.3) * mm, "end": v(-36.69, 122.3) * mm});
            skLineSegment(sketch, "E923.MirrorCS", {"start": v(-36.69, 124.18) * mm, "end": v(-42.33, 124.18) * mm});
            skLineSegment(sketch, "E924.MirrorCS", {"start": v(-38.57, 129.82) * mm, "end": v(-38.57, 118.53) * mm});
            skLineSegment(sketch, "E925.MirrorCS", {"start": v(-29.16, 129.82) * mm, "end": v(-29.16, 118.53) * mm});
            skPoint(sketch, "E926.MirrorP", {"position": v(-42.33, 105.36) * mm});
            skPoint(sketch, "E927.MirrorP", {"position": v(-42.33, 111) * mm});
            skLineSegment(sketch, "E928.MirrorCS", {"start": v(-31.04, 105.36) * mm, "end": v(-36.69, 105.36) * mm});
            skLineSegment(sketch, "E929.MirrorCS", {"start": v(-36.69, 114.77) * mm, "end": v(-31.04, 114.77) * mm});
            skLineSegment(sketch, "E930.MirrorCS", {"start": v(-31.04, 116.65) * mm, "end": v(-36.69, 116.65) * mm});
            skLineSegment(sketch, "E931.MirrorCS", {"start": v(-31.04, 112.89) * mm, "end": v(-31.04, 118.53) * mm});
            skLineSegment(sketch, "E932.MirrorCS", {"start": v(-31.04, 107.24) * mm, "end": v(-31.04, 101.6) * mm});
            skLineSegment(sketch, "E933.MirrorCS", {"start": v(-31.04, 107.24) * mm, "end": v(-25.4, 107.24) * mm});
            skLineSegment(sketch, "E934.MirrorCS", {"start": v(-36.69, 107.24) * mm, "end": v(-42.33, 107.24) * mm});
            skLineSegment(sketch, "E935.MirrorCS", {"start": v(-36.69, 112.89) * mm, "end": v(-36.69, 118.53) * mm});
            skLineSegment(sketch, "E936.MirrorCS", {"start": v(-27.28, 107.24) * mm, "end": v(-27.28, 118.53) * mm});
            skLineSegment(sketch, "E937.MirrorCS", {"start": v(-31.04, 103.49) * mm, "end": v(-42.33, 103.49) * mm});
            skLineSegment(sketch, "E938.MirrorCS", {"start": v(-29.16, 107.24) * mm, "end": v(-29.16, 118.53) * mm});
            skLineSegment(sketch, "E939.MirrorCS", {"start": v(-25.4, 109.12) * mm, "end": v(-31.04, 109.12) * mm});
            skLineSegment(sketch, "E940.MirrorCS", {"start": v(-36.69, 112.89) * mm, "end": v(-42.33, 112.89) * mm});
            skLineSegment(sketch, "E941.MirrorCS", {"start": v(-25.4, 103.49) * mm, "end": v(-31.04, 103.49) * mm});
            skLineSegment(sketch, "E942.MirrorCS", {"start": v(-25.4, 111) * mm, "end": v(-31.04, 111) * mm});
            skLineSegment(sketch, "E943.MirrorCS", {"start": v(-32.92, 118.53) * mm, "end": v(-32.92, 112.89) * mm});
            skLineSegment(sketch, "E944.MirrorCS", {"start": v(-36.69, 109.12) * mm, "end": v(-42.33, 109.12) * mm});
            skLineSegment(sketch, "E945.MirrorCS", {"start": v(-31.04, 114.77) * mm, "end": v(-25.4, 114.77) * mm});
            skLineSegment(sketch, "E946.MirrorCS", {"start": v(-38.57, 107.24) * mm, "end": v(-38.57, 118.53) * mm});
            skLineSegment(sketch, "E947.MirrorCS", {"start": v(-38.57, 107.24) * mm, "end": v(-38.57, 101.6) * mm});
            skLineSegment(sketch, "E948.MirrorCS", {"start": v(-36.69, 116.65) * mm, "end": v(-42.33, 116.65) * mm});
            skLineSegment(sketch, "E949.MirrorCS", {"start": v(-34.8, 112.89) * mm, "end": v(-34.8, 118.53) * mm});
            skLineSegment(sketch, "E950.MirrorCS", {"start": v(-29.16, 107.24) * mm, "end": v(-29.16, 101.6) * mm});
            skLineSegment(sketch, "E951.MirrorCS", {"start": v(-34.8, 107.24) * mm, "end": v(-34.8, 101.6) * mm});
            skLineSegment(sketch, "E952.MirrorCS", {"start": v(-31.04, 112.89) * mm, "end": v(-25.4, 112.89) * mm});
            skLineSegment(sketch, "E953.MirrorCS", {"start": v(-32.93, 107.24) * mm, "end": v(-32.93, 101.6) * mm});
            skLineSegment(sketch, "E954.MirrorCS", {"start": v(-42.33, 111) * mm, "end": v(-36.69, 111) * mm});
            skLineSegment(sketch, "E955.MirrorCS", {"start": v(-40.45, 107.24) * mm, "end": v(-40.45, 101.6) * mm});
            skLineSegment(sketch, "E956.MirrorCS", {"start": v(-25.4, 116.65) * mm, "end": v(-31.04, 116.65) * mm});
            skLineSegment(sketch, "E957.MirrorCS", {"start": v(-40.45, 107.24) * mm, "end": v(-40.45, 118.53) * mm});
            skLineSegment(sketch, "E958.MirrorCS", {"start": v(-36.69, 107.24) * mm, "end": v(-36.69, 101.6) * mm});
            skLineSegment(sketch, "E959.MirrorCS", {"start": v(-25.4, 105.36) * mm, "end": v(-31.04, 105.36) * mm});
            skLineSegment(sketch, "E960.MirrorCS", {"start": v(-42.33, 114.77) * mm, "end": v(-36.69, 114.77) * mm});
            skLineSegment(sketch, "E961.MirrorCS", {"start": v(-36.69, 105.36) * mm, "end": v(-42.33, 105.36) * mm});
            skLineSegment(sketch, "E962.MirrorCS", {"start": v(-27.28, 107.24) * mm, "end": v(-27.28, 101.6) * mm});
            skLineSegment(sketch, "E963.MirrorCS", {"start": v(-53.62, 116.65) * mm, "end": v(-47.98, 116.65) * mm});
            skLineSegment(sketch, "E964.MirrorCS", {"start": v(-47.98, 114.77) * mm, "end": v(-53.62, 114.77) * mm});
            skLineSegment(sketch, "E965.MirrorCS", {"start": v(-53.62, 105.36) * mm, "end": v(-47.98, 105.36) * mm});
            skLineSegment(sketch, "E966.MirrorCS", {"start": v(-53.62, 112.89) * mm, "end": v(-53.62, 118.53) * mm});
            skLineSegment(sketch, "E967.MirrorCS", {"start": v(-53.62, 107.24) * mm, "end": v(-53.62, 101.6) * mm});
            skLineSegment(sketch, "E968.MirrorCS", {"start": v(-47.98, 107.24) * mm, "end": v(-42.33, 107.24) * mm});
            skLineSegment(sketch, "E969.MirrorCS", {"start": v(-53.62, 107.24) * mm, "end": v(-59.27, 107.24) * mm});
            skLineSegment(sketch, "E970.MirrorCS", {"start": v(-47.98, 112.89) * mm, "end": v(-47.98, 118.53) * mm});
            skLineSegment(sketch, "E971.MirrorCS", {"start": v(-57.39, 107.24) * mm, "end": v(-57.39, 118.53) * mm});
            skLineSegment(sketch, "E972.MirrorCS", {"start": v(-51.74, 118.53) * mm, "end": v(-51.74, 112.89) * mm});
            skLineSegment(sketch, "E973.MirrorCS", {"start": v(-53.62, 114.77) * mm, "end": v(-59.27, 114.77) * mm});
            skLineSegment(sketch, "E974.MirrorCS", {"start": v(-47.98, 112.89) * mm, "end": v(-42.33, 112.89) * mm});
            skLineSegment(sketch, "E975.MirrorCS", {"start": v(-59.27, 116.65) * mm, "end": v(-53.62, 116.65) * mm});
            skLineSegment(sketch, "E976.MirrorCS", {"start": v(-49.86, 112.89) * mm, "end": v(-49.86, 118.53) * mm});
            skLineSegment(sketch, "E977.MirrorCS", {"start": v(-59.27, 111) * mm, "end": v(-53.62, 111) * mm});
            skLineSegment(sketch, "E978.MirrorCS", {"start": v(-44.22, 107.24) * mm, "end": v(-44.22, 101.6) * mm});
            skLineSegment(sketch, "E979.MirrorCS", {"start": v(-53.62, 112.89) * mm, "end": v(-59.27, 112.89) * mm});
            skLineSegment(sketch, "E980.MirrorCS", {"start": v(-57.39, 107.24) * mm, "end": v(-57.39, 101.6) * mm});
            skLineSegment(sketch, "E981.MirrorCS", {"start": v(-47.98, 107.24) * mm, "end": v(-47.98, 101.6) * mm});
            skLineSegment(sketch, "E982.MirrorCS", {"start": v(-42.33, 114.77) * mm, "end": v(-47.98, 114.77) * mm});
            skLineSegment(sketch, "E983.MirrorCS", {"start": v(-44.22, 107.24) * mm, "end": v(-44.22, 118.53) * mm});
            skLineSegment(sketch, "E984.MirrorCS", {"start": v(-59.27, 105.36) * mm, "end": v(-53.62, 105.36) * mm});
            skLineSegment(sketch, "E985.MirrorCS", {"start": v(-42.33, 111) * mm, "end": v(-47.98, 111) * mm});
            skLineSegment(sketch, "E986.MirrorCS", {"start": v(-47.98, 105.36) * mm, "end": v(-42.33, 105.36) * mm});
            skLineSegment(sketch, "E987.MirrorCS", {"start": v(-55.5, 107.24) * mm, "end": v(-55.5, 101.6) * mm});
            skLineSegment(sketch, "E988.MirrorCS", {"start": v(-47.98, 109.12) * mm, "end": v(-42.33, 109.12) * mm});
            skLineSegment(sketch, "E989.MirrorCS", {"start": v(-46.1, 107.24) * mm, "end": v(-46.1, 118.53) * mm});
            skLineSegment(sketch, "E990.MirrorCS", {"start": v(-46.1, 107.24) * mm, "end": v(-46.1, 101.6) * mm});
            skLineSegment(sketch, "E991.MirrorCS", {"start": v(-53.62, 103.49) * mm, "end": v(-42.33, 103.49) * mm});
            skLineSegment(sketch, "E992.MirrorCS", {"start": v(-47.98, 116.65) * mm, "end": v(-42.33, 116.65) * mm});
            skLineSegment(sketch, "E993.MirrorCS", {"start": v(-49.86, 107.24) * mm, "end": v(-49.86, 101.6) * mm});
            skLineSegment(sketch, "E994.MirrorCS", {"start": v(-51.74, 107.24) * mm, "end": v(-51.74, 101.6) * mm});
            skLineSegment(sketch, "E995.MirrorCS", {"start": v(-55.5, 107.24) * mm, "end": v(-55.5, 118.53) * mm});
            skLineSegment(sketch, "E996.MirrorCS", {"start": v(-59.27, 109.12) * mm, "end": v(-53.62, 109.12) * mm});
            skLineSegment(sketch, "E997.MirrorCS", {"start": v(-59.27, 103.49) * mm, "end": v(-53.62, 103.49) * mm});
            skLineSegment(sketch, "E998.MirrorCS", {"start": v(-64.91, 116.65) * mm, "end": v(-70.56, 116.65) * mm});
            skLineSegment(sketch, "E999.MirrorCS", {"start": v(-70.56, 114.77) * mm, "end": v(-64.91, 114.77) * mm});
            skLineSegment(sketch, "E1000.MirrorCS", {"start": v(-64.91, 105.36) * mm, "end": v(-70.56, 105.36) * mm});
            skLineSegment(sketch, "E1001.MirrorCS", {"start": v(-61.15, 107.24) * mm, "end": v(-61.15, 118.53) * mm});
            skLineSegment(sketch, "E1002.MirrorCS", {"start": v(-76.2, 114.77) * mm, "end": v(-70.56, 114.77) * mm});
            skLineSegment(sketch, "E1003.MirrorCS", {"start": v(-59.27, 109.12) * mm, "end": v(-64.91, 109.12) * mm});
            skLineSegment(sketch, "E1004.MirrorCS", {"start": v(-64.91, 107.24) * mm, "end": v(-64.91, 101.6) * mm});
            skLineSegment(sketch, "E1005.MirrorCS", {"start": v(-66.8, 118.53) * mm, "end": v(-66.8, 112.89) * mm});
            skLineSegment(sketch, "E1006.MirrorCS", {"start": v(-59.27, 103.49) * mm, "end": v(-64.91, 103.49) * mm});
            skLineSegment(sketch, "E1007.MirrorCS", {"start": v(-59.27, 116.65) * mm, "end": v(-64.91, 116.65) * mm});
            skLineSegment(sketch, "E1008.MirrorCS", {"start": v(-63.03, 107.24) * mm, "end": v(-63.03, 101.6) * mm});
            skLineSegment(sketch, "E1009.MirrorCS", {"start": v(-72.44, 107.24) * mm, "end": v(-72.44, 101.6) * mm});
            skLineSegment(sketch, "E1010.MirrorCS", {"start": v(-70.56, 105.36) * mm, "end": v(-76.2, 105.36) * mm});
            skLineSegment(sketch, "E1011.MirrorCS", {"start": v(-64.91, 114.77) * mm, "end": v(-59.27, 114.77) * mm});
            skLineSegment(sketch, "E1012.MirrorCS", {"start": v(-68.68, 107.24) * mm, "end": v(-68.68, 101.6) * mm});
            skLineSegment(sketch, "E1013.MirrorCS", {"start": v(-70.56, 112.89) * mm, "end": v(-76.2, 112.89) * mm});
            skLineSegment(sketch, "E1014.MirrorCS", {"start": v(-66.8, 107.24) * mm, "end": v(-66.8, 101.6) * mm});
            skLineSegment(sketch, "E1015.MirrorCS", {"start": v(-64.91, 112.89) * mm, "end": v(-64.91, 118.53) * mm});
            skLineSegment(sketch, "E1016.MirrorCS", {"start": v(-59.27, 111) * mm, "end": v(-64.91, 111) * mm});
            skLineSegment(sketch, "E1017.MirrorCS", {"start": v(-70.56, 116.65) * mm, "end": v(-76.2, 116.65) * mm});
            skLineSegment(sketch, "E1018.MirrorCS", {"start": v(-64.91, 103.49) * mm, "end": v(-76.2, 103.49) * mm});
            skLineSegment(sketch, "E1019.MirrorCS", {"start": v(-64.91, 112.89) * mm, "end": v(-59.27, 112.89) * mm});
            skLineSegment(sketch, "E1020.MirrorCS", {"start": v(-74.31, 107.24) * mm, "end": v(-74.31, 118.53) * mm});
            skLineSegment(sketch, "E1021.MirrorCS", {"start": v(-61.15, 107.24) * mm, "end": v(-61.15, 101.6) * mm});
            skLineSegment(sketch, "E1022.MirrorCS", {"start": v(-70.56, 109.12) * mm, "end": v(-76.2, 109.12) * mm});
            skLineSegment(sketch, "E1023.MirrorCS", {"start": v(-68.67, 112.89) * mm, "end": v(-68.67, 118.53) * mm});
            skLineSegment(sketch, "E1024.MirrorCS", {"start": v(-70.56, 107.24) * mm, "end": v(-70.56, 101.6) * mm});
            skLineSegment(sketch, "E1025.MirrorCS", {"start": v(-74.31, 107.24) * mm, "end": v(-74.31, 101.6) * mm});
            skLineSegment(sketch, "E1026.MirrorCS", {"start": v(-70.56, 107.24) * mm, "end": v(-76.2, 107.24) * mm});
            skLineSegment(sketch, "E1027.MirrorCS", {"start": v(-63.03, 107.24) * mm, "end": v(-63.03, 118.53) * mm});
            skLineSegment(sketch, "E1028.MirrorCS", {"start": v(-76.2, 111) * mm, "end": v(-70.56, 111) * mm});
            skLineSegment(sketch, "E1029.MirrorCS", {"start": v(-72.44, 107.24) * mm, "end": v(-72.44, 118.53) * mm});
            skLineSegment(sketch, "E1030.MirrorCS", {"start": v(-59.27, 105.36) * mm, "end": v(-64.91, 105.36) * mm});
            skLineSegment(sketch, "E1031.MirrorCS", {"start": v(-64.91, 107.24) * mm, "end": v(-59.27, 107.24) * mm});
            skLineSegment(sketch, "E1032.MirrorCS", {"start": v(-70.56, 112.89) * mm, "end": v(-70.56, 118.53) * mm});
            skLineSegment(sketch, "E1033.MirrorCS", {"start": v(-64.91, 131.7) * mm, "end": v(-70.56, 131.7) * mm});
            skLineSegment(sketch, "E1034.MirrorCS", {"start": v(-70.56, 122.3) * mm, "end": v(-64.91, 122.3) * mm});
            skLineSegment(sketch, "E1035.MirrorCS", {"start": v(-64.91, 120.41) * mm, "end": v(-70.56, 120.41) * mm});
            skLineSegment(sketch, "E1036.MirrorCS", {"start": v(-70.56, 124.18) * mm, "end": v(-70.56, 118.53) * mm});
            skLineSegment(sketch, "E1037.MirrorCS", {"start": v(-64.91, 129.82) * mm, "end": v(-59.27, 129.82) * mm});
            skLineSegment(sketch, "E1038.MirrorCS", {"start": v(-64.91, 124.18) * mm, "end": v(-64.91, 118.53) * mm});
            skLineSegment(sketch, "E1039.MirrorCS", {"start": v(-70.56, 129.82) * mm, "end": v(-76.2, 129.82) * mm});
            skLineSegment(sketch, "E1040.MirrorCS", {"start": v(-64.91, 129.82) * mm, "end": v(-64.91, 135.47) * mm});
            skLineSegment(sketch, "E1041.MirrorCS", {"start": v(-61.15, 129.82) * mm, "end": v(-61.15, 118.53) * mm});
            skLineSegment(sketch, "E1042.MirrorCS", {"start": v(-76.2, 122.3) * mm, "end": v(-70.56, 122.3) * mm});
            skLineSegment(sketch, "E1043.MirrorCS", {"start": v(-59.27, 131.7) * mm, "end": v(-64.91, 131.7) * mm});
            skLineSegment(sketch, "E1044.MirrorCS", {"start": v(-74.31, 129.82) * mm, "end": v(-74.31, 118.53) * mm});
            skLineSegment(sketch, "E1045.MirrorCS", {"start": v(-59.27, 126.06) * mm, "end": v(-64.91, 126.06) * mm});
            skLineSegment(sketch, "E1046.MirrorCS", {"start": v(-70.56, 127.94) * mm, "end": v(-76.2, 127.94) * mm});
            skLineSegment(sketch, "E1047.MirrorCS", {"start": v(-59.27, 120.41) * mm, "end": v(-64.91, 120.41) * mm});
            skLineSegment(sketch, "E1048.MirrorCS", {"start": v(-63.03, 129.82) * mm, "end": v(-63.03, 118.53) * mm});
            skLineSegment(sketch, "E1049.MirrorCS", {"start": v(-70.56, 129.82) * mm, "end": v(-70.56, 135.47) * mm});
            skLineSegment(sketch, "E1050.MirrorCS", {"start": v(-64.91, 122.3) * mm, "end": v(-59.27, 122.3) * mm});
            skLineSegment(sketch, "E1051.MirrorCS", {"start": v(-72.44, 129.82) * mm, "end": v(-72.44, 118.53) * mm});
            skLineSegment(sketch, "E1052.MirrorCS", {"start": v(-66.8, 118.53) * mm, "end": v(-66.8, 124.18) * mm});
            skLineSegment(sketch, "E1053.MirrorCS", {"start": v(-74.31, 129.82) * mm, "end": v(-74.31, 135.47) * mm});
            skLineSegment(sketch, "E1054.MirrorCS", {"start": v(-59.27, 133.58) * mm, "end": v(-64.91, 133.58) * mm});
            skLineSegment(sketch, "E1055.MirrorCS", {"start": v(-64.91, 124.18) * mm, "end": v(-59.27, 124.18) * mm});
            skLineSegment(sketch, "E1056.MirrorCS", {"start": v(-70.56, 120.41) * mm, "end": v(-76.2, 120.41) * mm});
            skLineSegment(sketch, "E1057.MirrorCS", {"start": v(-64.91, 133.58) * mm, "end": v(-76.2, 133.58) * mm});
            skLineSegment(sketch, "E1058.MirrorCS", {"start": v(-70.56, 124.18) * mm, "end": v(-76.2, 124.18) * mm});
            skLineSegment(sketch, "E1059.MirrorCS", {"start": v(-70.56, 131.7) * mm, "end": v(-76.2, 131.7) * mm});
            skLineSegment(sketch, "E1060.MirrorCS", {"start": v(-61.15, 129.82) * mm, "end": v(-61.15, 135.47) * mm});
            skLineSegment(sketch, "E1061.MirrorCS", {"start": v(-72.44, 129.82) * mm, "end": v(-72.44, 135.47) * mm});
            skLineSegment(sketch, "E1062.MirrorCS", {"start": v(-68.67, 124.18) * mm, "end": v(-68.67, 118.53) * mm});
            skLineSegment(sketch, "E1063.MirrorCS", {"start": v(-59.27, 127.94) * mm, "end": v(-64.91, 127.94) * mm});
            skLineSegment(sketch, "E1064.MirrorCS", {"start": v(-76.2, 126.06) * mm, "end": v(-70.56, 126.06) * mm});
            skLineSegment(sketch, "E1065.MirrorCS", {"start": v(-68.68, 129.82) * mm, "end": v(-68.68, 135.47) * mm});
            skLineSegment(sketch, "E1066.MirrorCS", {"start": v(-63.03, 129.82) * mm, "end": v(-63.03, 135.47) * mm});
            skLineSegment(sketch, "E1067.MirrorCS", {"start": v(-66.8, 129.82) * mm, "end": v(-66.8, 135.47) * mm});
            skPoint(sketch, "E1068.MirrorP", {"position": v(-70.56, 139.23) * mm});
            skPoint(sketch, "E1069.MirrorP", {"position": v(-64.91, 148.64) * mm});
            skPoint(sketch, "E1070.MirrorP", {"position": v(-64.91, 139.23) * mm});
            skPoint(sketch, "E1071.MirrorP", {"position": v(-76.2, 139.23) * mm});
            skLineSegment(sketch, "E1072.MirrorCS", {"start": v(-64.91, 139.23) * mm, "end": v(-70.56, 139.23) * mm});
            skLineSegment(sketch, "E1073.MirrorCS", {"start": v(-70.56, 148.64) * mm, "end": v(-64.91, 148.64) * mm});
            skPoint(sketch, "E1074.MirrorP", {"position": v(-76.2, 144.87) * mm});
            skPoint(sketch, "E1075.MirrorP", {"position": v(-64.91, 144.87) * mm});
            skLineSegment(sketch, "E1076.MirrorCS", {"start": v(-64.91, 150.52) * mm, "end": v(-70.56, 150.52) * mm});
            skLineSegment(sketch, "E1077.MirrorCS", {"start": v(-64.91, 146.76) * mm, "end": v(-64.91, 152.4) * mm});
            skLineSegment(sketch, "E1078.MirrorCS", {"start": v(-63.03, 141.11) * mm, "end": v(-63.03, 152.4) * mm});
            skLineSegment(sketch, "E1079.MirrorCS", {"start": v(-66.8, 141.11) * mm, "end": v(-66.8, 135.47) * mm});
            skLineSegment(sketch, "E1080.MirrorCS", {"start": v(-64.91, 146.76) * mm, "end": v(-59.27, 146.76) * mm});
            skLineSegment(sketch, "E1081.MirrorCS", {"start": v(-70.56, 146.76) * mm, "end": v(-70.56, 152.4) * mm});
            skLineSegment(sketch, "E1082.MirrorCS", {"start": v(-74.31, 141.11) * mm, "end": v(-74.31, 152.4) * mm});
            skLineSegment(sketch, "E1083.MirrorCS", {"start": v(-61.15, 141.11) * mm, "end": v(-61.15, 135.47) * mm});
            skLineSegment(sketch, "E1084.MirrorCS", {"start": v(-59.27, 139.23) * mm, "end": v(-64.91, 139.23) * mm});
            skLineSegment(sketch, "E1085.MirrorCS", {"start": v(-76.2, 144.87) * mm, "end": v(-70.56, 144.87) * mm});
            skLineSegment(sketch, "E1086.MirrorCS", {"start": v(-59.27, 143) * mm, "end": v(-64.91, 143) * mm});
            skLineSegment(sketch, "E1087.MirrorCS", {"start": v(-70.56, 141.11) * mm, "end": v(-76.2, 141.11) * mm});
            skLineSegment(sketch, "E1088.MirrorCS", {"start": v(-70.56, 141.11) * mm, "end": v(-70.56, 135.47) * mm});
            skLineSegment(sketch, "E1089.MirrorCS", {"start": v(-63.03, 141.11) * mm, "end": v(-63.03, 135.47) * mm});
            skLineSegment(sketch, "E1090.MirrorCS", {"start": v(-70.56, 146.76) * mm, "end": v(-76.2, 146.76) * mm});
            skLineSegment(sketch, "E1091.MirrorCS", {"start": v(-70.56, 139.23) * mm, "end": v(-76.2, 139.23) * mm});
            skLineSegment(sketch, "E1092.MirrorCS", {"start": v(-64.91, 137.35) * mm, "end": v(-76.2, 137.35) * mm});
            skLineSegment(sketch, "E1093.MirrorCS", {"start": v(-68.68, 141.11) * mm, "end": v(-68.68, 135.47) * mm});
            skLineSegment(sketch, "E1094.MirrorCS", {"start": v(-66.8, 152.4) * mm, "end": v(-66.8, 146.76) * mm});
            skLineSegment(sketch, "E1095.MirrorCS", {"start": v(-72.44, 141.11) * mm, "end": v(-72.44, 135.47) * mm});
            skLineSegment(sketch, "E1096.MirrorCS", {"start": v(-59.27, 137.35) * mm, "end": v(-64.91, 137.35) * mm});
            skLineSegment(sketch, "E1097.MirrorCS", {"start": v(-59.27, 150.52) * mm, "end": v(-64.91, 150.52) * mm});
            skLineSegment(sketch, "E1098.MirrorCS", {"start": v(-68.67, 146.76) * mm, "end": v(-68.67, 152.4) * mm});
            skLineSegment(sketch, "E1099.MirrorCS", {"start": v(-72.44, 141.11) * mm, "end": v(-72.44, 152.4) * mm});
            skLineSegment(sketch, "E1100.MirrorCS", {"start": v(-64.91, 141.11) * mm, "end": v(-64.91, 135.47) * mm});
            skLineSegment(sketch, "E1101.MirrorCS", {"start": v(-61.15, 141.11) * mm, "end": v(-61.15, 152.4) * mm});
            skLineSegment(sketch, "E1102.MirrorCS", {"start": v(-64.91, 141.11) * mm, "end": v(-59.27, 141.11) * mm});
            skLineSegment(sketch, "E1103.MirrorCS", {"start": v(-70.56, 150.52) * mm, "end": v(-76.2, 150.52) * mm});
            skLineSegment(sketch, "E1104.MirrorCS", {"start": v(-74.31, 141.11) * mm, "end": v(-74.31, 135.47) * mm});
            skLineSegment(sketch, "E1105.MirrorCS", {"start": v(-59.27, 144.87) * mm, "end": v(-64.91, 144.87) * mm});
            skLineSegment(sketch, "E1106.MirrorCS", {"start": v(-76.2, 148.64) * mm, "end": v(-70.56, 148.64) * mm});
            skLineSegment(sketch, "E1107.MirrorCS", {"start": v(-64.91, 148.64) * mm, "end": v(-59.27, 148.64) * mm});
            skLineSegment(sketch, "E1108.MirrorCS", {"start": v(-70.56, 143) * mm, "end": v(-76.2, 143) * mm});
            skLineSegment(sketch, "E1109.MirrorCS", {"start": v(-8.47, 111) * mm, "end": v(-14.11, 111) * mm});
            skPoint(sketch, "E1110.MirrorP", {"position": v(-8.47, 111) * mm});
            skPoint(sketch, "E1111.MirrorCS.end.orphan", {"position": v(-8.47, 112.89) * mm});
            skPoint(sketch, "E1111.MirrorCS.start.orphan", {"position": v(-14.11, 112.89) * mm});
            skPoint(sketch, "E1112.MirrorCS.end.orphan", {"position": v(-14.11, 111) * mm});
            skPoint(sketch, "E1113.MirrorCS.end.orphan", {"position": v(-59.27, 84.67) * mm});
            skPoint(sketch, "E1113.MirrorCS.start.orphan", {"position": v(-59.27, 101.6) * mm});
            skLineSegment(sketch, "E1114.MirrorCS", {"start": v(19.76, 114.77) * mm, "end": v(14.11, 114.77) * mm});
            skLineSegment(sketch, "E1115.MirrorCS", {"start": v(14.11, 116.65) * mm, "end": v(19.76, 116.65) * mm});
            skLineSegment(sketch, "E1116.MirrorCS", {"start": v(14.11, 120.41) * mm, "end": v(19.76, 120.41) * mm});
            skLineSegment(sketch, "E1117.MirrorCS", {"start": v(19.76, 122.3) * mm, "end": v(14.11, 122.3) * mm});
            skPoint(sketch, "E1118.MirrorP", {"position": v(-8.47, 105.36) * mm});
            skLineSegment(sketch, "E1119.MirrorCS", {"start": v(14.11, 105.36) * mm, "end": v(19.76, 105.36) * mm});
            skLineSegment(sketch, "E1120.MirrorCS", {"start": v(14.11, 131.7) * mm, "end": v(19.76, 131.7) * mm});
            skLineSegment(sketch, "E1121.MirrorCS", {"start": v(14.11, 124.18) * mm, "end": v(14.11, 118.53) * mm});
            skLineSegment(sketch, "E1122.MirrorCS", {"start": v(16, 118.53) * mm, "end": v(16, 124.18) * mm});
            skLineSegment(sketch, "E1123.MirrorCS", {"start": v(16, 118.53) * mm, "end": v(16, 112.89) * mm});
            skLineSegment(sketch, "E1124.MirrorCS", {"start": v(17.87, 112.89) * mm, "end": v(17.87, 118.53) * mm});
            skLineSegment(sketch, "E1125.MirrorCS", {"start": v(14.11, 139.23) * mm, "end": v(19.76, 139.23) * mm});
            skLineSegment(sketch, "E1126.MirrorCS", {"start": v(14.11, 112.89) * mm, "end": v(14.11, 118.53) * mm});
            skLineSegment(sketch, "E1127.MirrorCS", {"start": v(19.76, 112.89) * mm, "end": v(19.76, 118.53) * mm});
            skLineSegment(sketch, "E1128.MirrorCS", {"start": v(8.47, 150.52) * mm, "end": v(14.11, 150.52) * mm});
            skLineSegment(sketch, "E1129.MirrorCS", {"start": v(14.11, 148.64) * mm, "end": v(8.47, 148.64) * mm});
            skLineSegment(sketch, "E1130.MirrorCS", {"start": v(14.11, 146.76) * mm, "end": v(8.47, 146.76) * mm});
            skPoint(sketch, "E1131.MirrorP", {"position": v(14.11, 148.64) * mm});
            skPoint(sketch, "E1132.MirrorP", {"position": v(14.11, 139.23) * mm});
            skLineSegment(sketch, "E1133.MirrorCS", {"start": v(2.82, 105.36) * mm, "end": v(-2.82, 105.36) * mm});
            skPoint(sketch, "E1134.MirrorP", {"position": v(8.47, 148.64) * mm});
            skLineSegment(sketch, "E1135.MirrorCS", {"start": v(19.76, 124.18) * mm, "end": v(19.76, 118.53) * mm});
            skLineSegment(sketch, "E1136.MirrorCS", {"start": v(17.87, 124.18) * mm, "end": v(17.87, 118.53) * mm});
            skLineSegment(sketch, "E1137.MirrorCS", {"start": v(-2.82, 114.77) * mm, "end": v(2.82, 114.77) * mm});
            skLineSegment(sketch, "E1138.MirrorCS", {"start": v(2.82, 116.65) * mm, "end": v(-2.82, 116.65) * mm});
            skLineSegment(sketch, "E1139.MirrorCS", {"start": v(19.76, 148.64) * mm, "end": v(14.11, 148.64) * mm});
            skLineSegment(sketch, "E1140.MirrorCS", {"start": v(14.11, 150.52) * mm, "end": v(19.76, 150.52) * mm});
            skPoint(sketch, "E1141.MirrorP", {"position": v(19.76, 139.23) * mm});
            skLineSegment(sketch, "E1142.MirrorCS", {"start": v(16, 141.11) * mm, "end": v(16, 135.47) * mm});
            skLineSegment(sketch, "E1143.MirrorCS", {"start": v(-14.11, 114.77) * mm, "end": v(-19.76, 114.77) * mm});
            skLineSegment(sketch, "E1144.MirrorCS", {"start": v(12.23, 141.11) * mm, "end": v(12.23, 135.47) * mm});
            skLineSegment(sketch, "E1145.MirrorCS", {"start": v(16, 129.82) * mm, "end": v(16, 135.47) * mm});
            skLineSegment(sketch, "E1146.MirrorCS", {"start": v(-2.82, 112.89) * mm, "end": v(-8.47, 112.89) * mm});
            skLineSegment(sketch, "E1147.MirrorCS", {"start": v(-2.82, 105.36) * mm, "end": v(-8.47, 105.36) * mm});
            skLineSegment(sketch, "E1148.MirrorCS", {"start": v(14.11, 129.82) * mm, "end": v(14.11, 135.47) * mm});
            skPoint(sketch, "E1149.MirrorP", {"position": v(14.11, 144.87) * mm});
            skLineSegment(sketch, "E1150.MirrorCS", {"start": v(2.82, 103.49) * mm, "end": v(-8.47, 103.49) * mm});
            skLineSegment(sketch, "E1151.MirrorCS", {"start": v(-19.76, 116.65) * mm, "end": v(-14.11, 116.65) * mm});
            skLineSegment(sketch, "E1152.MirrorCS", {"start": v(-2.82, 107.24) * mm, "end": v(-8.47, 107.24) * mm});
            skLineSegment(sketch, "E1153.MirrorCS", {"start": v(-0.94, 112.89) * mm, "end": v(-0.94, 118.53) * mm});
            skLineSegment(sketch, "E1154.MirrorCS", {"start": v(-2.82, 112.89) * mm, "end": v(-2.82, 118.53) * mm});
            skLineSegment(sketch, "E1155.MirrorCS", {"start": v(12.23, 129.82) * mm, "end": v(12.23, 135.47) * mm});
            skLineSegment(sketch, "E1156.MirrorCS", {"start": v(14.11, 141.11) * mm, "end": v(14.11, 135.47) * mm});
            skLineSegment(sketch, "E1157.MirrorCS", {"start": v(2.82, 148.64) * mm, "end": v(8.47, 148.64) * mm});
            skLineSegment(sketch, "E1158.MirrorCS", {"start": v(8.47, 144.87) * mm, "end": v(14.11, 144.87) * mm});
            skLineSegment(sketch, "E1159.MirrorCS", {"start": v(19.76, 146.76) * mm, "end": v(19.76, 152.4) * mm});
            skLineSegment(sketch, "E1160.MirrorCS", {"start": v(-16, 112.89) * mm, "end": v(-16, 118.53) * mm});
            skLineSegment(sketch, "E1161.MirrorCS", {"start": v(2.82, 112.89) * mm, "end": v(2.82, 118.53) * mm});
            skLineSegment(sketch, "E1162.MirrorCS", {"start": v(14.11, 146.76) * mm, "end": v(14.11, 152.4) * mm});
            skLineSegment(sketch, "E1163.MirrorCS", {"start": v(19.76, 141.11) * mm, "end": v(19.76, 135.47) * mm});
            skLineSegment(sketch, "E1164.MirrorCS", {"start": v(8.47, 131.7) * mm, "end": v(14.11, 131.7) * mm});
            skLineSegment(sketch, "E1165.MirrorCS", {"start": v(14.11, 107.24) * mm, "end": v(8.47, 107.24) * mm});
            skLineSegment(sketch, "E1166.MirrorCS", {"start": v(10.35, 107.24) * mm, "end": v(10.35, 118.53) * mm});
            skLineSegment(sketch, "E1167.MirrorCS", {"start": v(8.47, 127.94) * mm, "end": v(14.11, 127.94) * mm});
            skLineSegment(sketch, "E1168.MirrorCS", {"start": v(14.11, 141.11) * mm, "end": v(8.47, 141.11) * mm});
            skLineSegment(sketch, "E1169.MirrorCS", {"start": v(2.82, 146.76) * mm, "end": v(8.47, 146.76) * mm});
            skLineSegment(sketch, "E1170.MirrorCS", {"start": v(12.23, 141.11) * mm, "end": v(12.23, 152.4) * mm});
            skLineSegment(sketch, "E1171.MirrorCS", {"start": v(6.59, 107.24) * mm, "end": v(6.59, 118.53) * mm});
            skLineSegment(sketch, "E1172.MirrorCS", {"start": v(-19.76, 112.89) * mm, "end": v(-19.76, 118.53) * mm});
            skLineSegment(sketch, "E1173.MirrorCS", {"start": v(14.11, 129.82) * mm, "end": v(8.47, 129.82) * mm});
            skLineSegment(sketch, "E1174.MirrorCS", {"start": v(-17.88, 118.53) * mm, "end": v(-17.88, 112.89) * mm});
            skLineSegment(sketch, "E1175.MirrorCS", {"start": v(8.47, 143) * mm, "end": v(2.82, 143) * mm});
            skLineSegment(sketch, "E1176.MirrorCS", {"start": v(17.87, 146.76) * mm, "end": v(17.87, 152.4) * mm});
            skLineSegment(sketch, "E1177.MirrorCS", {"start": v(2.82, 141.11) * mm, "end": v(8.47, 141.11) * mm});
            skLineSegment(sketch, "E1178.MirrorCS", {"start": v(8.47, 105.36) * mm, "end": v(2.82, 105.36) * mm});
            skLineSegment(sketch, "E1179.MirrorCS", {"start": v(16, 152.4) * mm, "end": v(16, 146.76) * mm});
            skLineSegment(sketch, "E1180.MirrorCS", {"start": v(2.82, 107.24) * mm, "end": v(8.47, 107.24) * mm});
            skLineSegment(sketch, "E1181.MirrorCS", {"start": v(-19.76, 105.36) * mm, "end": v(-14.11, 105.36) * mm});
            skLineSegment(sketch, "E1182.MirrorCS", {"start": v(0.94, 118.53) * mm, "end": v(0.94, 112.89) * mm});
            skLineSegment(sketch, "E1183.MirrorCS", {"start": v(8.47, 139.23) * mm, "end": v(14.11, 139.23) * mm});
            skLineSegment(sketch, "E1184.MirrorCS", {"start": v(8.47, 139.23) * mm, "end": v(2.82, 139.23) * mm});
            skLineSegment(sketch, "E1185.MirrorCS", {"start": v(8.47, 143) * mm, "end": v(14.11, 143) * mm});
            skLineSegment(sketch, "E1186.MirrorCS", {"start": v(8.47, 150.52) * mm, "end": v(2.82, 150.52) * mm});
            skLineSegment(sketch, "E1187.MirrorCS", {"start": v(21.64, 141.11) * mm, "end": v(21.64, 152.4) * mm});
            skLineSegment(sketch, "E1188.MirrorCS", {"start": v(8.47, 105.36) * mm, "end": v(14.11, 105.36) * mm});
            skLineSegment(sketch, "E1189.MirrorCS", {"start": v(8.47, 120.41) * mm, "end": v(14.11, 120.41) * mm});
            skLineSegment(sketch, "E1190.MirrorCS", {"start": v(17.88, 129.82) * mm, "end": v(17.88, 135.47) * mm});
            skLineSegment(sketch, "E1191.MirrorCS", {"start": v(10.35, 129.82) * mm, "end": v(10.35, 135.47) * mm});
            skLineSegment(sketch, "E1192.MirrorCS", {"start": v(10.35, 141.11) * mm, "end": v(10.35, 152.4) * mm});
            skLineSegment(sketch, "E1193.MirrorCS", {"start": v(4.7, 107.24) * mm, "end": v(4.7, 118.53) * mm});
            skLineSegment(sketch, "E1194.MirrorCS", {"start": v(2.82, 114.77) * mm, "end": v(8.47, 114.77) * mm});
            skLineSegment(sketch, "E1195.MirrorCS", {"start": v(4.7, 141.11) * mm, "end": v(4.7, 135.47) * mm});
            skLineSegment(sketch, "E1196.MirrorCS", {"start": v(-14.11, 112.89) * mm, "end": v(-8.47, 112.89) * mm});
            skLineSegment(sketch, "E1197.MirrorCS", {"start": v(-25.4, 116.65) * mm, "end": v(-19.76, 116.65) * mm});
            skLineSegment(sketch, "E1198.MirrorCS", {"start": v(-2.82, 146.76) * mm, "end": v(-8.47, 146.76) * mm});
            skLineSegment(sketch, "E1199.MirrorCS", {"start": v(2.82, 107.24) * mm, "end": v(2.82, 101.6) * mm});
            skPoint(sketch, "E1200.MirrorP", {"position": v(2.82, 148.64) * mm});
            skLineSegment(sketch, "E1201.MirrorCS", {"start": v(-21.64, 107.24) * mm, "end": v(-21.64, 118.53) * mm});
            skLineSegment(sketch, "E1202.MirrorCS", {"start": v(0.94, 107.24) * mm, "end": v(0.94, 101.6) * mm});
            skLineSegment(sketch, "E1203.MirrorCS", {"start": v(14.11, 112.89) * mm, "end": v(8.47, 112.89) * mm});
            skLineSegment(sketch, "E1204.MirrorCS", {"start": v(12.23, 107.24) * mm, "end": v(12.23, 118.53) * mm});
            skLineSegment(sketch, "E1205.MirrorCS", {"start": v(8.47, 111) * mm, "end": v(14.11, 111) * mm});
            skLineSegment(sketch, "E1206.MirrorCS", {"start": v(8.47, 116.65) * mm, "end": v(14.11, 116.65) * mm});
            skLineSegment(sketch, "E1207.MirrorCS", {"start": v(-2.82, 139.23) * mm, "end": v(-8.47, 139.23) * mm});
            skLineSegment(sketch, "E1208.MirrorCS", {"start": v(14.11, 114.77) * mm, "end": v(8.47, 114.77) * mm});
            skLineSegment(sketch, "E1209.MirrorCS", {"start": v(0.94, 152.4) * mm, "end": v(0.94, 146.76) * mm});
            skLineSegment(sketch, "E1210.MirrorCS", {"start": v(-12.23, 107.24) * mm, "end": v(-12.23, 118.53) * mm});
            skLineSegment(sketch, "E1211.MirrorCS", {"start": v(-19.76, 120.41) * mm, "end": v(-14.11, 120.41) * mm});
            skLineSegment(sketch, "E1212.MirrorCS", {"start": v(-19.76, 103.49) * mm, "end": v(-8.47, 103.49) * mm});
            skLineSegment(sketch, "E1213.MirrorCS", {"start": v(-2.82, 109.12) * mm, "end": v(-8.47, 109.12) * mm});
            skLineSegment(sketch, "E1214.MirrorCS", {"start": v(8.47, 135.47) * mm, "end": v(8.47, 152.4) * mm});
            skLineSegment(sketch, "E1215.MirrorCS", {"start": v(-10.35, 141.11) * mm, "end": v(-10.35, 135.47) * mm});
            skLineSegment(sketch, "E1216.MirrorCS", {"start": v(2.82, 150.52) * mm, "end": v(-2.82, 150.52) * mm});
            skLineSegment(sketch, "E1217.MirrorCS", {"start": v(-14.11, 107.24) * mm, "end": v(-8.47, 107.24) * mm});
            skLineSegment(sketch, "E1218.MirrorCS", {"start": v(-14.11, 112.89) * mm, "end": v(-14.11, 118.53) * mm});
            skLineSegment(sketch, "E1219.MirrorCS", {"start": v(8.47, 133.58) * mm, "end": v(14.11, 133.58) * mm});
            skLineSegment(sketch, "E1220.MirrorCS", {"start": v(-25.4, 120.41) * mm, "end": v(-19.76, 120.41) * mm});
            skLineSegment(sketch, "E1221.MirrorCS", {"start": v(-17.87, 129.82) * mm, "end": v(-17.87, 135.47) * mm});
            skLineSegment(sketch, "E1222.MirrorCS", {"start": v(2.82, 139.23) * mm, "end": v(-2.82, 139.23) * mm});
            skLineSegment(sketch, "E1223.MirrorCS", {"start": v(-19.76, 141.11) * mm, "end": v(-19.76, 135.47) * mm});
            skLineSegment(sketch, "E1224.MirrorCS", {"start": v(8.47, 109.12) * mm, "end": v(2.82, 109.12) * mm});
            skLineSegment(sketch, "E1225.MirrorCS", {"start": v(8.47, 137.35) * mm, "end": v(2.82, 137.35) * mm});
            skLineSegment(sketch, "E1226.MirrorCS", {"start": v(-14.11, 139.23) * mm, "end": v(-8.47, 139.23) * mm});
            skLineSegment(sketch, "E1227.MirrorCS", {"start": v(-14.11, 141.11) * mm, "end": v(-8.47, 141.11) * mm});
            skLineSegment(sketch, "E1228.MirrorCS", {"start": v(10.35, 141.11) * mm, "end": v(10.35, 135.47) * mm});
            skLineSegment(sketch, "E1229.MirrorCS", {"start": v(-8.47, 148.64) * mm, "end": v(-2.82, 148.64) * mm});
            skLineSegment(sketch, "E1230.MirrorCS", {"start": v(0.94, 141.11) * mm, "end": v(0.94, 135.47) * mm});
            skLineSegment(sketch, "E1231.MirrorCS", {"start": v(6.59, 141.11) * mm, "end": v(6.59, 152.4) * mm});
            skLineSegment(sketch, "E1232.MirrorCS", {"start": v(8.47, 116.65) * mm, "end": v(2.82, 116.65) * mm});
            skLineSegment(sketch, "E1233.MirrorCS", {"start": v(-21.64, 129.82) * mm, "end": v(-21.64, 135.47) * mm});
            skLineSegment(sketch, "E1234.MirrorCS", {"start": v(-21.64, 141.11) * mm, "end": v(-21.64, 135.47) * mm});
            skLineSegment(sketch, "E1235.MirrorCS", {"start": v(2.82, 112.89) * mm, "end": v(8.47, 112.89) * mm});
            skLineSegment(sketch, "E1236.MirrorCS", {"start": v(4.7, 141.11) * mm, "end": v(4.7, 152.4) * mm});
            skLineSegment(sketch, "E1237.MirrorCS", {"start": v(-2.82, 141.11) * mm, "end": v(-8.47, 141.11) * mm});
            skLineSegment(sketch, "E1238.MirrorCS", {"start": v(-8.47, 144.87) * mm, "end": v(-2.82, 144.87) * mm});
            skLineSegment(sketch, "E1239.MirrorCS", {"start": v(8.47, 111) * mm, "end": v(2.82, 111) * mm});
            skLineSegment(sketch, "E1240.MirrorCS", {"start": v(-14.11, 141.11) * mm, "end": v(-14.11, 135.47) * mm});
            skLineSegment(sketch, "E1241.MirrorCS", {"start": v(-2.82, 116.65) * mm, "end": v(-8.47, 116.65) * mm});
            skLineSegment(sketch, "E1242.MirrorCS", {"start": v(-12.23, 141.11) * mm, "end": v(-12.23, 135.47) * mm});
            skLineSegment(sketch, "E1243.MirrorCS", {"start": v(-2.82, 148.64) * mm, "end": v(2.82, 148.64) * mm});
            skPoint(sketch, "E1244.MirrorP", {"position": v(2.82, 139.23) * mm});
            skLineSegment(sketch, "E1245.MirrorCS", {"start": v(19.76, 129.82) * mm, "end": v(19.76, 135.47) * mm});
            skLineSegment(sketch, "E1246.MirrorCS", {"start": v(-6.58, 107.24) * mm, "end": v(-6.58, 118.53) * mm});
            skLineSegment(sketch, "E1247.MirrorCS", {"start": v(-14.11, 109.12) * mm, "end": v(-8.47, 109.12) * mm});
            skLineSegment(sketch, "E1248.MirrorCS", {"start": v(-17.87, 141.11) * mm, "end": v(-17.87, 135.47) * mm});
            skLineSegment(sketch, "E1249.MirrorCS", {"start": v(-14.11, 143) * mm, "end": v(-8.47, 143) * mm});
            skLineSegment(sketch, "E1250.MirrorCS", {"start": v(8.47, 109.12) * mm, "end": v(14.11, 109.12) * mm});
            skLineSegment(sketch, "E1251.MirrorCS", {"start": v(-19.76, 129.82) * mm, "end": v(-19.76, 135.47) * mm});
            skLineSegment(sketch, "E1252.MirrorCS", {"start": v(-8.47, 111) * mm, "end": v(-2.82, 111) * mm});
            skLineSegment(sketch, "E1253.MirrorCS", {"start": v(-2.82, 143) * mm, "end": v(-8.47, 143) * mm});
            skLineSegment(sketch, "E1254.MirrorCS", {"start": v(4.7, 107.24) * mm, "end": v(4.7, 101.6) * mm});
            skLineSegment(sketch, "E1255.MirrorCS", {"start": v(-14.11, 105.36) * mm, "end": v(-8.47, 105.36) * mm});
            skLineSegment(sketch, "E1256.MirrorCS", {"start": v(17.88, 141.11) * mm, "end": v(17.88, 135.47) * mm});
            skLineSegment(sketch, "E1257.MirrorCS", {"start": v(2.82, 146.76) * mm, "end": v(2.82, 152.4) * mm});
            skLineSegment(sketch, "E1258.MirrorCS", {"start": v(8.47, 137.35) * mm, "end": v(14.11, 137.35) * mm});
            skLineSegment(sketch, "E1259.MirrorCS", {"start": v(6.59, 141.11) * mm, "end": v(6.59, 135.47) * mm});
            skLineSegment(sketch, "E1260.MirrorCS", {"start": v(2.82, 141.11) * mm, "end": v(2.82, 135.47) * mm});
            skLineSegment(sketch, "E1261.MirrorCS", {"start": v(8.47, 118.53) * mm, "end": v(8.47, 101.6) * mm});
            skLineSegment(sketch, "E1262.MirrorCS", {"start": v(12.23, 107.24) * mm, "end": v(12.23, 101.6) * mm});
            skLineSegment(sketch, "E1263.MirrorCS", {"start": v(-16, 129.82) * mm, "end": v(-16, 135.47) * mm});
            skLineSegment(sketch, "E1264.MirrorCS", {"start": v(-10.35, 129.82) * mm, "end": v(-10.35, 135.47) * mm});
            skLineSegment(sketch, "E1265.MirrorCS", {"start": v(16, 107.24) * mm, "end": v(16, 101.6) * mm});
            skLineSegment(sketch, "E1266.MirrorCS", {"start": v(8.47, 103.49) * mm, "end": v(14.11, 103.49) * mm});
            skLineSegment(sketch, "E1267.MirrorCS", {"start": v(-19.76, 141.11) * mm, "end": v(-25.4, 141.11) * mm});
            skLineSegment(sketch, "E1268.MirrorCS", {"start": v(-25.4, 127.94) * mm, "end": v(-19.76, 127.94) * mm});
            skLineSegment(sketch, "E1269.MirrorCS", {"start": v(-8.47, 118.53) * mm, "end": v(-25.4, 118.53) * mm});
            skLineSegment(sketch, "E1270.MirrorCS", {"start": v(14.11, 137.35) * mm, "end": v(25.4, 137.35) * mm});
            skLineSegment(sketch, "E1271.MirrorCS", {"start": v(21.64, 129.82) * mm, "end": v(21.64, 118.53) * mm});
            skLineSegment(sketch, "E1272.MirrorCS", {"start": v(-16, 141.11) * mm, "end": v(-16, 135.47) * mm});
            skLineSegment(sketch, "E1273.MirrorCS", {"start": v(-6.58, 141.11) * mm, "end": v(-6.58, 135.47) * mm});
            skLineSegment(sketch, "E1274.MirrorCS", {"start": v(23.51, 141.11) * mm, "end": v(23.51, 135.47) * mm});
            skLineSegment(sketch, "E1275.MirrorCS", {"start": v(10.35, 107.24) * mm, "end": v(10.35, 101.6) * mm});
            skLineSegment(sketch, "E1276.MirrorCS", {"start": v(19.76, 146.76) * mm, "end": v(25.4, 146.76) * mm});
            skLineSegment(sketch, "E1277.MirrorCS", {"start": v(6.59, 107.24) * mm, "end": v(6.59, 101.6) * mm});
            skLineSegment(sketch, "E1278.MirrorCS", {"start": v(-14.11, 148.64) * mm, "end": v(-19.76, 148.64) * mm});
            skLineSegment(sketch, "E1279.MirrorCS", {"start": v(-25.4, 139.23) * mm, "end": v(-19.76, 139.23) * mm});
            skLineSegment(sketch, "E1280.MirrorCS", {"start": v(-2.82, 150.52) * mm, "end": v(-8.47, 150.52) * mm});
            skLineSegment(sketch, "E1281.MirrorCS", {"start": v(-19.76, 139.23) * mm, "end": v(-14.11, 139.23) * mm});
            skLineSegment(sketch, "E1282.MirrorCS", {"start": v(-14.11, 120.41) * mm, "end": v(-8.47, 120.41) * mm});
            skLineSegment(sketch, "E1283.MirrorCS", {"start": v(8.47, 103.49) * mm, "end": v(2.82, 103.49) * mm});
            skLineSegment(sketch, "E1284.MirrorCS", {"start": v(-14.11, 116.65) * mm, "end": v(-8.47, 116.65) * mm});
            skLineSegment(sketch, "E1285.MirrorCS", {"start": v(-14.11, 124.18) * mm, "end": v(-14.11, 118.53) * mm});
            skLineSegment(sketch, "E1286.MirrorCS", {"start": v(23.51, 129.82) * mm, "end": v(23.51, 135.47) * mm});
            skPoint(sketch, "E1287.MirrorP", {"position": v(-2.82, 139.23) * mm});
            skLineSegment(sketch, "E1288.MirrorCS", {"start": v(-4.7, 107.24) * mm, "end": v(-4.7, 118.53) * mm});
            skLineSegment(sketch, "E1289.MirrorCS", {"start": v(2.82, 137.35) * mm, "end": v(-8.47, 137.35) * mm});
            skLineSegment(sketch, "E1290.MirrorCS", {"start": v(-0.94, 141.11) * mm, "end": v(-0.94, 135.47) * mm});
            skLineSegment(sketch, "E1291.MirrorCS", {"start": v(12.23, 129.82) * mm, "end": v(12.23, 118.53) * mm});
            skLineSegment(sketch, "E1292.MirrorCS", {"start": v(-19.76, 131.7) * mm, "end": v(-14.11, 131.7) * mm});
            skLineSegment(sketch, "E1293.MirrorCS", {"start": v(-25.4, 109.12) * mm, "end": v(-19.76, 109.12) * mm});
            skLineSegment(sketch, "E1294.MirrorCS", {"start": v(-0.94, 146.76) * mm, "end": v(-0.94, 152.4) * mm});
            skLineSegment(sketch, "E1295.MirrorCS", {"start": v(-14.11, 129.82) * mm, "end": v(-8.47, 129.82) * mm});
            skLineSegment(sketch, "E1296.MirrorCS", {"start": v(-14.11, 129.82) * mm, "end": v(-14.11, 135.47) * mm});
            skLineSegment(sketch, "E1297.MirrorCS", {"start": v(8.47, 144.87) * mm, "end": v(2.82, 144.87) * mm});
            skLineSegment(sketch, "E1298.MirrorCS", {"start": v(-23.52, 129.82) * mm, "end": v(-23.52, 135.47) * mm});
            skLineSegment(sketch, "E1299.MirrorCS", {"start": v(14.11, 133.58) * mm, "end": v(25.4, 133.58) * mm});
            skLineSegment(sketch, "E1300.MirrorCS", {"start": v(-25.4, 131.7) * mm, "end": v(-19.76, 131.7) * mm});
            skLineSegment(sketch, "E1301.MirrorCS", {"start": v(10.35, 129.82) * mm, "end": v(10.35, 118.53) * mm});
            skLineSegment(sketch, "E1302.MirrorCS", {"start": v(21.64, 107.24) * mm, "end": v(21.64, 118.53) * mm});
            skLineSegment(sketch, "E1303.MirrorCS", {"start": v(-4.7, 141.11) * mm, "end": v(-4.7, 152.4) * mm});
            skLineSegment(sketch, "E1304.MirrorCS", {"start": v(-8.47, 114.77) * mm, "end": v(-2.82, 114.77) * mm});
            skLineSegment(sketch, "E1305.MirrorCS", {"start": v(19.76, 141.11) * mm, "end": v(25.4, 141.11) * mm});
            skLineSegment(sketch, "E1306.MirrorCS", {"start": v(19.76, 143) * mm, "end": v(25.4, 143) * mm});
            skLineSegment(sketch, "E1307.MirrorCS", {"start": v(25.4, 144.87) * mm, "end": v(19.76, 144.87) * mm});
            skLineSegment(sketch, "E1308.MirrorCS", {"start": v(-19.76, 107.24) * mm, "end": v(-25.4, 107.24) * mm});
            skLineSegment(sketch, "E1309.MirrorCS", {"start": v(-19.76, 129.82) * mm, "end": v(-25.4, 129.82) * mm});
            skLineSegment(sketch, "E1310.MirrorCS", {"start": v(-19.76, 133.58) * mm, "end": v(-8.47, 133.58) * mm});
            skLineSegment(sketch, "E1311.MirrorCS", {"start": v(8.47, 135.47) * mm, "end": v(25.4, 135.47) * mm});
            skLineSegment(sketch, "E1312.MirrorCS", {"start": v(-14.11, 131.7) * mm, "end": v(-8.47, 131.7) * mm});
            skLineSegment(sketch, "E1313.MirrorCS", {"start": v(-12.23, 129.82) * mm, "end": v(-12.23, 135.47) * mm});
            skLineSegment(sketch, "E1314.MirrorCS", {"start": v(-25.4, 105.36) * mm, "end": v(-19.76, 105.36) * mm});
            skLineSegment(sketch, "E1315.MirrorCS", {"start": v(-2.82, 146.76) * mm, "end": v(-2.82, 152.4) * mm});
            skLineSegment(sketch, "E1316.MirrorCS", {"start": v(-19.76, 137.35) * mm, "end": v(-8.47, 137.35) * mm});
            skLineSegment(sketch, "E1317.MirrorCS", {"start": v(14.11, 107.24) * mm, "end": v(14.11, 101.6) * mm});
            skLineSegment(sketch, "E1318.MirrorCS", {"start": v(-14.11, 127.94) * mm, "end": v(-8.47, 127.94) * mm});
            skLineSegment(sketch, "E1319.MirrorCS", {"start": v(19.76, 139.23) * mm, "end": v(25.4, 139.23) * mm});
            skLineSegment(sketch, "E1320.MirrorCS", {"start": v(-25.4, 143) * mm, "end": v(-19.76, 143) * mm});
            skLineSegment(sketch, "E1321.MirrorCS", {"start": v(-16, 124.18) * mm, "end": v(-16, 118.53) * mm});
            skLineSegment(sketch, "E1322.MirrorCS", {"start": v(-14.11, 150.52) * mm, "end": v(-8.47, 150.52) * mm});
            skLineSegment(sketch, "E1323.MirrorCS", {"start": v(-4.7, 141.11) * mm, "end": v(-4.7, 135.47) * mm});
            skLineSegment(sketch, "E1324.MirrorCS", {"start": v(-16, 146.76) * mm, "end": v(-16, 152.4) * mm});
            skLineSegment(sketch, "E1325.MirrorCS", {"start": v(-14.11, 122.3) * mm, "end": v(-19.76, 122.3) * mm});
            skLineSegment(sketch, "E1326.MirrorCS", {"start": v(-8.47, 135.47) * mm, "end": v(-25.4, 135.47) * mm});
            skLineSegment(sketch, "E1327.MirrorCS", {"start": v(-19.76, 124.18) * mm, "end": v(-19.76, 118.53) * mm});
            skLineSegment(sketch, "E1328.MirrorCS", {"start": v(-0.94, 107.24) * mm, "end": v(-0.94, 101.6) * mm});
            skLineSegment(sketch, "E1329.MirrorCS", {"start": v(-6.58, 141.11) * mm, "end": v(-6.58, 152.4) * mm});
            skLineSegment(sketch, "E1330.MirrorCS", {"start": v(19.76, 127.94) * mm, "end": v(25.4, 127.94) * mm});
            skLineSegment(sketch, "E1331.MirrorCS", {"start": v(19.76, 105.36) * mm, "end": v(25.4, 105.36) * mm});
            skLineSegment(sketch, "E1332.MirrorCS", {"start": v(-19.76, 146.76) * mm, "end": v(-19.76, 152.4) * mm});
            skLineSegment(sketch, "E1333.MirrorCS", {"start": v(-8.47, 126.06) * mm, "end": v(-14.11, 126.06) * mm});
            skLineSegment(sketch, "E1334.MirrorCS", {"start": v(-23.52, 141.11) * mm, "end": v(-23.52, 135.47) * mm});
            skLineSegment(sketch, "E1335.MirrorCS", {"start": v(-2.82, 107.24) * mm, "end": v(-2.82, 101.6) * mm});
            skLineSegment(sketch, "E1336.MirrorCS", {"start": v(-21.64, 129.82) * mm, "end": v(-21.64, 118.53) * mm});
            skLineSegment(sketch, "E1337.MirrorCS", {"start": v(-17.88, 118.53) * mm, "end": v(-17.88, 124.18) * mm});
            skLineSegment(sketch, "E1338.MirrorCS", {"start": v(25.4, 126.06) * mm, "end": v(19.76, 126.06) * mm});
            skLineSegment(sketch, "E1339.MirrorCS", {"start": v(17.88, 107.24) * mm, "end": v(17.88, 101.6) * mm});
            skLineSegment(sketch, "E1340.MirrorCS", {"start": v(-14.11, 124.18) * mm, "end": v(-8.47, 124.18) * mm});
            skLineSegment(sketch, "E1341.MirrorCS", {"start": v(19.76, 131.7) * mm, "end": v(25.4, 131.7) * mm});
            skLineSegment(sketch, "E1342.MirrorCS", {"start": v(-25.4, 137.35) * mm, "end": v(-19.76, 137.35) * mm});
            skLineSegment(sketch, "E1343.MirrorCS", {"start": v(-16, 107.24) * mm, "end": v(-16, 101.6) * mm});
            skLineSegment(sketch, "E1344.MirrorCS", {"start": v(-12.23, 129.82) * mm, "end": v(-12.23, 118.53) * mm});
            skLineSegment(sketch, "E1345.MirrorCS", {"start": v(23.51, 107.24) * mm, "end": v(23.51, 118.53) * mm});
            skLineSegment(sketch, "E1346.MirrorCS", {"start": v(14.11, 124.18) * mm, "end": v(8.47, 124.18) * mm});
            skLineSegment(sketch, "E1347.MirrorCS", {"start": v(-14.11, 146.76) * mm, "end": v(-14.11, 152.4) * mm});
            skLineSegment(sketch, "E1348.MirrorCS", {"start": v(25.4, 148.64) * mm, "end": v(19.76, 148.64) * mm});
            skLineSegment(sketch, "E1349.MirrorCS", {"start": v(25.4, 114.77) * mm, "end": v(19.76, 114.77) * mm});
            skLineSegment(sketch, "E1350.MirrorCS", {"start": v(-10.35, 107.24) * mm, "end": v(-10.35, 101.6) * mm});
            skLineSegment(sketch, "E1351.MirrorCS", {"start": v(-17.88, 152.4) * mm, "end": v(-17.88, 146.76) * mm});
            skLineSegment(sketch, "E1352.MirrorCS", {"start": v(-21.64, 141.11) * mm, "end": v(-21.64, 152.4) * mm});
            skLineSegment(sketch, "E1353.MirrorCS", {"start": v(19.76, 112.89) * mm, "end": v(25.4, 112.89) * mm});
            skLineSegment(sketch, "E1354.MirrorCS", {"start": v(19.76, 116.65) * mm, "end": v(25.4, 116.65) * mm});
            skLineSegment(sketch, "E1355.MirrorCS", {"start": v(-2.82, 141.11) * mm, "end": v(-2.82, 135.47) * mm});
            skLineSegment(sketch, "E1356.MirrorCS", {"start": v(19.76, 109.12) * mm, "end": v(25.4, 109.12) * mm});
            skLineSegment(sketch, "E1357.MirrorCS", {"start": v(19.76, 124.18) * mm, "end": v(25.4, 124.18) * mm});
            skLineSegment(sketch, "E1358.MirrorCS", {"start": v(14.11, 103.49) * mm, "end": v(25.4, 103.49) * mm});
            skLineSegment(sketch, "E1359.MirrorCS", {"start": v(25.4, 111) * mm, "end": v(19.76, 111) * mm});
            skLineSegment(sketch, "E1360.MirrorCS", {"start": v(19.76, 107.24) * mm, "end": v(25.4, 107.24) * mm});
            skPoint(sketch, "E1361.MirrorP", {"position": v(25.4, 139.23) * mm});
            skLineSegment(sketch, "E1362.MirrorCS", {"start": v(-17.87, 107.24) * mm, "end": v(-17.87, 101.6) * mm});
            skPoint(sketch, "E1363.MirrorP", {"position": v(-8.47, 139.23) * mm});
            skLineSegment(sketch, "E1364.MirrorCS", {"start": v(-6.58, 107.24) * mm, "end": v(-6.58, 101.6) * mm});
            skLineSegment(sketch, "E1365.MirrorCS", {"start": v(21.64, 107.24) * mm, "end": v(21.64, 101.6) * mm});
            skLineSegment(sketch, "E1366.MirrorCS", {"start": v(-25.4, 133.58) * mm, "end": v(-19.76, 133.58) * mm});
            skLineSegment(sketch, "E1367.MirrorCS", {"start": v(19.76, 107.24) * mm, "end": v(19.76, 101.6) * mm});
            skLineSegment(sketch, "E1368.MirrorCS", {"start": v(8.47, 118.53) * mm, "end": v(25.4, 118.53) * mm});
            skLineSegment(sketch, "E1369.MirrorCS", {"start": v(-21.64, 107.24) * mm, "end": v(-21.64, 101.6) * mm});
            skLineSegment(sketch, "E1370.MirrorCS", {"start": v(21.64, 141.11) * mm, "end": v(21.64, 135.47) * mm});
            skLineSegment(sketch, "E1371.MirrorCS", {"start": v(8.47, 126.06) * mm, "end": v(14.11, 126.06) * mm});
            skLineSegment(sketch, "E1372.MirrorCS", {"start": v(-12.23, 141.11) * mm, "end": v(-12.23, 152.4) * mm});
            skLineSegment(sketch, "E1373.MirrorCS", {"start": v(-8.47, 118.53) * mm, "end": v(-8.47, 101.6) * mm});
            skLineSegment(sketch, "E1374.MirrorCS", {"start": v(23.51, 141.11) * mm, "end": v(23.51, 152.4) * mm});
            skLineSegment(sketch, "E1375.MirrorCS", {"start": v(-19.76, 150.52) * mm, "end": v(-14.11, 150.52) * mm});
            skLineSegment(sketch, "E1376.MirrorCS", {"start": v(-19.76, 107.24) * mm, "end": v(-19.76, 101.6) * mm});
            skLineSegment(sketch, "E1377.MirrorCS", {"start": v(19.76, 129.82) * mm, "end": v(25.4, 129.82) * mm});
            skLineSegment(sketch, "E1378.MirrorCS", {"start": v(14.11, 122.3) * mm, "end": v(8.47, 122.3) * mm});
            skLineSegment(sketch, "E1379.MirrorCS", {"start": v(19.76, 120.41) * mm, "end": v(25.4, 120.41) * mm});
            skLineSegment(sketch, "E1380.MirrorCS", {"start": v(-14.11, 146.76) * mm, "end": v(-8.47, 146.76) * mm});
            skLineSegment(sketch, "E1381.MirrorCS", {"start": v(21.64, 129.82) * mm, "end": v(21.64, 135.47) * mm});
            skPoint(sketch, "E1382.MirrorP", {"position": v(2.82, 144.87) * mm});
            skLineSegment(sketch, "E1383.MirrorCS", {"start": v(-8.47, 135.47) * mm, "end": v(-8.47, 152.4) * mm});
            skLineSegment(sketch, "E1384.MirrorCS", {"start": v(19.76, 150.52) * mm, "end": v(25.4, 150.52) * mm});
            skLineSegment(sketch, "E1385.MirrorCS", {"start": v(-25.4, 150.52) * mm, "end": v(-19.76, 150.52) * mm});
            skPoint(sketch, "E1386.MirrorP", {"position": v(25.4, 144.87) * mm});
            skLineSegment(sketch, "E1387.MirrorCS", {"start": v(-23.52, 129.82) * mm, "end": v(-23.52, 118.53) * mm});
            skLineSegment(sketch, "E1388.MirrorCS", {"start": v(-12.23, 107.24) * mm, "end": v(-12.23, 101.6) * mm});
            skPoint(sketch, "E1389.MirrorP", {"position": v(-8.47, 131.7) * mm});
            skLineSegment(sketch, "E1390.MirrorCS", {"start": v(23.51, 107.24) * mm, "end": v(23.51, 101.6) * mm});
            skLineSegment(sketch, "E1391.MirrorCS", {"start": v(-23.52, 141.11) * mm, "end": v(-23.52, 152.4) * mm});
            skLineSegment(sketch, "E1392.MirrorCS", {"start": v(-23.52, 107.24) * mm, "end": v(-23.52, 118.53) * mm});
            skLineSegment(sketch, "E1393.MirrorCS", {"start": v(25.4, 122.3) * mm, "end": v(19.76, 122.3) * mm});
            skLineSegment(sketch, "E1394.MirrorCS", {"start": v(-8.47, 122.3) * mm, "end": v(-14.11, 122.3) * mm});
            skLineSegment(sketch, "E1395.MirrorCS", {"start": v(-8.47, 144.87) * mm, "end": v(-14.11, 144.87) * mm});
            skLineSegment(sketch, "E1396.MirrorCS", {"start": v(-8.47, 114.77) * mm, "end": v(-14.11, 114.77) * mm});
            skLineSegment(sketch, "E1397.MirrorCS", {"start": v(23.51, 129.82) * mm, "end": v(23.51, 118.53) * mm});
            skLineSegment(sketch, "E1398.MirrorCS", {"start": v(-14.11, 107.24) * mm, "end": v(-14.11, 101.6) * mm});
            skLineSegment(sketch, "E1399.MirrorCS", {"start": v(-25.4, 101.6) * mm, "end": v(25.4, 101.6) * mm});
            skLineSegment(sketch, "E1400.MirrorCS", {"start": v(-25.4, 103.49) * mm, "end": v(-19.76, 103.49) * mm});
            skLineSegment(sketch, "E1401.MirrorCS", {"start": v(-4.7, 107.24) * mm, "end": v(-4.7, 101.6) * mm});
            skLineSegment(sketch, "E1402.MirrorCS", {"start": v(-10.35, 141.11) * mm, "end": v(-10.35, 152.4) * mm});
            skPoint(sketch, "E1403.MirrorP", {"position": v(-8.47, 126.06) * mm});
            skLineSegment(sketch, "E1404.MirrorCS", {"start": v(-23.52, 107.24) * mm, "end": v(-23.52, 101.6) * mm});
            skLineSegment(sketch, "E1405.MirrorCS", {"start": v(-19.76, 122.3) * mm, "end": v(-25.4, 122.3) * mm});
            skLineSegment(sketch, "E1406.MirrorCS", {"start": v(-10.35, 107.24) * mm, "end": v(-10.35, 118.53) * mm});
            skLineSegment(sketch, "E1407.MirrorCS", {"start": v(-8.47, 148.64) * mm, "end": v(-14.11, 148.64) * mm});
            skPoint(sketch, "E1408.MirrorP", {"position": v(-8.47, 144.87) * mm});
            skLineSegment(sketch, "E1409.MirrorCS", {"start": v(-19.76, 124.18) * mm, "end": v(-25.4, 124.18) * mm});
            skLineSegment(sketch, "E1410.MirrorCS", {"start": v(-19.76, 148.64) * mm, "end": v(-25.4, 148.64) * mm});
            skLineSegment(sketch, "E1411.MirrorCS", {"start": v(-10.35, 129.82) * mm, "end": v(-10.35, 118.53) * mm});
            skLineSegment(sketch, "E1412.MirrorCS", {"start": v(-25.4, 111) * mm, "end": v(-19.76, 111) * mm});
            skPoint(sketch, "E1413.MirrorP", {"position": v(8.47, 101.6) * mm});
            skLineSegment(sketch, "E1414.MirrorCS", {"start": v(-19.76, 146.76) * mm, "end": v(-25.4, 146.76) * mm});
            skLineSegment(sketch, "E1415.MirrorCS", {"start": v(-19.76, 112.89) * mm, "end": v(-25.4, 112.89) * mm});
            skLineSegment(sketch, "E1416.MirrorCS", {"start": v(-25.4, 144.87) * mm, "end": v(-19.76, 144.87) * mm});
            skLineSegment(sketch, "E1417.MirrorCS", {"start": v(-19.76, 114.77) * mm, "end": v(-25.4, 114.77) * mm});
            skLineSegment(sketch, "E1418.MirrorCS", {"start": v(-25.4, 126.06) * mm, "end": v(-19.76, 126.06) * mm});
            skLineSegment(sketch, "E1419", {"start": v(25.4, 101.6) * mm, "end": v(25.4, 152.4) * mm});
            skSolve(sketch);
        }
        {
            var Q0;
            {var subQ0=sQuery(id+"F20.wireOp",EDGE,"E1072.MirrorCS");var subQ1=sQuery(id+"F20.wireOp",EDGE,"E1079.MirrorCS");var subQ2=makeQuery(id+"F20.imprint","INTERSECT",VERTEX,{"derivedFrom":[subQ1,subQ0]});Q0=makeQuery(id+"F20.imprint","IMPRINT",FACE,{"disambiguationData":[TD([[makeQuery(id+"F20.imprint","IMPRINT",EDGE,{"disambiguationData":[TD([[subQ2,-1.0]])],"derivedFrom":subQ1}),-1.0]])]});}
            var Q1;
            {var subQ0=sQuery(id+"F20.wireOp",EDGE,"E1095.MirrorCS");var subQ1=sQuery(id+"F20.wireOp",EDGE,"E1091.MirrorCS");var subQ2=makeQuery(id+"F20.imprint","INTERSECT",VERTEX,{"derivedFrom":[subQ1,subQ0]});Q1=makeQuery(id+"F20.imprint","IMPRINT",FACE,{"disambiguationData":[TD([[makeQuery(id+"F20.imprint","IMPRINT",EDGE,{"disambiguationData":[TD([[subQ2,-1.0]])],"derivedFrom":subQ1}),1.0]])]});}
            var Q2;
            {var subQ0=sQuery(id+"F20.wireOp",EDGE,"E1108.MirrorCS");var subQ1=sQuery(id+"F20.wireOp",EDGE,"E1082.MirrorCS");var subQ2=makeQuery(id+"F20.imprint","INTERSECT",VERTEX,{"derivedFrom":[subQ1,subQ0]});Q2=makeQuery(id+"F20.imprint","IMPRINT",FACE,{"disambiguationData":[TD([[makeQuery(id+"F20.imprint","IMPRINT",EDGE,{"disambiguationData":[TD([[subQ2,-1.0]])],"derivedFrom":subQ1}),-1.0]])]});}
            var Q3;
            {var subQ0=sQuery(id+"F20.wireOp",EDGE,"E1106.MirrorCS");var subQ1=sQuery(id+"F20.wireOp",EDGE,"E1082.MirrorCS");var subQ2=makeQuery(id+"F20.imprint","INTERSECT",VERTEX,{"derivedFrom":[subQ1,subQ0]});Q3=makeQuery(id+"F20.imprint","IMPRINT",FACE,{"disambiguationData":[TD([[makeQuery(id+"F20.imprint","IMPRINT",EDGE,{"disambiguationData":[TD([[subQ2,-1.0]])],"derivedFrom":subQ1}),-1.0]])]});}
            var Q4;
            {var subQ0=sQuery(id+"F20.wireOp",EDGE,"E1059.MirrorCS");var subQ1=sQuery(id+"F20.wireOp",EDGE,"E1053.MirrorCS");var subQ2=makeQuery(id+"F20.imprint","INTERSECT",VERTEX,{"derivedFrom":[subQ1,subQ0]});Q4=makeQuery(id+"F20.imprint","IMPRINT",FACE,{"disambiguationData":[TD([[makeQuery(id+"F20.imprint","IMPRINT",EDGE,{"disambiguationData":[TD([[subQ2,-1.0]])],"derivedFrom":subQ1}),-1.0]])]});}
            var Q5;
            {var subQ0=sQuery(id+"F20.wireOp",EDGE,"E1067.MirrorCS");var subQ1=sQuery(id+"F20.wireOp",EDGE,"E1033.MirrorCS");var subQ2=makeQuery(id+"F20.imprint","INTERSECT",VERTEX,{"derivedFrom":[subQ1,subQ0]});Q5=makeQuery(id+"F20.imprint","IMPRINT",FACE,{"disambiguationData":[TD([[makeQuery(id+"F20.imprint","IMPRINT",EDGE,{"disambiguationData":[TD([[subQ2,-1.0]])],"derivedFrom":subQ1}),-1.0]])]});}
            var Q6;
            {var subQ0=sQuery(id+"F20.wireOp",EDGE,"E1060.MirrorCS");var subQ1=sQuery(id+"F20.wireOp",EDGE,"E1043.MirrorCS");var subQ2=makeQuery(id+"F20.imprint","INTERSECT",VERTEX,{"derivedFrom":[subQ1,subQ0]});Q6=makeQuery(id+"F20.imprint","IMPRINT",FACE,{"disambiguationData":[TD([[makeQuery(id+"F20.imprint","IMPRINT",EDGE,{"disambiguationData":[TD([[subQ2,-1.0]])],"derivedFrom":subQ1}),-1.0]])]});}
            var Q7;
            {var subQ0=sQuery(id+"F20.wireOp",EDGE,"E1041.MirrorCS");var subQ1=sQuery(id+"F20.wireOp",EDGE,"E1045.MirrorCS");var subQ2=makeQuery(id+"F20.imprint","INTERSECT",VERTEX,{"derivedFrom":[subQ1,subQ0]});Q7=makeQuery(id+"F20.imprint","IMPRINT",FACE,{"disambiguationData":[TD([[makeQuery(id+"F20.imprint","IMPRINT",EDGE,{"disambiguationData":[TD([[subQ2,-1.0]])],"derivedFrom":subQ1}),-1.0]])]});}
            var Q8;
            {var subQ0=sQuery(id+"F20.wireOp",EDGE,"E1041.MirrorCS");var subQ1=sQuery(id+"F20.wireOp",EDGE,"E1047.MirrorCS");var subQ2=makeQuery(id+"F20.imprint","INTERSECT",VERTEX,{"derivedFrom":[subQ1,subQ0]});Q8=makeQuery(id+"F20.imprint","IMPRINT",FACE,{"disambiguationData":[TD([[makeQuery(id+"F20.imprint","IMPRINT",EDGE,{"disambiguationData":[TD([[subQ2,-1.0]])],"derivedFrom":subQ1}),-1.0]])]});}
            var Q9;
            {var subQ0=sQuery(id+"F20.wireOp",EDGE,"E1052.MirrorCS");var subQ1=sQuery(id+"F20.wireOp",EDGE,"E1035.MirrorCS");var subQ2=makeQuery(id+"F20.imprint","INTERSECT",VERTEX,{"derivedFrom":[subQ1,subQ0]});Q9=makeQuery(id+"F20.imprint","IMPRINT",FACE,{"disambiguationData":[TD([[makeQuery(id+"F20.imprint","IMPRINT",EDGE,{"disambiguationData":[TD([[subQ2,-1.0]])],"derivedFrom":subQ1}),-1.0]])]});}
            var Q10;
            {var subQ0=sQuery(id+"F20.wireOp",EDGE,"E1044.MirrorCS");var subQ1=sQuery(id+"F20.wireOp",EDGE,"E1042.MirrorCS");var subQ2=makeQuery(id+"F20.imprint","INTERSECT",VERTEX,{"derivedFrom":[subQ1,subQ0]});Q10=makeQuery(id+"F20.imprint","IMPRINT",FACE,{"disambiguationData":[TD([[makeQuery(id+"F20.imprint","IMPRINT",EDGE,{"disambiguationData":[TD([[subQ2,-1.0]])],"derivedFrom":subQ1}),-1.0]])]});}
            var Q11;
            {var subQ0=sQuery(id+"F20.wireOp",EDGE,"E1046.MirrorCS");var subQ1=sQuery(id+"F20.wireOp",EDGE,"E1044.MirrorCS");var subQ2=makeQuery(id+"F20.imprint","INTERSECT",VERTEX,{"derivedFrom":[subQ1,subQ0]});Q11=makeQuery(id+"F20.imprint","IMPRINT",FACE,{"disambiguationData":[TD([[makeQuery(id+"F20.imprint","IMPRINT",EDGE,{"disambiguationData":[TD([[subQ2,-1.0]])],"derivedFrom":subQ1}),1.0]])]});}
            var Q12;
            {var subQ0=sQuery(id+"F20.wireOp",EDGE,"E879.MirrorCS");var subQ1=sQuery(id+"F20.wireOp",EDGE,"E874.MirrorCS");var subQ2=makeQuery(id+"F20.imprint","INTERSECT",VERTEX,{"derivedFrom":[subQ1,subQ0]});Q12=makeQuery(id+"F20.imprint","IMPRINT",FACE,{"disambiguationData":[TD([[makeQuery(id+"F20.imprint","IMPRINT",EDGE,{"disambiguationData":[TD([[subQ2,-1.0]])],"derivedFrom":subQ1}),1.0]])]});}
            var Q13;
            {var subQ0=sQuery(id+"F20.wireOp",EDGE,"E887.MirrorCS");var subQ1=sQuery(id+"F20.wireOp",EDGE,"E856.MirrorCS");var subQ2=makeQuery(id+"F20.imprint","INTERSECT",VERTEX,{"derivedFrom":[subQ1,subQ0]});Q13=makeQuery(id+"F20.imprint","IMPRINT",FACE,{"disambiguationData":[TD([[makeQuery(id+"F20.imprint","IMPRINT",EDGE,{"disambiguationData":[TD([[subQ2,-1.0]])],"derivedFrom":subQ1}),-1.0]])]});}
            var Q14;
            {var subQ0=sQuery(id+"F20.wireOp",EDGE,"E856.MirrorCS");var subQ1=sQuery(id+"F20.wireOp",EDGE,"E854.MirrorCS");var subQ2=makeQuery(id+"F20.imprint","INTERSECT",VERTEX,{"derivedFrom":[subQ1,subQ0]});Q14=makeQuery(id+"F20.imprint","IMPRINT",FACE,{"disambiguationData":[TD([[makeQuery(id+"F20.imprint","IMPRINT",EDGE,{"disambiguationData":[TD([[subQ2,-1.0]])],"derivedFrom":subQ1}),1.0]])]});}
            var Q15;
            {var subQ0=sQuery(id+"F20.wireOp",EDGE,"E862.MirrorCS");var subQ1=sQuery(id+"F20.wireOp",EDGE,"E859.MirrorCS");var subQ2=makeQuery(id+"F20.imprint","INTERSECT",VERTEX,{"derivedFrom":[subQ1,subQ0]});Q15=makeQuery(id+"F20.imprint","IMPRINT",FACE,{"disambiguationData":[TD([[makeQuery(id+"F20.imprint","IMPRINT",EDGE,{"disambiguationData":[TD([[subQ2,-1.0]])],"derivedFrom":subQ1}),-1.0]])]});}
            var Q16;
            {var subQ0=sQuery(id+"F20.wireOp",EDGE,"E866.MirrorCS");var subQ1=sQuery(id+"F20.wireOp",EDGE,"E863.MirrorCS");var subQ2=makeQuery(id+"F20.imprint","INTERSECT",VERTEX,{"derivedFrom":[subQ1,subQ0]});Q16=makeQuery(id+"F20.imprint","IMPRINT",FACE,{"disambiguationData":[TD([[makeQuery(id+"F20.imprint","IMPRINT",EDGE,{"disambiguationData":[TD([[subQ2,-1.0]])],"derivedFrom":subQ1}),1.0]])]});}
            var Q17;
            {var subQ0=sQuery(id+"F20.wireOp",EDGE,"E870.MirrorCS");var subQ1=sQuery(id+"F20.wireOp",EDGE,"E865.MirrorCS");var subQ2=makeQuery(id+"F20.imprint","INTERSECT",VERTEX,{"derivedFrom":[subQ1,subQ0]});Q17=makeQuery(id+"F20.imprint","IMPRINT",FACE,{"disambiguationData":[TD([[makeQuery(id+"F20.imprint","IMPRINT",EDGE,{"disambiguationData":[TD([[subQ2,-1.0]])],"derivedFrom":subQ1}),-1.0]])]});}
            var Q18;
            {var subQ0=sQuery(id+"F20.wireOp",EDGE,"E885.MirrorCS");var subQ1=sQuery(id+"F20.wireOp",EDGE,"E872.MirrorCS");var subQ2=makeQuery(id+"F20.imprint","INTERSECT",VERTEX,{"derivedFrom":[subQ1,subQ0]});Q18=makeQuery(id+"F20.imprint","IMPRINT",FACE,{"disambiguationData":[TD([[makeQuery(id+"F20.imprint","IMPRINT",EDGE,{"disambiguationData":[TD([[subQ2,-1.0]])],"derivedFrom":subQ1}),1.0]])]});}
            var Q19;
            {var subQ0=sQuery(id+"F20.wireOp",EDGE,"E882.MirrorCS");var subQ1=sQuery(id+"F20.wireOp",EDGE,"E876.MirrorCS");var subQ2=makeQuery(id+"F20.imprint","INTERSECT",VERTEX,{"derivedFrom":[subQ1,subQ0]});Q19=makeQuery(id+"F20.imprint","IMPRINT",FACE,{"disambiguationData":[TD([[makeQuery(id+"F20.imprint","IMPRINT",EDGE,{"disambiguationData":[TD([[subQ2,-1.0]])],"derivedFrom":subQ1}),1.0]])]});}
            var Q20;
            {var subQ0=sQuery(id+"F20.wireOp",EDGE,"E920.MirrorCS");var subQ1=sQuery(id+"F20.wireOp",EDGE,"E899.MirrorCS");var subQ2=makeQuery(id+"F20.imprint","INTERSECT",VERTEX,{"derivedFrom":[subQ1,subQ0]});Q20=makeQuery(id+"F20.imprint","IMPRINT",FACE,{"disambiguationData":[TD([[makeQuery(id+"F20.imprint","IMPRINT",EDGE,{"disambiguationData":[TD([[subQ2,-1.0]])],"derivedFrom":subQ1}),1.0]])]});}
            var Q21;
            {var subQ0=sQuery(id+"F20.wireOp",EDGE,"E903.MirrorCS");var subQ1=sQuery(id+"F20.wireOp",EDGE,"E896.MirrorCS");var subQ2=makeQuery(id+"F20.imprint","INTERSECT",VERTEX,{"derivedFrom":[subQ1,subQ0]});Q21=makeQuery(id+"F20.imprint","IMPRINT",FACE,{"disambiguationData":[TD([[makeQuery(id+"F20.imprint","IMPRINT",EDGE,{"disambiguationData":[TD([[subQ2,-1.0]])],"derivedFrom":subQ1}),1.0]])]});}
            var Q22;
            {var subQ0=sQuery(id+"F20.wireOp",EDGE,"E924.MirrorCS");var subQ1=sQuery(id+"F20.wireOp",EDGE,"E901.MirrorCS");var subQ2=makeQuery(id+"F20.imprint","INTERSECT",VERTEX,{"derivedFrom":[subQ1,subQ0]});Q22=makeQuery(id+"F20.imprint","IMPRINT",FACE,{"disambiguationData":[TD([[makeQuery(id+"F20.imprint","IMPRINT",EDGE,{"disambiguationData":[TD([[subQ2,-1.0]])],"derivedFrom":subQ1}),1.0]])]});}
            var Q23;
            {var subQ0=sQuery(id+"F20.wireOp",EDGE,"E922.MirrorCS");var subQ1=sQuery(id+"F20.wireOp",EDGE,"E914.MirrorCS");var subQ2=makeQuery(id+"F20.imprint","INTERSECT",VERTEX,{"derivedFrom":[subQ1,subQ0]});Q23=makeQuery(id+"F20.imprint","IMPRINT",FACE,{"disambiguationData":[TD([[makeQuery(id+"F20.imprint","IMPRINT",EDGE,{"disambiguationData":[TD([[subQ2,-1.0]])],"derivedFrom":subQ1}),1.0]])]});}
            var Q24;
            {var subQ0=sQuery(id+"F20.wireOp",EDGE,"E909.MirrorCS");var subQ1=sQuery(id+"F20.wireOp",EDGE,"E906.MirrorCS");var subQ2=makeQuery(id+"F20.imprint","INTERSECT",VERTEX,{"derivedFrom":[subQ1,subQ0]});Q24=makeQuery(id+"F20.imprint","IMPRINT",FACE,{"disambiguationData":[TD([[makeQuery(id+"F20.imprint","IMPRINT",EDGE,{"disambiguationData":[TD([[subQ2,-1.0]])],"derivedFrom":subQ1}),-1.0]])]});}
            var Q25;
            {var subQ0=sQuery(id+"F20.wireOp",EDGE,"E925.MirrorCS");var subQ1=sQuery(id+"F20.wireOp",EDGE,"E900.MirrorCS");var subQ2=makeQuery(id+"F20.imprint","INTERSECT",VERTEX,{"derivedFrom":[subQ1,subQ0]});Q25=makeQuery(id+"F20.imprint","IMPRINT",FACE,{"disambiguationData":[TD([[makeQuery(id+"F20.imprint","IMPRINT",EDGE,{"disambiguationData":[TD([[subQ2,-1.0]])],"derivedFrom":subQ1}),-1.0]])]});}
            var Q26;
            {var subQ0=sQuery(id+"F20.wireOp",EDGE,"E910.MirrorCS");var subQ1=sQuery(id+"F20.wireOp",EDGE,"E895.MirrorCS");var subQ2=makeQuery(id+"F20.imprint","INTERSECT",VERTEX,{"derivedFrom":[subQ1,subQ0]});Q26=makeQuery(id+"F20.imprint","IMPRINT",FACE,{"disambiguationData":[TD([[makeQuery(id+"F20.imprint","IMPRINT",EDGE,{"disambiguationData":[TD([[subQ2,-1.0]])],"derivedFrom":subQ1}),-1.0]])]});}
            var Q27;
            {var subQ0=sQuery(id+"F20.wireOp",EDGE,"E913.MirrorCS");var subQ1=sQuery(id+"F20.wireOp",EDGE,"E911.MirrorCS");var subQ2=makeQuery(id+"F20.imprint","INTERSECT",VERTEX,{"derivedFrom":[subQ1,subQ0]});Q27=makeQuery(id+"F20.imprint","IMPRINT",FACE,{"disambiguationData":[TD([[makeQuery(id+"F20.imprint","IMPRINT",EDGE,{"disambiguationData":[TD([[subQ2,-1.0]])],"derivedFrom":subQ1}),-1.0]])]});}
            var Q28;
            {var subQ0=sQuery(id+"F20.wireOp",EDGE,"E1001.MirrorCS");var subQ1=sQuery(id+"F20.wireOp",EDGE,"E1007.MirrorCS");var subQ2=makeQuery(id+"F20.imprint","INTERSECT",VERTEX,{"derivedFrom":[subQ1,subQ0]});Q28=makeQuery(id+"F20.imprint","IMPRINT",FACE,{"disambiguationData":[TD([[makeQuery(id+"F20.imprint","IMPRINT",EDGE,{"disambiguationData":[TD([[subQ2,-1.0]])],"derivedFrom":subQ1}),1.0]])]});}
            var Q29;
            {var subQ0=sQuery(id+"F20.wireOp",EDGE,"E998.MirrorCS");var subQ1=sQuery(id+"F20.wireOp",EDGE,"E1005.MirrorCS");var subQ2=makeQuery(id+"F20.imprint","INTERSECT",VERTEX,{"derivedFrom":[subQ1,subQ0]});Q29=makeQuery(id+"F20.imprint","IMPRINT",FACE,{"disambiguationData":[TD([[makeQuery(id+"F20.imprint","IMPRINT",EDGE,{"disambiguationData":[TD([[subQ2,-1.0]])],"derivedFrom":subQ1}),-1.0]])]});}
            var Q30;
            {var subQ0=sQuery(id+"F20.wireOp",EDGE,"E1020.MirrorCS");var subQ1=sQuery(id+"F20.wireOp",EDGE,"E1002.MirrorCS");var subQ2=makeQuery(id+"F20.imprint","INTERSECT",VERTEX,{"derivedFrom":[subQ1,subQ0]});Q30=makeQuery(id+"F20.imprint","IMPRINT",FACE,{"disambiguationData":[TD([[makeQuery(id+"F20.imprint","IMPRINT",EDGE,{"disambiguationData":[TD([[subQ2,-1.0]])],"derivedFrom":subQ1}),1.0]])]});}
            var Q31;
            {var subQ0=sQuery(id+"F20.wireOp",EDGE,"E1022.MirrorCS");var subQ1=sQuery(id+"F20.wireOp",EDGE,"E1020.MirrorCS");var subQ2=makeQuery(id+"F20.imprint","INTERSECT",VERTEX,{"derivedFrom":[subQ1,subQ0]});Q31=makeQuery(id+"F20.imprint","IMPRINT",FACE,{"disambiguationData":[TD([[makeQuery(id+"F20.imprint","IMPRINT",EDGE,{"disambiguationData":[TD([[subQ2,-1.0]])],"derivedFrom":subQ1}),-1.0]])]});}
            var Q32;
            {var subQ0=sQuery(id+"F20.wireOp",EDGE,"E1010.MirrorCS");var subQ1=sQuery(id+"F20.wireOp",EDGE,"E1009.MirrorCS");var subQ2=makeQuery(id+"F20.imprint","INTERSECT",VERTEX,{"derivedFrom":[subQ1,subQ0]});Q32=makeQuery(id+"F20.imprint","IMPRINT",FACE,{"disambiguationData":[TD([[makeQuery(id+"F20.imprint","IMPRINT",EDGE,{"disambiguationData":[TD([[subQ2,-1.0]])],"derivedFrom":subQ1}),-1.0]])]});}
            var Q33;
            {var subQ0=sQuery(id+"F20.wireOp",EDGE,"E1000.MirrorCS");var subQ1=sQuery(id+"F20.wireOp",EDGE,"E1012.MirrorCS");var subQ2=makeQuery(id+"F20.imprint","INTERSECT",VERTEX,{"derivedFrom":[subQ1,subQ0]});Q33=makeQuery(id+"F20.imprint","IMPRINT",FACE,{"disambiguationData":[TD([[makeQuery(id+"F20.imprint","IMPRINT",EDGE,{"disambiguationData":[TD([[subQ2,-1.0]])],"derivedFrom":subQ1}),1.0]])]});}
            var Q34;
            {var subQ0=sQuery(id+"F20.wireOp",EDGE,"E1021.MirrorCS");var subQ1=sQuery(id+"F20.wireOp",EDGE,"E1006.MirrorCS");var subQ2=makeQuery(id+"F20.imprint","INTERSECT",VERTEX,{"derivedFrom":[subQ1,subQ0]});Q34=makeQuery(id+"F20.imprint","IMPRINT",FACE,{"disambiguationData":[TD([[makeQuery(id+"F20.imprint","IMPRINT",EDGE,{"disambiguationData":[TD([[subQ2,-1.0]])],"derivedFrom":subQ1}),-1.0]])]});}
            var Q35;
            {var subQ0=sQuery(id+"F20.wireOp",EDGE,"E1001.MirrorCS");var subQ1=sQuery(id+"F20.wireOp",EDGE,"E1003.MirrorCS");var subQ2=makeQuery(id+"F20.imprint","INTERSECT",VERTEX,{"derivedFrom":[subQ1,subQ0]});Q35=makeQuery(id+"F20.imprint","IMPRINT",FACE,{"disambiguationData":[TD([[makeQuery(id+"F20.imprint","IMPRINT",EDGE,{"disambiguationData":[TD([[subQ2,-1.0]])],"derivedFrom":subQ1}),-1.0]])]});}
            var Q36;
            {var subQ0=sQuery(id+"F20.wireOp",EDGE,"E963.MirrorCS");var subQ1=sQuery(id+"F20.wireOp",EDGE,"E972.MirrorCS");var subQ2=makeQuery(id+"F20.imprint","INTERSECT",VERTEX,{"derivedFrom":[subQ1,subQ0]});Q36=makeQuery(id+"F20.imprint","IMPRINT",FACE,{"disambiguationData":[TD([[makeQuery(id+"F20.imprint","IMPRINT",EDGE,{"disambiguationData":[TD([[subQ2,-1.0]])],"derivedFrom":subQ1}),1.0]])]});}
            var Q37;
            {var subQ0=sQuery(id+"F20.wireOp",EDGE,"E995.MirrorCS");var subQ1=sQuery(id+"F20.wireOp",EDGE,"E973.MirrorCS");var subQ2=makeQuery(id+"F20.imprint","INTERSECT",VERTEX,{"derivedFrom":[subQ1,subQ0]});Q37=makeQuery(id+"F20.imprint","IMPRINT",FACE,{"disambiguationData":[TD([[makeQuery(id+"F20.imprint","IMPRINT",EDGE,{"disambiguationData":[TD([[subQ2,-1.0]])],"derivedFrom":subQ1}),-1.0]])]});}
            var Q38;
            {var subQ0=sQuery(id+"F20.wireOp",EDGE,"E996.MirrorCS");var subQ1=sQuery(id+"F20.wireOp",EDGE,"E971.MirrorCS");var subQ2=makeQuery(id+"F20.imprint","INTERSECT",VERTEX,{"derivedFrom":[subQ1,subQ0]});Q38=makeQuery(id+"F20.imprint","IMPRINT",FACE,{"disambiguationData":[TD([[makeQuery(id+"F20.imprint","IMPRINT",EDGE,{"disambiguationData":[TD([[subQ2,-1.0]])],"derivedFrom":subQ1}),-1.0]])]});}
            var Q39;
            {var subQ0=sQuery(id+"F20.wireOp",EDGE,"E984.MirrorCS");var subQ1=sQuery(id+"F20.wireOp",EDGE,"E980.MirrorCS");var subQ2=makeQuery(id+"F20.imprint","INTERSECT",VERTEX,{"derivedFrom":[subQ1,subQ0]});Q39=makeQuery(id+"F20.imprint","IMPRINT",FACE,{"disambiguationData":[TD([[makeQuery(id+"F20.imprint","IMPRINT",EDGE,{"disambiguationData":[TD([[subQ2,-1.0]])],"derivedFrom":subQ1}),1.0]])]});}
            var Q40;
            {var subQ0=sQuery(id+"F20.wireOp",EDGE,"E994.MirrorCS");var subQ1=sQuery(id+"F20.wireOp",EDGE,"E991.MirrorCS");var subQ2=makeQuery(id+"F20.imprint","INTERSECT",VERTEX,{"derivedFrom":[subQ1,subQ0]});Q40=makeQuery(id+"F20.imprint","IMPRINT",FACE,{"disambiguationData":[TD([[makeQuery(id+"F20.imprint","IMPRINT",EDGE,{"disambiguationData":[TD([[subQ2,-1.0]])],"derivedFrom":subQ1}),1.0]])]});}
            var Q41;
            {var subQ0=sQuery(id+"F20.wireOp",EDGE,"E986.MirrorCS");var subQ1=sQuery(id+"F20.wireOp",EDGE,"E978.MirrorCS");var subQ2=makeQuery(id+"F20.imprint","INTERSECT",VERTEX,{"derivedFrom":[subQ1,subQ0]});Q41=makeQuery(id+"F20.imprint","IMPRINT",FACE,{"disambiguationData":[TD([[makeQuery(id+"F20.imprint","IMPRINT",EDGE,{"disambiguationData":[TD([[subQ2,-1.0]])],"derivedFrom":subQ1}),-1.0]])]});}
            var Q42;
            {var subQ0=sQuery(id+"F20.wireOp",EDGE,"E988.MirrorCS");var subQ1=sQuery(id+"F20.wireOp",EDGE,"E983.MirrorCS");var subQ2=makeQuery(id+"F20.imprint","INTERSECT",VERTEX,{"derivedFrom":[subQ1,subQ0]});Q42=makeQuery(id+"F20.imprint","IMPRINT",FACE,{"disambiguationData":[TD([[makeQuery(id+"F20.imprint","IMPRINT",EDGE,{"disambiguationData":[TD([[subQ2,-1.0]])],"derivedFrom":subQ1}),1.0]])]});}
            var Q43;
            {var subQ0=sQuery(id+"F20.wireOp",EDGE,"E983.MirrorCS");var subQ1=sQuery(id+"F20.wireOp",EDGE,"E982.MirrorCS");var subQ2=makeQuery(id+"F20.imprint","INTERSECT",VERTEX,{"derivedFrom":[subQ1,subQ0]});Q43=makeQuery(id+"F20.imprint","IMPRINT",FACE,{"disambiguationData":[TD([[makeQuery(id+"F20.imprint","IMPRINT",EDGE,{"disambiguationData":[TD([[subQ2,-1.0]])],"derivedFrom":subQ1}),-1.0]])]});}
            var Q44;
            {var subQ0=sQuery(id+"F20.wireOp",EDGE,"E960.MirrorCS");var subQ1=sQuery(id+"F20.wireOp",EDGE,"E946.MirrorCS");var subQ2=makeQuery(id+"F20.imprint","INTERSECT",VERTEX,{"derivedFrom":[subQ1,subQ0]});Q44=makeQuery(id+"F20.imprint","IMPRINT",FACE,{"disambiguationData":[TD([[makeQuery(id+"F20.imprint","IMPRINT",EDGE,{"disambiguationData":[TD([[subQ2,-1.0]])],"derivedFrom":subQ1}),1.0]])]});}
            var Q45;
            {var subQ0=sQuery(id+"F20.wireOp",EDGE,"E949.MirrorCS");var subQ1=sQuery(id+"F20.wireOp",EDGE,"E929.MirrorCS");var subQ2=makeQuery(id+"F20.imprint","INTERSECT",VERTEX,{"derivedFrom":[subQ1,subQ0]});Q45=makeQuery(id+"F20.imprint","IMPRINT",FACE,{"disambiguationData":[TD([[makeQuery(id+"F20.imprint","IMPRINT",EDGE,{"disambiguationData":[TD([[subQ2,-1.0]])],"derivedFrom":subQ1}),1.0]])]});}
            var Q46;
            {var subQ0=sQuery(id+"F20.wireOp",EDGE,"E945.MirrorCS");var subQ1=sQuery(id+"F20.wireOp",EDGE,"E938.MirrorCS");var subQ2=makeQuery(id+"F20.imprint","INTERSECT",VERTEX,{"derivedFrom":[subQ1,subQ0]});Q46=makeQuery(id+"F20.imprint","IMPRINT",FACE,{"disambiguationData":[TD([[makeQuery(id+"F20.imprint","IMPRINT",EDGE,{"disambiguationData":[TD([[subQ2,-1.0]])],"derivedFrom":subQ1}),-1.0]])]});}
            var Q47;
            {var subQ0=sQuery(id+"F20.wireOp",EDGE,"E939.MirrorCS");var subQ1=sQuery(id+"F20.wireOp",EDGE,"E938.MirrorCS");var subQ2=makeQuery(id+"F20.imprint","INTERSECT",VERTEX,{"derivedFrom":[subQ1,subQ0]});Q47=makeQuery(id+"F20.imprint","IMPRINT",FACE,{"disambiguationData":[TD([[makeQuery(id+"F20.imprint","IMPRINT",EDGE,{"disambiguationData":[TD([[subQ2,-1.0]])],"derivedFrom":subQ1}),-1.0]])]});}
            var Q48;
            {var subQ0=sQuery(id+"F20.wireOp",EDGE,"E962.MirrorCS");var subQ1=sQuery(id+"F20.wireOp",EDGE,"E941.MirrorCS");var subQ2=makeQuery(id+"F20.imprint","INTERSECT",VERTEX,{"derivedFrom":[subQ1,subQ0]});Q48=makeQuery(id+"F20.imprint","IMPRINT",FACE,{"disambiguationData":[TD([[makeQuery(id+"F20.imprint","IMPRINT",EDGE,{"disambiguationData":[TD([[subQ2,-1.0]])],"derivedFrom":subQ1}),-1.0]])]});}
            var Q49;
            {var subQ0=sQuery(id+"F20.wireOp",EDGE,"E953.MirrorCS");var subQ1=sQuery(id+"F20.wireOp",EDGE,"E937.MirrorCS");var subQ2=makeQuery(id+"F20.imprint","INTERSECT",VERTEX,{"derivedFrom":[subQ1,subQ0]});Q49=makeQuery(id+"F20.imprint","IMPRINT",FACE,{"disambiguationData":[TD([[makeQuery(id+"F20.imprint","IMPRINT",EDGE,{"disambiguationData":[TD([[subQ2,-1.0]])],"derivedFrom":subQ1}),-1.0]])]});}
            var Q50;
            {var subQ0=sQuery(id+"F20.wireOp",EDGE,"E947.MirrorCS");var subQ1=sQuery(id+"F20.wireOp",EDGE,"E937.MirrorCS");var subQ2=makeQuery(id+"F20.imprint","INTERSECT",VERTEX,{"derivedFrom":[subQ1,subQ0]});Q50=makeQuery(id+"F20.imprint","IMPRINT",FACE,{"disambiguationData":[TD([[makeQuery(id+"F20.imprint","IMPRINT",EDGE,{"disambiguationData":[TD([[subQ2,-1.0]])],"derivedFrom":subQ1}),-1.0]])]});}
            var Q51;
            {var subQ0=sQuery(id+"F20.wireOp",EDGE,"E946.MirrorCS");var subQ1=sQuery(id+"F20.wireOp",EDGE,"E944.MirrorCS");var subQ2=makeQuery(id+"F20.imprint","INTERSECT",VERTEX,{"derivedFrom":[subQ1,subQ0]});Q51=makeQuery(id+"F20.imprint","IMPRINT",FACE,{"disambiguationData":[TD([[makeQuery(id+"F20.imprint","IMPRINT",EDGE,{"disambiguationData":[TD([[subQ2,-1.0]])],"derivedFrom":subQ1}),-1.0]])]});}
            var Q52;
            {var subQ0=sQuery(id+"F20.wireOp",EDGE,"E1084.MirrorCS");var subQ1=sQuery(id+"F20.wireOp",EDGE,"E1083.MirrorCS");var subQ2=makeQuery(id+"F20.imprint","INTERSECT",VERTEX,{"derivedFrom":[subQ1,subQ0]});Q52=makeQuery(id+"F20.imprint","IMPRINT",FACE,{"disambiguationData":[TD([[makeQuery(id+"F20.imprint","IMPRINT",EDGE,{"disambiguationData":[TD([[subQ2,-1.0]])],"derivedFrom":subQ1}),-1.0]])]});}
            var Q53;
            {var subQ0=sQuery(id+"F20.wireOp",EDGE,"E849");var subQ1=sQuery(id+"F20.wireOp",EDGE,"E824");var subQ2=makeQuery(id+"F20.imprint","INTERSECT",VERTEX,{"derivedFrom":[subQ1,subQ0]});Q53=makeQuery(id+"F20.imprint","IMPRINT",FACE,{"disambiguationData":[TD([[makeQuery(id+"F20.imprint","IMPRINT",EDGE,{"disambiguationData":[TD([[subQ2,-1.0]])],"derivedFrom":subQ1}),-1.0]])]});}
            var Q54;
            {var subQ0=sQuery(id+"F20.wireOp",EDGE,"E822");var subQ1=sQuery(id+"F20.wireOp",EDGE,"E820");var subQ2=makeQuery(id+"F20.imprint","INTERSECT",VERTEX,{"derivedFrom":[subQ1,subQ0]});Q54=makeQuery(id+"F20.imprint","IMPRINT",FACE,{"disambiguationData":[TD([[makeQuery(id+"F20.imprint","IMPRINT",EDGE,{"disambiguationData":[TD([[subQ2,-1.0]])],"derivedFrom":subQ1}),1.0]])]});}
            var Q55;
            {var subQ0=sQuery(id+"F20.wireOp",EDGE,"E844.MirrorCS");var subQ1=sQuery(id+"F20.wireOp",EDGE,"E824");var subQ2=makeQuery(id+"F20.imprint","INTERSECT",VERTEX,{"derivedFrom":[subQ1,subQ0]});Q55=makeQuery(id+"F20.imprint","IMPRINT",FACE,{"disambiguationData":[TD([[makeQuery(id+"F20.imprint","IMPRINT",EDGE,{"disambiguationData":[TD([[subQ2,-1.0]])],"derivedFrom":subQ1}),-1.0]])]});}
            var Q56;
            {var subQ0=sQuery(id+"F20.wireOp",EDGE,"E849");var subQ1=sQuery(id+"F20.wireOp",EDGE,"E824");var subQ2=makeQuery(id+"F20.imprint","INTERSECT",VERTEX,{"derivedFrom":[subQ1,subQ0]});Q56=makeQuery(id+"F20.imprint","IMPRINT",FACE,{"disambiguationData":[TD([[makeQuery(id+"F20.imprint","IMPRINT",EDGE,{"disambiguationData":[TD([[subQ2,-1.0]])],"derivedFrom":subQ1}),-1.0]])]});}
            var Q57;
            {var subQ0=sQuery(id+"F20.wireOp",EDGE,"E1107.MirrorCS");var subQ1=sQuery(id+"F20.wireOp",EDGE,"E1078.MirrorCS");var subQ2=makeQuery(id+"F20.imprint","INTERSECT",VERTEX,{"derivedFrom":[subQ1,subQ0]});Q57=makeQuery(id+"F20.imprint","IMPRINT",FACE,{"disambiguationData":[TD([[makeQuery(id+"F20.imprint","IMPRINT",EDGE,{"disambiguationData":[TD([[subQ2,-1.0]])],"derivedFrom":subQ1}),-1.0]])]});}
            var Q58;
            {var subQ0=sQuery(id+"F20.wireOp",EDGE,"E844.MirrorCS");var subQ1=sQuery(id+"F20.wireOp",EDGE,"E824");var subQ2=makeQuery(id+"F20.imprint","INTERSECT",VERTEX,{"derivedFrom":[subQ1,subQ0]});Q58=makeQuery(id+"F20.imprint","IMPRINT",FACE,{"disambiguationData":[TD([[makeQuery(id+"F20.imprint","IMPRINT",EDGE,{"disambiguationData":[TD([[subQ2,-1.0]])],"derivedFrom":subQ1}),-1.0]])]});}
            var Q59;
            {var subQ0=sQuery(id+"F20.wireOp",EDGE,"E827.MirrorCS");var subQ1=sQuery(id+"F20.wireOp",EDGE,"E826");var subQ2=makeQuery(id+"F20.imprint","INTERSECT",VERTEX,{"derivedFrom":[subQ1,subQ0]});Q59=makeQuery(id+"F20.imprint","IMPRINT",FACE,{"disambiguationData":[TD([[makeQuery(id+"F20.imprint","IMPRINT",EDGE,{"disambiguationData":[TD([[subQ2,-1.0]])],"derivedFrom":subQ1}),1.0]])]});}
            var Q60;
            {var subQ0=sQuery(id+"F20.wireOp",EDGE,"E834.MirrorCS");var subQ1=sQuery(id+"F20.wireOp",EDGE,"E826");var subQ2=makeQuery(id+"F20.imprint","INTERSECT",VERTEX,{"derivedFrom":[subQ1,subQ0]});Q60=makeQuery(id+"F20.imprint","IMPRINT",FACE,{"disambiguationData":[TD([[makeQuery(id+"F20.imprint","IMPRINT",EDGE,{"disambiguationData":[TD([[subQ2,-1.0]])],"derivedFrom":subQ1}),1.0]])]});}
            var Q61;
            {var subQ0=sQuery(id+"F20.wireOp",EDGE,"E838.MirrorCS");var subQ1=sQuery(id+"F20.wireOp",EDGE,"E836");var subQ2=makeQuery(id+"F20.imprint","INTERSECT",VERTEX,{"derivedFrom":[subQ1,subQ0]});Q61=makeQuery(id+"F20.imprint","IMPRINT",FACE,{"disambiguationData":[TD([[makeQuery(id+"F20.imprint","IMPRINT",EDGE,{"disambiguationData":[TD([[subQ2,-1.0]])],"derivedFrom":subQ1}),-1.0]])]});}
            var Q62;
            {var subQ0=sQuery(id+"F20.wireOp",EDGE,"E842.MirrorCS");var subQ1=sQuery(id+"F20.wireOp",EDGE,"E836");var subQ2=makeQuery(id+"F20.imprint","INTERSECT",VERTEX,{"derivedFrom":[subQ1,subQ0]});Q62=makeQuery(id+"F20.imprint","IMPRINT",FACE,{"disambiguationData":[TD([[makeQuery(id+"F20.imprint","IMPRINT",EDGE,{"disambiguationData":[TD([[subQ2,-1.0]])],"derivedFrom":subQ1}),-1.0]])]});}
            var Q63;
            {var subQ0=sQuery(id+"F20.wireOp",EDGE,"E852");var subQ1=sQuery(id+"F20.wireOp",EDGE,"E850");var subQ2=makeQuery(id+"F20.imprint","INTERSECT",VERTEX,{"derivedFrom":[subQ1,subQ0]});Q63=makeQuery(id+"F20.imprint","IMPRINT",FACE,{"disambiguationData":[TD([[makeQuery(id+"F20.imprint","IMPRINT",EDGE,{"disambiguationData":[TD([[subQ2,-1.0]])],"derivedFrom":subQ1}),-1.0]])]});}
            var Q64;
            {var subQ0=sQuery(id+"F20.wireOp",EDGE,"E1094.MirrorCS");var subQ1=sQuery(id+"F20.wireOp",EDGE,"E1076.MirrorCS");var subQ2=makeQuery(id+"F20.imprint","INTERSECT",VERTEX,{"derivedFrom":[subQ1,subQ0]});Q64=makeQuery(id+"F20.imprint","IMPRINT",FACE,{"disambiguationData":[TD([[makeQuery(id+"F20.imprint","IMPRINT",EDGE,{"disambiguationData":[TD([[subQ2,-1.0]])],"derivedFrom":subQ1}),1.0]])]});}
            var Q65;
            {var subQ0=sQuery(id+"F20.wireOp",EDGE,"E1387.MirrorCS");var subQ1=sQuery(id+"F20.wireOp",EDGE,"E1268.MirrorCS");var subQ2=makeQuery(id+"F20.imprint","INTERSECT",VERTEX,{"derivedFrom":[subQ1,subQ0]});Q65=makeQuery(id+"F20.imprint","IMPRINT",FACE,{"disambiguationData":[TD([[makeQuery(id+"F20.imprint","IMPRINT",EDGE,{"disambiguationData":[TD([[subQ2,-1.0]])],"derivedFrom":subQ1}),-1.0]])]});}
            var Q66;
            {var subQ0=sQuery(id+"F20.wireOp",EDGE,"E1344.MirrorCS");var subQ1=sQuery(id+"F20.wireOp",EDGE,"E1318.MirrorCS");var subQ2=makeQuery(id+"F20.imprint","INTERSECT",VERTEX,{"derivedFrom":[subQ1,subQ0]});Q66=makeQuery(id+"F20.imprint","IMPRINT",FACE,{"disambiguationData":[TD([[makeQuery(id+"F20.imprint","IMPRINT",EDGE,{"disambiguationData":[TD([[subQ2,-1.0]])],"derivedFrom":subQ1}),-1.0]])]});}
            var Q67;
            {var subQ0=sQuery(id+"F20.wireOp",EDGE,"E1312.MirrorCS");var subQ1=sQuery(id+"F20.wireOp",EDGE,"E1264.MirrorCS");var subQ2=makeQuery(id+"F20.imprint","INTERSECT",VERTEX,{"derivedFrom":[subQ1,subQ0]});Q67=makeQuery(id+"F20.imprint","IMPRINT",FACE,{"disambiguationData":[TD([[makeQuery(id+"F20.imprint","IMPRINT",EDGE,{"disambiguationData":[TD([[subQ2,-1.0]])],"derivedFrom":subQ1}),1.0]])]});}
            var Q68;
            {var subQ0=sQuery(id+"F20.wireOp",EDGE,"E1292.MirrorCS");var subQ1=sQuery(id+"F20.wireOp",EDGE,"E1221.MirrorCS");var subQ2=makeQuery(id+"F20.imprint","INTERSECT",VERTEX,{"derivedFrom":[subQ1,subQ0]});Q68=makeQuery(id+"F20.imprint","IMPRINT",FACE,{"disambiguationData":[TD([[makeQuery(id+"F20.imprint","IMPRINT",EDGE,{"disambiguationData":[TD([[subQ2,-1.0]])],"derivedFrom":subQ1}),-1.0]])]});}
            var Q69;
            {var subQ0=sQuery(id+"F20.wireOp",EDGE,"E1300.MirrorCS");var subQ1=sQuery(id+"F20.wireOp",EDGE,"E1233.MirrorCS");var subQ2=makeQuery(id+"F20.imprint","INTERSECT",VERTEX,{"derivedFrom":[subQ1,subQ0]});Q69=makeQuery(id+"F20.imprint","IMPRINT",FACE,{"disambiguationData":[TD([[makeQuery(id+"F20.imprint","IMPRINT",EDGE,{"disambiguationData":[TD([[subQ2,-1.0]])],"derivedFrom":subQ1}),1.0]])]});}
            var Q70;
            {var subQ0=sQuery(id+"F20.wireOp",EDGE,"E1387.MirrorCS");var subQ1=sQuery(id+"F20.wireOp",EDGE,"E1220.MirrorCS");var subQ2=makeQuery(id+"F20.imprint","INTERSECT",VERTEX,{"derivedFrom":[subQ1,subQ0]});Q70=makeQuery(id+"F20.imprint","IMPRINT",FACE,{"disambiguationData":[TD([[makeQuery(id+"F20.imprint","IMPRINT",EDGE,{"disambiguationData":[TD([[subQ2,-1.0]])],"derivedFrom":subQ1}),1.0]])]});}
            var Q71;
            {var subQ0=sQuery(id+"F20.wireOp",EDGE,"E1337.MirrorCS");var subQ1=sQuery(id+"F20.wireOp",EDGE,"E1211.MirrorCS");var subQ2=makeQuery(id+"F20.imprint","INTERSECT",VERTEX,{"derivedFrom":[subQ1,subQ0]});Q71=makeQuery(id+"F20.imprint","IMPRINT",FACE,{"disambiguationData":[TD([[makeQuery(id+"F20.imprint","IMPRINT",EDGE,{"disambiguationData":[TD([[subQ2,-1.0]])],"derivedFrom":subQ1}),1.0]])]});}
            var Q72;
            {var subQ0=sQuery(id+"F20.wireOp",EDGE,"E1344.MirrorCS");var subQ1=sQuery(id+"F20.wireOp",EDGE,"E1282.MirrorCS");var subQ2=makeQuery(id+"F20.imprint","INTERSECT",VERTEX,{"derivedFrom":[subQ1,subQ0]});Q72=makeQuery(id+"F20.imprint","IMPRINT",FACE,{"disambiguationData":[TD([[makeQuery(id+"F20.imprint","IMPRINT",EDGE,{"disambiguationData":[TD([[subQ2,-1.0]])],"derivedFrom":subQ1}),1.0]])]});}
            var Q73;
            {var subQ0=sQuery(id+"F20.wireOp",EDGE,"E1279.MirrorCS");var subQ1=sQuery(id+"F20.wireOp",EDGE,"E1234.MirrorCS");var subQ2=makeQuery(id+"F20.imprint","INTERSECT",VERTEX,{"derivedFrom":[subQ1,subQ0]});Q73=makeQuery(id+"F20.imprint","IMPRINT",FACE,{"disambiguationData":[TD([[makeQuery(id+"F20.imprint","IMPRINT",EDGE,{"disambiguationData":[TD([[subQ2,-1.0]])],"derivedFrom":subQ1}),-1.0]])]});}
            var Q74;
            {var subQ0=sQuery(id+"F20.wireOp",EDGE,"E1281.MirrorCS");var subQ1=sQuery(id+"F20.wireOp",EDGE,"E1248.MirrorCS");var subQ2=makeQuery(id+"F20.imprint","INTERSECT",VERTEX,{"derivedFrom":[subQ1,subQ0]});Q74=makeQuery(id+"F20.imprint","IMPRINT",FACE,{"disambiguationData":[TD([[makeQuery(id+"F20.imprint","IMPRINT",EDGE,{"disambiguationData":[TD([[subQ2,-1.0]])],"derivedFrom":subQ1}),1.0]])]});}
            var Q75;
            {var subQ0=sQuery(id+"F20.wireOp",EDGE,"E1226.MirrorCS");var subQ1=sQuery(id+"F20.wireOp",EDGE,"E1215.MirrorCS");var subQ2=makeQuery(id+"F20.imprint","INTERSECT",VERTEX,{"derivedFrom":[subQ1,subQ0]});Q75=makeQuery(id+"F20.imprint","IMPRINT",FACE,{"disambiguationData":[TD([[makeQuery(id+"F20.imprint","IMPRINT",EDGE,{"disambiguationData":[TD([[subQ2,-1.0]])],"derivedFrom":subQ1}),-1.0]])]});}
            var Q76;
            {var subQ0=sQuery(id+"F20.wireOp",EDGE,"E1372.MirrorCS");var subQ1=sQuery(id+"F20.wireOp",EDGE,"E1249.MirrorCS");var subQ2=makeQuery(id+"F20.imprint","INTERSECT",VERTEX,{"derivedFrom":[subQ1,subQ0]});Q76=makeQuery(id+"F20.imprint","IMPRINT",FACE,{"disambiguationData":[TD([[makeQuery(id+"F20.imprint","IMPRINT",EDGE,{"disambiguationData":[TD([[subQ2,-1.0]])],"derivedFrom":subQ1}),1.0]])]});}
            var Q77;
            {var subQ0=sQuery(id+"F20.wireOp",EDGE,"E1372.MirrorCS");var subQ1=sQuery(id+"F20.wireOp",EDGE,"E1322.MirrorCS");var subQ2=makeQuery(id+"F20.imprint","INTERSECT",VERTEX,{"derivedFrom":[subQ1,subQ0]});Q77=makeQuery(id+"F20.imprint","IMPRINT",FACE,{"disambiguationData":[TD([[makeQuery(id+"F20.imprint","IMPRINT",EDGE,{"disambiguationData":[TD([[subQ2,-1.0]])],"derivedFrom":subQ1}),-1.0]])]});}
            var Q78;
            {var subQ0=sQuery(id+"F20.wireOp",EDGE,"E1324.MirrorCS");var subQ1=sQuery(id+"F20.wireOp",EDGE,"E1278.MirrorCS");var subQ2=makeQuery(id+"F20.imprint","INTERSECT",VERTEX,{"derivedFrom":[subQ1,subQ0]});Q78=makeQuery(id+"F20.imprint","IMPRINT",FACE,{"disambiguationData":[TD([[makeQuery(id+"F20.imprint","IMPRINT",EDGE,{"disambiguationData":[TD([[subQ2,-1.0]])],"derivedFrom":subQ1}),-1.0]])]});}
            var Q79;
            {var subQ0=sQuery(id+"F20.wireOp",EDGE,"E1410.MirrorCS");var subQ1=sQuery(id+"F20.wireOp",EDGE,"E1352.MirrorCS");var subQ2=makeQuery(id+"F20.imprint","INTERSECT",VERTEX,{"derivedFrom":[subQ1,subQ0]});Q79=makeQuery(id+"F20.imprint","IMPRINT",FACE,{"disambiguationData":[TD([[makeQuery(id+"F20.imprint","IMPRINT",EDGE,{"disambiguationData":[TD([[subQ2,-1.0]])],"derivedFrom":subQ1}),1.0]])]});}
            var Q80;
            {var subQ0=sQuery(id+"F20.wireOp",EDGE,"E1391.MirrorCS");var subQ1=sQuery(id+"F20.wireOp",EDGE,"E1320.MirrorCS");var subQ2=makeQuery(id+"F20.imprint","INTERSECT",VERTEX,{"derivedFrom":[subQ1,subQ0]});Q80=makeQuery(id+"F20.imprint","IMPRINT",FACE,{"disambiguationData":[TD([[makeQuery(id+"F20.imprint","IMPRINT",EDGE,{"disambiguationData":[TD([[subQ2,-1.0]])],"derivedFrom":subQ1}),1.0]])]});}
            var Q81;
            {var subQ0=sQuery(id+"F20.wireOp",EDGE,"E1329.MirrorCS");var subQ1=sQuery(id+"F20.wireOp",EDGE,"E1238.MirrorCS");var subQ2=makeQuery(id+"F20.imprint","INTERSECT",VERTEX,{"derivedFrom":[subQ1,subQ0]});Q81=makeQuery(id+"F20.imprint","IMPRINT",FACE,{"disambiguationData":[TD([[makeQuery(id+"F20.imprint","IMPRINT",EDGE,{"disambiguationData":[TD([[subQ2,-1.0]])],"derivedFrom":subQ1}),-1.0]])]});}
            var Q82;
            {var subQ0=sQuery(id+"F20.wireOp",EDGE,"E1329.MirrorCS");var subQ1=sQuery(id+"F20.wireOp",EDGE,"E1229.MirrorCS");var subQ2=makeQuery(id+"F20.imprint","INTERSECT",VERTEX,{"derivedFrom":[subQ1,subQ0]});Q82=makeQuery(id+"F20.imprint","IMPRINT",FACE,{"disambiguationData":[TD([[makeQuery(id+"F20.imprint","IMPRINT",EDGE,{"disambiguationData":[TD([[subQ2,-1.0]])],"derivedFrom":subQ1}),1.0]])]});}
            var Q83;
            {var subQ0=sQuery(id+"F20.wireOp",EDGE,"E1216.MirrorCS");var subQ1=sQuery(id+"F20.wireOp",EDGE,"E1209.MirrorCS");var subQ2=makeQuery(id+"F20.imprint","INTERSECT",VERTEX,{"derivedFrom":[subQ1,subQ0]});Q83=makeQuery(id+"F20.imprint","IMPRINT",FACE,{"disambiguationData":[TD([[makeQuery(id+"F20.imprint","IMPRINT",EDGE,{"disambiguationData":[TD([[subQ2,-1.0]])],"derivedFrom":subQ1}),-1.0]])]});}
            var Q84;
            {var subQ0=sQuery(id+"F20.wireOp",EDGE,"E1236.MirrorCS");var subQ1=sQuery(id+"F20.wireOp",EDGE,"E1157.MirrorCS");var subQ2=makeQuery(id+"F20.imprint","INTERSECT",VERTEX,{"derivedFrom":[subQ1,subQ0]});Q84=makeQuery(id+"F20.imprint","IMPRINT",FACE,{"disambiguationData":[TD([[makeQuery(id+"F20.imprint","IMPRINT",EDGE,{"disambiguationData":[TD([[subQ2,-1.0]])],"derivedFrom":subQ1}),1.0]])]});}
            var Q85;
            {var subQ0=sQuery(id+"F20.wireOp",EDGE,"E1231.MirrorCS");var subQ1=sQuery(id+"F20.wireOp",EDGE,"E1175.MirrorCS");var subQ2=makeQuery(id+"F20.imprint","INTERSECT",VERTEX,{"derivedFrom":[subQ1,subQ0]});Q85=makeQuery(id+"F20.imprint","IMPRINT",FACE,{"disambiguationData":[TD([[makeQuery(id+"F20.imprint","IMPRINT",EDGE,{"disambiguationData":[TD([[subQ2,-1.0]])],"derivedFrom":subQ1}),-1.0]])]});}
            var Q86;
            {var subQ0=sQuery(id+"F20.wireOp",EDGE,"E1259.MirrorCS");var subQ1=sQuery(id+"F20.wireOp",EDGE,"E1184.MirrorCS");var subQ2=makeQuery(id+"F20.imprint","INTERSECT",VERTEX,{"derivedFrom":[subQ1,subQ0]});Q86=makeQuery(id+"F20.imprint","IMPRINT",FACE,{"disambiguationData":[TD([[makeQuery(id+"F20.imprint","IMPRINT",EDGE,{"disambiguationData":[TD([[subQ2,-1.0]])],"derivedFrom":subQ1}),1.0]])]});}
            var Q87;
            {var subQ0=sQuery(id+"F20.wireOp",EDGE,"E1230.MirrorCS");var subQ1=sQuery(id+"F20.wireOp",EDGE,"E1222.MirrorCS");var subQ2=makeQuery(id+"F20.imprint","INTERSECT",VERTEX,{"derivedFrom":[subQ1,subQ0]});Q87=makeQuery(id+"F20.imprint","IMPRINT",FACE,{"disambiguationData":[TD([[makeQuery(id+"F20.imprint","IMPRINT",EDGE,{"disambiguationData":[TD([[subQ2,-1.0]])],"derivedFrom":subQ1}),1.0]])]});}
            var Q88;
            {var subQ18=makeQuery(id+"F1.opExtrude","SWEPT_FACE",FACE,{"disambiguationData":[OSD([sQuery(id+"F0.wireOp",EDGE,"E0.top")])]});Q88=makeQuery(id+"F20.imprint","IMPRINT",FACE,{"disambiguationData":[TD([[makeQuery(id+"F20.imprint","IMPRINT",EDGE,{"derivedFrom":makeQuery(id+"F7.boolean.opBoolean","INTERSECT",EDGE,{"derivedFrom":[subQ18,makeQuery(id+"F7.opExtrude","SWEPT_FACE",FACE,{"disambiguationData":[OSD([sQuery(id+"F6.wireOp",EDGE,"E3.top")])]})]})}),-1.0]])]});}
            var Q89;
            {var subQ0=sQuery(id+"F20.wireOp",EDGE,"E1086.MirrorCS");var subQ1=sQuery(id+"F20.wireOp",EDGE,"E1078.MirrorCS");var subQ2=makeQuery(id+"F20.imprint","INTERSECT",VERTEX,{"derivedFrom":[subQ1,subQ0]});Q89=makeQuery(id+"F20.imprint","IMPRINT",FACE,{"disambiguationData":[TD([[makeQuery(id+"F20.imprint","IMPRINT",EDGE,{"disambiguationData":[TD([[subQ2,-1.0]])],"derivedFrom":subQ1}),-1.0]])]});}
            var Q90;
            {var subQ0=sQuery(id+"F20.wireOp",EDGE,"E1323.MirrorCS");var subQ1=sQuery(id+"F20.wireOp",EDGE,"E1207.MirrorCS");var subQ2=makeQuery(id+"F20.imprint","INTERSECT",VERTEX,{"derivedFrom":[subQ1,subQ0]});Q90=makeQuery(id+"F20.imprint","IMPRINT",FACE,{"disambiguationData":[TD([[makeQuery(id+"F20.imprint","IMPRINT",EDGE,{"disambiguationData":[TD([[subQ2,-1.0]])],"derivedFrom":subQ1}),1.0]])]});}
            var Q91;
            {var subQ0=sQuery(id+"F20.wireOp",EDGE,"E1143.MirrorCS");var subQ1=sQuery(id+"F20.wireOp",EDGE,"E1160.MirrorCS");var subQ2=makeQuery(id+"F20.imprint","INTERSECT",VERTEX,{"derivedFrom":[subQ1,subQ0]});Q91=makeQuery(id+"F20.imprint","IMPRINT",FACE,{"disambiguationData":[TD([[makeQuery(id+"F20.imprint","IMPRINT",EDGE,{"disambiguationData":[TD([[subQ2,-1.0]])],"derivedFrom":subQ1}),1.0]])]});}
            var Q92;
            {var subQ0=sQuery(id+"F20.wireOp",EDGE,"E1396.MirrorCS");var subQ1=sQuery(id+"F20.wireOp",EDGE,"E1210.MirrorCS");var subQ2=makeQuery(id+"F20.imprint","INTERSECT",VERTEX,{"derivedFrom":[subQ1,subQ0]});Q92=makeQuery(id+"F20.imprint","IMPRINT",FACE,{"disambiguationData":[TD([[makeQuery(id+"F20.imprint","IMPRINT",EDGE,{"disambiguationData":[TD([[subQ2,-1.0]])],"derivedFrom":subQ1}),-1.0]])]});}
            var Q93;
            {var subQ0=sQuery(id+"F20.wireOp",EDGE,"E1247.MirrorCS");var subQ1=sQuery(id+"F20.wireOp",EDGE,"E1210.MirrorCS");var subQ2=makeQuery(id+"F20.imprint","INTERSECT",VERTEX,{"derivedFrom":[subQ1,subQ0]});Q93=makeQuery(id+"F20.imprint","IMPRINT",FACE,{"disambiguationData":[TD([[makeQuery(id+"F20.imprint","IMPRINT",EDGE,{"disambiguationData":[TD([[subQ2,-1.0]])],"derivedFrom":subQ1}),-1.0]])]});}
            var Q94;
            {var subQ0=sQuery(id+"F20.wireOp",EDGE,"E1388.MirrorCS");var subQ1=sQuery(id+"F20.wireOp",EDGE,"E1212.MirrorCS");var subQ2=makeQuery(id+"F20.imprint","INTERSECT",VERTEX,{"derivedFrom":[subQ1,subQ0]});Q94=makeQuery(id+"F20.imprint","IMPRINT",FACE,{"disambiguationData":[TD([[makeQuery(id+"F20.imprint","IMPRINT",EDGE,{"disambiguationData":[TD([[subQ2,-1.0]])],"derivedFrom":subQ1}),1.0]])]});}
            var Q95;
            {var subQ0=sQuery(id+"F20.wireOp",EDGE,"E1362.MirrorCS");var subQ1=sQuery(id+"F20.wireOp",EDGE,"E1181.MirrorCS");var subQ2=makeQuery(id+"F20.imprint","INTERSECT",VERTEX,{"derivedFrom":[subQ1,subQ0]});Q95=makeQuery(id+"F20.imprint","IMPRINT",FACE,{"disambiguationData":[TD([[makeQuery(id+"F20.imprint","IMPRINT",EDGE,{"disambiguationData":[TD([[subQ2,-1.0]])],"derivedFrom":subQ1}),-1.0]])]});}
            var Q96;
            {var subQ0=sQuery(id+"F20.wireOp",EDGE,"E1404.MirrorCS");var subQ1=sQuery(id+"F20.wireOp",EDGE,"E1314.MirrorCS");var subQ2=makeQuery(id+"F20.imprint","INTERSECT",VERTEX,{"derivedFrom":[subQ1,subQ0]});Q96=makeQuery(id+"F20.imprint","IMPRINT",FACE,{"disambiguationData":[TD([[makeQuery(id+"F20.imprint","IMPRINT",EDGE,{"disambiguationData":[TD([[subQ2,-1.0]])],"derivedFrom":subQ1}),-1.0]])]});}
            var Q97;
            {var subQ0=sQuery(id+"F20.wireOp",EDGE,"E1293.MirrorCS");var subQ1=sQuery(id+"F20.wireOp",EDGE,"E1201.MirrorCS");var subQ2=makeQuery(id+"F20.imprint","INTERSECT",VERTEX,{"derivedFrom":[subQ1,subQ0]});Q97=makeQuery(id+"F20.imprint","IMPRINT",FACE,{"disambiguationData":[TD([[makeQuery(id+"F20.imprint","IMPRINT",EDGE,{"disambiguationData":[TD([[subQ2,-1.0]])],"derivedFrom":subQ1}),1.0]])]});}
            var Q98;
            {var subQ0=sQuery(id+"F20.wireOp",EDGE,"E1392.MirrorCS");var subQ1=sQuery(id+"F20.wireOp",EDGE,"E1197.MirrorCS");var subQ2=makeQuery(id+"F20.imprint","INTERSECT",VERTEX,{"derivedFrom":[subQ1,subQ0]});Q98=makeQuery(id+"F20.imprint","IMPRINT",FACE,{"disambiguationData":[TD([[makeQuery(id+"F20.imprint","IMPRINT",EDGE,{"disambiguationData":[TD([[subQ2,-1.0]])],"derivedFrom":subQ1}),-1.0]])]});}
            var Q99;
            {var subQ0=sQuery(id+"F20.wireOp",EDGE,"E1192.MirrorCS");var subQ1=sQuery(id+"F20.wireOp",EDGE,"E1158.MirrorCS");var subQ2=makeQuery(id+"F20.imprint","INTERSECT",VERTEX,{"derivedFrom":[subQ1,subQ0]});Q99=makeQuery(id+"F20.imprint","IMPRINT",FACE,{"disambiguationData":[TD([[makeQuery(id+"F20.imprint","IMPRINT",EDGE,{"disambiguationData":[TD([[subQ2,-1.0]])],"derivedFrom":subQ1}),-1.0]])]});}
            var Q100;
            {var subQ0=sQuery(id+"F20.wireOp",EDGE,"E1192.MirrorCS");var subQ1=sQuery(id+"F20.wireOp",EDGE,"E1128.MirrorCS");var subQ2=makeQuery(id+"F20.imprint","INTERSECT",VERTEX,{"derivedFrom":[subQ1,subQ0]});Q100=makeQuery(id+"F20.imprint","IMPRINT",FACE,{"disambiguationData":[TD([[makeQuery(id+"F20.imprint","IMPRINT",EDGE,{"disambiguationData":[TD([[subQ2,-1.0]])],"derivedFrom":subQ1}),-1.0]])]});}
            var Q101;
            {var subQ0=sQuery(id+"F20.wireOp",EDGE,"E1179.MirrorCS");var subQ1=sQuery(id+"F20.wireOp",EDGE,"E1140.MirrorCS");var subQ2=makeQuery(id+"F20.imprint","INTERSECT",VERTEX,{"derivedFrom":[subQ1,subQ0]});Q101=makeQuery(id+"F20.imprint","IMPRINT",FACE,{"disambiguationData":[TD([[makeQuery(id+"F20.imprint","IMPRINT",EDGE,{"disambiguationData":[TD([[subQ2,-1.0]])],"derivedFrom":subQ1}),-1.0]])]});}
            var Q102;
            {var subQ0=sQuery(id+"F20.wireOp",EDGE,"E1348.MirrorCS");var subQ1=sQuery(id+"F20.wireOp",EDGE,"E1187.MirrorCS");var subQ2=makeQuery(id+"F20.imprint","INTERSECT",VERTEX,{"derivedFrom":[subQ1,subQ0]});Q102=makeQuery(id+"F20.imprint","IMPRINT",FACE,{"disambiguationData":[TD([[makeQuery(id+"F20.imprint","IMPRINT",EDGE,{"disambiguationData":[TD([[subQ2,-1.0]])],"derivedFrom":subQ1}),-1.0]])]});}
            var Q103;
            {var subQ0=sQuery(id+"F20.wireOp",EDGE,"E1306.MirrorCS");var subQ1=sQuery(id+"F20.wireOp",EDGE,"E1187.MirrorCS");var subQ2=makeQuery(id+"F20.imprint","INTERSECT",VERTEX,{"derivedFrom":[subQ1,subQ0]});Q103=makeQuery(id+"F20.imprint","IMPRINT",FACE,{"disambiguationData":[TD([[makeQuery(id+"F20.imprint","IMPRINT",EDGE,{"disambiguationData":[TD([[subQ2,-1.0]])],"derivedFrom":subQ1}),-1.0]])]});}
            var Q104;
            {var subQ0=sQuery(id+"F20.wireOp",EDGE,"E1370.MirrorCS");var subQ1=sQuery(id+"F20.wireOp",EDGE,"E1270.MirrorCS");var subQ2=makeQuery(id+"F20.imprint","INTERSECT",VERTEX,{"derivedFrom":[subQ1,subQ0]});Q104=makeQuery(id+"F20.imprint","IMPRINT",FACE,{"disambiguationData":[TD([[makeQuery(id+"F20.imprint","IMPRINT",EDGE,{"disambiguationData":[TD([[subQ2,-1.0]])],"derivedFrom":subQ1}),1.0]])]});}
            var Q105;
            {var subQ0=sQuery(id+"F20.wireOp",EDGE,"E1142.MirrorCS");var subQ1=sQuery(id+"F20.wireOp",EDGE,"E1125.MirrorCS");var subQ2=makeQuery(id+"F20.imprint","INTERSECT",VERTEX,{"derivedFrom":[subQ1,subQ0]});Q105=makeQuery(id+"F20.imprint","IMPRINT",FACE,{"disambiguationData":[TD([[makeQuery(id+"F20.imprint","IMPRINT",EDGE,{"disambiguationData":[TD([[subQ2,-1.0]])],"derivedFrom":subQ1}),-1.0]])]});}
            var Q106;
            {var subQ0=sQuery(id+"F20.wireOp",EDGE,"E1183.MirrorCS");var subQ1=sQuery(id+"F20.wireOp",EDGE,"E1144.MirrorCS");var subQ2=makeQuery(id+"F20.imprint","INTERSECT",VERTEX,{"derivedFrom":[subQ1,subQ0]});Q106=makeQuery(id+"F20.imprint","IMPRINT",FACE,{"disambiguationData":[TD([[makeQuery(id+"F20.imprint","IMPRINT",EDGE,{"disambiguationData":[TD([[subQ2,-1.0]])],"derivedFrom":subQ1}),-1.0]])]});}
            var Q107;
            {var subQ0=sQuery(id+"F20.wireOp",EDGE,"E1164.MirrorCS");var subQ1=sQuery(id+"F20.wireOp",EDGE,"E1155.MirrorCS");var subQ2=makeQuery(id+"F20.imprint","INTERSECT",VERTEX,{"derivedFrom":[subQ1,subQ0]});Q107=makeQuery(id+"F20.imprint","IMPRINT",FACE,{"disambiguationData":[TD([[makeQuery(id+"F20.imprint","IMPRINT",EDGE,{"disambiguationData":[TD([[subQ2,-1.0]])],"derivedFrom":subQ1}),1.0]])]});}
            var Q108;
            {var subQ0=sQuery(id+"F20.wireOp",EDGE,"E1145.MirrorCS");var subQ1=sQuery(id+"F20.wireOp",EDGE,"E1120.MirrorCS");var subQ2=makeQuery(id+"F20.imprint","INTERSECT",VERTEX,{"derivedFrom":[subQ1,subQ0]});Q108=makeQuery(id+"F20.imprint","IMPRINT",FACE,{"disambiguationData":[TD([[makeQuery(id+"F20.imprint","IMPRINT",EDGE,{"disambiguationData":[TD([[subQ2,-1.0]])],"derivedFrom":subQ1}),1.0]])]});}
            var Q109;
            {var subQ0=sQuery(id+"F20.wireOp",EDGE,"E1341.MirrorCS");var subQ1=sQuery(id+"F20.wireOp",EDGE,"E1286.MirrorCS");var subQ2=makeQuery(id+"F20.imprint","INTERSECT",VERTEX,{"derivedFrom":[subQ1,subQ0]});Q109=makeQuery(id+"F20.imprint","IMPRINT",FACE,{"disambiguationData":[TD([[makeQuery(id+"F20.imprint","IMPRINT",EDGE,{"disambiguationData":[TD([[subQ2,-1.0]])],"derivedFrom":subQ1}),1.0]])]});}
            var Q110;
            {var subQ0=sQuery(id+"F20.wireOp",EDGE,"E1330.MirrorCS");var subQ1=sQuery(id+"F20.wireOp",EDGE,"E1271.MirrorCS");var subQ2=makeQuery(id+"F20.imprint","INTERSECT",VERTEX,{"derivedFrom":[subQ1,subQ0]});Q110=makeQuery(id+"F20.imprint","IMPRINT",FACE,{"disambiguationData":[TD([[makeQuery(id+"F20.imprint","IMPRINT",EDGE,{"disambiguationData":[TD([[subQ2,-1.0]])],"derivedFrom":subQ1}),1.0]])]});}
            var Q111;
            {var subQ0=sQuery(id+"F20.wireOp",EDGE,"E1393.MirrorCS");var subQ1=sQuery(id+"F20.wireOp",EDGE,"E1271.MirrorCS");var subQ2=makeQuery(id+"F20.imprint","INTERSECT",VERTEX,{"derivedFrom":[subQ1,subQ0]});Q111=makeQuery(id+"F20.imprint","IMPRINT",FACE,{"disambiguationData":[TD([[makeQuery(id+"F20.imprint","IMPRINT",EDGE,{"disambiguationData":[TD([[subQ2,-1.0]])],"derivedFrom":subQ1}),1.0]])]});}
            var Q112;
            {var subQ0=sQuery(id+"F20.wireOp",EDGE,"E1122.MirrorCS");var subQ1=sQuery(id+"F20.wireOp",EDGE,"E1116.MirrorCS");var subQ2=makeQuery(id+"F20.imprint","INTERSECT",VERTEX,{"derivedFrom":[subQ1,subQ0]});Q112=makeQuery(id+"F20.imprint","IMPRINT",FACE,{"disambiguationData":[TD([[makeQuery(id+"F20.imprint","IMPRINT",EDGE,{"disambiguationData":[TD([[subQ2,-1.0]])],"derivedFrom":subQ1}),1.0]])]});}
            var Q113;
            {var subQ0=sQuery(id+"F20.wireOp",EDGE,"E1301.MirrorCS");var subQ1=sQuery(id+"F20.wireOp",EDGE,"E1189.MirrorCS");var subQ2=makeQuery(id+"F20.imprint","INTERSECT",VERTEX,{"derivedFrom":[subQ1,subQ0]});Q113=makeQuery(id+"F20.imprint","IMPRINT",FACE,{"disambiguationData":[TD([[makeQuery(id+"F20.imprint","IMPRINT",EDGE,{"disambiguationData":[TD([[subQ2,-1.0]])],"derivedFrom":subQ1}),1.0]])]});}
            var Q114;
            {var subQ0=sQuery(id+"F20.wireOp",EDGE,"E1301.MirrorCS");var subQ1=sQuery(id+"F20.wireOp",EDGE,"E1167.MirrorCS");var subQ2=makeQuery(id+"F20.imprint","INTERSECT",VERTEX,{"derivedFrom":[subQ1,subQ0]});Q114=makeQuery(id+"F20.imprint","IMPRINT",FACE,{"disambiguationData":[TD([[makeQuery(id+"F20.imprint","IMPRINT",EDGE,{"disambiguationData":[TD([[subQ2,-1.0]])],"derivedFrom":subQ1}),-1.0]])]});}
            var Q115;
            {var subQ0=sQuery(id+"F20.wireOp",EDGE,"E1208.MirrorCS");var subQ1=sQuery(id+"F20.wireOp",EDGE,"E1166.MirrorCS");var subQ2=makeQuery(id+"F20.imprint","INTERSECT",VERTEX,{"derivedFrom":[subQ1,subQ0]});Q115=makeQuery(id+"F20.imprint","IMPRINT",FACE,{"disambiguationData":[TD([[makeQuery(id+"F20.imprint","IMPRINT",EDGE,{"disambiguationData":[TD([[subQ2,-1.0]])],"derivedFrom":subQ1}),-1.0]])]});}
            var Q116;
            {var subQ0=sQuery(id+"F20.wireOp",EDGE,"E1123.MirrorCS");var subQ1=sQuery(id+"F20.wireOp",EDGE,"E1115.MirrorCS");var subQ2=makeQuery(id+"F20.imprint","INTERSECT",VERTEX,{"derivedFrom":[subQ1,subQ0]});Q116=makeQuery(id+"F20.imprint","IMPRINT",FACE,{"disambiguationData":[TD([[makeQuery(id+"F20.imprint","IMPRINT",EDGE,{"disambiguationData":[TD([[subQ2,-1.0]])],"derivedFrom":subQ1}),-1.0]])]});}
            var Q117;
            {var subQ0=sQuery(id+"F20.wireOp",EDGE,"E1349.MirrorCS");var subQ1=sQuery(id+"F20.wireOp",EDGE,"E1302.MirrorCS");var subQ2=makeQuery(id+"F20.imprint","INTERSECT",VERTEX,{"derivedFrom":[subQ1,subQ0]});Q117=makeQuery(id+"F20.imprint","IMPRINT",FACE,{"disambiguationData":[TD([[makeQuery(id+"F20.imprint","IMPRINT",EDGE,{"disambiguationData":[TD([[subQ2,-1.0]])],"derivedFrom":subQ1}),-1.0]])]});}
            var Q118;
            {var subQ0=sQuery(id+"F20.wireOp",EDGE,"E1356.MirrorCS");var subQ1=sQuery(id+"F20.wireOp",EDGE,"E1302.MirrorCS");var subQ2=makeQuery(id+"F20.imprint","INTERSECT",VERTEX,{"derivedFrom":[subQ1,subQ0]});Q118=makeQuery(id+"F20.imprint","IMPRINT",FACE,{"disambiguationData":[TD([[makeQuery(id+"F20.imprint","IMPRINT",EDGE,{"disambiguationData":[TD([[subQ2,-1.0]])],"derivedFrom":subQ1}),-1.0]])]});}
            var Q119;
            {var subQ0=sQuery(id+"F20.wireOp",EDGE,"E1365.MirrorCS");var subQ1=sQuery(id+"F20.wireOp",EDGE,"E1331.MirrorCS");var subQ2=makeQuery(id+"F20.imprint","INTERSECT",VERTEX,{"derivedFrom":[subQ1,subQ0]});Q119=makeQuery(id+"F20.imprint","IMPRINT",FACE,{"disambiguationData":[TD([[makeQuery(id+"F20.imprint","IMPRINT",EDGE,{"disambiguationData":[TD([[subQ2,-1.0]])],"derivedFrom":subQ1}),-1.0]])]});}
            var Q120;
            {var subQ0=sQuery(id+"F20.wireOp",EDGE,"E1265.MirrorCS");var subQ1=sQuery(id+"F20.wireOp",EDGE,"E1119.MirrorCS");var subQ2=makeQuery(id+"F20.imprint","INTERSECT",VERTEX,{"derivedFrom":[subQ1,subQ0]});Q120=makeQuery(id+"F20.imprint","IMPRINT",FACE,{"disambiguationData":[TD([[makeQuery(id+"F20.imprint","IMPRINT",EDGE,{"disambiguationData":[TD([[subQ2,-1.0]])],"derivedFrom":subQ1}),-1.0]])]});}
            var Q121;
            {var subQ0=sQuery(id+"F20.wireOp",EDGE,"E1275.MirrorCS");var subQ1=sQuery(id+"F20.wireOp",EDGE,"E1188.MirrorCS");var subQ2=makeQuery(id+"F20.imprint","INTERSECT",VERTEX,{"derivedFrom":[subQ1,subQ0]});Q121=makeQuery(id+"F20.imprint","IMPRINT",FACE,{"disambiguationData":[TD([[makeQuery(id+"F20.imprint","IMPRINT",EDGE,{"disambiguationData":[TD([[subQ2,-1.0]])],"derivedFrom":subQ1}),-1.0]])]});}
            var Q122;
            {var subQ0=sQuery(id+"F20.wireOp",EDGE,"E1250.MirrorCS");var subQ1=sQuery(id+"F20.wireOp",EDGE,"E1166.MirrorCS");var subQ2=makeQuery(id+"F20.imprint","INTERSECT",VERTEX,{"derivedFrom":[subQ1,subQ0]});Q122=makeQuery(id+"F20.imprint","IMPRINT",FACE,{"disambiguationData":[TD([[makeQuery(id+"F20.imprint","IMPRINT",EDGE,{"disambiguationData":[TD([[subQ2,-1.0]])],"derivedFrom":subQ1}),-1.0]])]});}
            var Q123;
            {var subQ0=sQuery(id+"F20.wireOp",EDGE,"E1224.MirrorCS");var subQ1=sQuery(id+"F20.wireOp",EDGE,"E1193.MirrorCS");var subQ2=makeQuery(id+"F20.imprint","INTERSECT",VERTEX,{"derivedFrom":[subQ1,subQ0]});Q123=makeQuery(id+"F20.imprint","IMPRINT",FACE,{"disambiguationData":[TD([[makeQuery(id+"F20.imprint","IMPRINT",EDGE,{"disambiguationData":[TD([[subQ2,-1.0]])],"derivedFrom":subQ1}),-1.0]])]});}
            var Q124;
            {var subQ0=sQuery(id+"F20.wireOp",EDGE,"E1194.MirrorCS");var subQ1=sQuery(id+"F20.wireOp",EDGE,"E1193.MirrorCS");var subQ2=makeQuery(id+"F20.imprint","INTERSECT",VERTEX,{"derivedFrom":[subQ1,subQ0]});Q124=makeQuery(id+"F20.imprint","IMPRINT",FACE,{"disambiguationData":[TD([[makeQuery(id+"F20.imprint","IMPRINT",EDGE,{"disambiguationData":[TD([[subQ2,-1.0]])],"derivedFrom":subQ1}),-1.0]])]});}
            var Q125;
            {var subQ0=sQuery(id+"F20.wireOp",EDGE,"E1137.MirrorCS");var subQ1=sQuery(id+"F20.wireOp",EDGE,"E1153.MirrorCS");var subQ2=makeQuery(id+"F20.imprint","INTERSECT",VERTEX,{"derivedFrom":[subQ1,subQ0]});Q125=makeQuery(id+"F20.imprint","IMPRINT",FACE,{"disambiguationData":[TD([[makeQuery(id+"F20.imprint","IMPRINT",EDGE,{"disambiguationData":[TD([[subQ2,-1.0]])],"derivedFrom":subQ1}),-1.0]])]});}
            var Q126;
            {var subQ0=sQuery(id+"F20.wireOp",EDGE,"E1288.MirrorCS");var subQ1=sQuery(id+"F20.wireOp",EDGE,"E1241.MirrorCS");var subQ2=makeQuery(id+"F20.imprint","INTERSECT",VERTEX,{"derivedFrom":[subQ1,subQ0]});Q126=makeQuery(id+"F20.imprint","IMPRINT",FACE,{"disambiguationData":[TD([[makeQuery(id+"F20.imprint","IMPRINT",EDGE,{"disambiguationData":[TD([[subQ2,-1.0]])],"derivedFrom":subQ1}),1.0]])]});}
            var Q127;
            {var subQ0=sQuery(id+"F20.wireOp",EDGE,"E1288.MirrorCS");var subQ1=sQuery(id+"F20.wireOp",EDGE,"E1213.MirrorCS");var subQ2=makeQuery(id+"F20.imprint","INTERSECT",VERTEX,{"derivedFrom":[subQ1,subQ0]});Q127=makeQuery(id+"F20.imprint","IMPRINT",FACE,{"disambiguationData":[TD([[makeQuery(id+"F20.imprint","IMPRINT",EDGE,{"disambiguationData":[TD([[subQ2,-1.0]])],"derivedFrom":subQ1}),-1.0]])]});}
            var Q128;
            {var subQ0=sQuery(id+"F20.wireOp",EDGE,"E1401.MirrorCS");var subQ1=sQuery(id+"F20.wireOp",EDGE,"E1147.MirrorCS");var subQ2=makeQuery(id+"F20.imprint","INTERSECT",VERTEX,{"derivedFrom":[subQ1,subQ0]});Q128=makeQuery(id+"F20.imprint","IMPRINT",FACE,{"disambiguationData":[TD([[makeQuery(id+"F20.imprint","IMPRINT",EDGE,{"disambiguationData":[TD([[subQ2,-1.0]])],"derivedFrom":subQ1}),1.0]])]});}
            var Q129;
            {var subQ0=sQuery(id+"F20.wireOp",EDGE,"E1202.MirrorCS");var subQ1=sQuery(id+"F20.wireOp",EDGE,"E1150.MirrorCS");var subQ2=makeQuery(id+"F20.imprint","INTERSECT",VERTEX,{"derivedFrom":[subQ1,subQ0]});Q129=makeQuery(id+"F20.imprint","IMPRINT",FACE,{"disambiguationData":[TD([[makeQuery(id+"F20.imprint","IMPRINT",EDGE,{"disambiguationData":[TD([[subQ2,-1.0]])],"derivedFrom":subQ1}),-1.0]])]});}
            var Q130;
            {var subQ0=sQuery(id+"F20.wireOp",EDGE,"E1277.MirrorCS");var subQ1=sQuery(id+"F20.wireOp",EDGE,"E1178.MirrorCS");var subQ2=makeQuery(id+"F20.imprint","INTERSECT",VERTEX,{"derivedFrom":[subQ1,subQ0]});Q130=makeQuery(id+"F20.imprint","IMPRINT",FACE,{"disambiguationData":[TD([[makeQuery(id+"F20.imprint","IMPRINT",EDGE,{"disambiguationData":[TD([[subQ2,-1.0]])],"derivedFrom":subQ1}),1.0]])]});}
            extrude(context, id + "F21", {"entities" : qUnion([Q0, Q1, Q2, Q3, Q4, Q5, Q6, Q7, Q8, Q9, Q10, Q11, Q12, Q13, Q14, Q15, Q16, Q17, Q18, Q19, Q20, Q21, Q22, Q23, Q24, Q25, Q26, Q27, Q28, Q29, Q30, Q31, Q32, Q33, Q34, Q35, Q36, Q37, Q38, Q39, Q40, Q41, Q42, Q43, Q44, Q45, Q46, Q47, Q48, Q49, Q50, Q51, Q52, Q53, Q54, Q55, Q56, Q57, Q58, Q59, Q60, Q61, Q62, Q63, Q64, Q65, Q66, Q67, Q68, Q69, Q70, Q71, Q72, Q73, Q74, Q75, Q76, Q77, Q78, Q79, Q80, Q81, Q82, Q83, Q84, Q85, Q86, Q87, Q88, Q89, Q90, Q91, Q92, Q93, Q94, Q95, Q96, Q97, Q98, Q99, Q100, Q101, Q102, Q103, Q104, Q105, Q106, Q107, Q108, Q109, Q110, Q111, Q112, Q113, Q114, Q115, Q116, Q117, Q118, Q119, Q120, Q121, Q122, Q123, Q124, Q125, Q126, Q127, Q128, Q129, Q130]), "operationType" : NewBodyOperationType.REMOVE, "endBound" : BoundingType.THROUGH_ALL, "oppositeDirection" : true, "depth" : 25.4 * mm, "offsetDistance" : 25.4 * mm});
        }
    });
